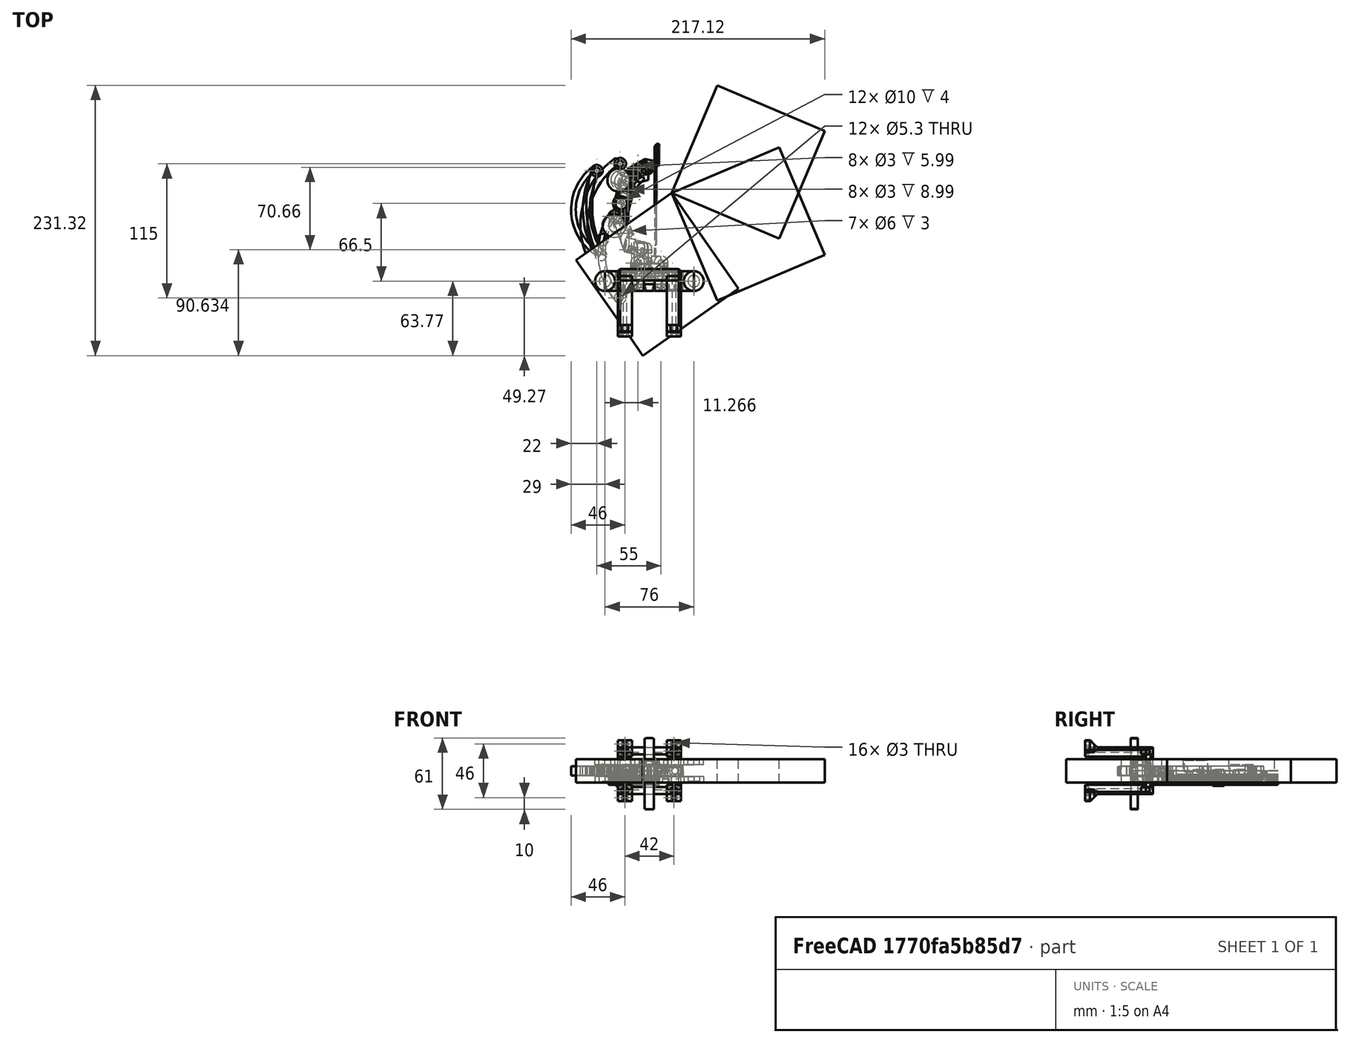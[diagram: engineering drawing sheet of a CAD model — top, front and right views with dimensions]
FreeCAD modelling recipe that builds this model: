
FCSTD DOCUMENT  (FreeCAD 0.19R24276 (Git))
Label: Gripper_024
License: All rights reserved
LicenseURL: http://en.wikipedia.org/wiki/All_rights_reserved
objects: Part::Cylinder×485, Part::Cut×312, Part::Box×216, Part::Compound×169, Part::Fillet×55, Mesh::Feature×27, Part::FeaturePython×21, Part::Chamfer×20, Part::Common×2, Part::Mirroring×1
note: 1281 computed .brp shape members not serialized (recipe doc carries the construction recipe); baked Part::Feature solids carry a one-line shape summary decoded from their .brp

FEATURE [Part::Cylinder] Cylinder036  label="Válec036"
  Angle = 360
  AttacherType = Attacher::AttachEngine3D
  Height = 5
  Placement = pos=(-20,30,5) rot=(0,0,1;0rad)
  Radius = 16
FEATURE [Part::Box] Box045  label="Krychle045"
  AttacherType = Attacher::AttachEngine3D
  Height = 12
  Length = 12
  Placement = pos=(-13,24,-2) rot=(0,0,1;0rad)
  Width = 12
FEATURE [Part::Cylinder] Cylinder037  label="Válec037"
  Angle = 360
  AttacherType = Attacher::AttachEngine3D
  Height = 4
  Placement = pos=(-10,30,1) rot=(0,0,1;0rad)
  Radius = 5
FEATURE [Part::Box] Box046  label="Krychle046"
  AttacherType = Attacher::AttachEngine3D
  Height = 12
  Length = 12
  Placement = pos=(-6.8,59.2,-2) rot=(0,0,-1;0.785398rad)
  Width = 16
FEATURE [Part::Box] Box047  label="Krychle047"
  AttacherType = Attacher::AttachEngine3D
  Height = 2
  Length = 6
  Placement = pos=(-2,11,20) rot=(0,0,1;0rad)
  Width = 6
FEATURE [Part::Box] Box049  label="Krychle049"
  AttacherType = Attacher::AttachEngine3D
  Height = 12
  Length = 12
  Placement = pos=(-13,36,-2) rot=(0,0,-1;0.261799rad)
  Width = 24
FEATURE [Part::Cylinder] Cylinder040  label="Válec040"
  Angle = 360
  AttacherType = Attacher::AttachEngine3D
  Height = 4
  Placement = pos=(10,-10,1) rot=(0,0,1;0rad)
  Radius = 5
FEATURE [Part::Box] Box053  label="Krychle053"
  AttacherType = Attacher::AttachEngine3D
  Height = 12
  Length = 12
  Placement = pos=(16,0,-2) rot=(0,0,1;0rad)
  Width = 80
FEATURE [Part::Cylinder] Cylinder042  label="Válec042"
  Angle = 360
  AttacherType = Attacher::AttachEngine3D
  Height = 5
  Placement = pos=(-20,30,5) rot=(0,0,1;0rad)
  Radius = 16
FEATURE [Part::Cylinder] Cylinder043  label="Válec043"
  Angle = 360
  AttacherType = Attacher::AttachEngine3D
  Height = 7
  Placement = pos=(10,-10,-2) rot=(0,0,1;0rad)
  Radius = 7
FEATURE [Part::Cut] Cut039
  Base = -> Cylinder043
  Tool = -> Cylinder040
FEATURE [Part::Cylinder] Cylinder039  label="Válec039"
  Angle = 360
  AttacherType = Attacher::AttachEngine3D
  Height = 5
  Placement = pos=(-20,30,5) rot=(0,0,1;0rad)
  Radius = 16
FEATURE [Part::Cut] Cut040
  Base = -> Box049
  Tool = -> Cylinder039
FEATURE [Part::Fillet] Fillet009
  Base = -> Cut040
  Edges = 1 edges r=20: [Edge3]
FEATURE [Part::Box] Box048  label="Krychle048"
  AttacherType = Attacher::AttachEngine3D
  Height = 12
  Length = 12
  Placement = pos=(-4.1,-0.4,-2) rot=(0,0,1;0.349066rad)
  Width = 26
FEATURE [Part::Cut] Cut038
  Base = -> Box048
  Tool = -> Cylinder042
FEATURE [Part::Fillet] Fillet011
  Base = -> Cut038
  Edges = 1 edges r=20: [Edge2]
FEATURE [Part::Fillet] Fillet016
  Base = -> Fillet011
  Edges = 1 edges r=2: [Edge2]
FEATURE [Part::Box] Box050  label="Krychle050"
  AttacherType = Attacher::AttachEngine3D
  Height = 12
  Length = 12
  Placement = pos=(4.5,70.5,-2) rot=(0,0,-1;1.309rad)
  Width = 12
FEATURE [Part::Cut] Cut037
  Base = -> Box050
  Tool = -> Box053
FEATURE [Part::Box] Box051  label="Krychle051"
  AttacherType = Attacher::AttachEngine3D
  Height = 12
  Length = 12
  Placement = pos=(11.4,-4.4,-2) rot=(0,0,1;1.309rad)
  Width = 18
FEATURE [Part::Chamfer] Chamfer001
  Base = -> Box051
  Edges = 2 edges r=4: [Edge1,Edge5]
FEATURE [Part::Fillet] Fillet010
  Base = -> Chamfer001
  Edges = 1 edges r=4: [Edge4]
FEATURE [Part::Fillet] Fillet015
  Base = -> Fillet010
  Edges = 1 edges r=3: [Edge2]
FEATURE [Part::Fillet] Fillet014
  Base = -> Fillet015
  Edges = 2 edges r=3: [Edge21,Edge23]
FEATURE [Part::Fillet] Fillet013
  Base = -> Fillet014
  Edges = 1 edges r=4: [Edge27]
FEATURE [Part::Box] Box052  label="Krychle052"
  AttacherType = Attacher::AttachEngine3D
  Height = 7
  Length = 12
  Placement = pos=(4,-10,-2) rot=(0,0,1;0rad)
  Width = 18
FEATURE [Part::Cylinder] Cylinder041  label="Válec041"
  Angle = 360
  AttacherType = Attacher::AttachEngine3D
  Height = 4
  Placement = pos=(10,-10,1) rot=(0,0,1;0rad)
  Radius = 5
FEATURE [Part::Cut] Cut036
  Base = -> Box052
  Tool = -> Cylinder041
FEATURE [Part::Fillet] Fillet012
  Base = -> Cut036
  Edges = 1 edges r=4: [Edge16]
FEATURE [Part::Cylinder] Cylinder044  label="Válec044"
  Angle = 360
  AttacherType = Attacher::AttachEngine3D
  Height = 3
  Placement = pos=(1,14,-2) rot=(0,0,1;0rad)
  Radius = 3
FEATURE [Part::Box] Box054  label="Krychle054"
  AttacherType = Attacher::AttachEngine3D
  Height = 2
  Length = 6
  Placement = pos=(-2,11,20) rot=(0,0,1;0rad)
  Width = 6
FEATURE [Part::Cylinder] Cylinder038  label="Válec038"
  Angle = 360
  AttacherType = Attacher::AttachEngine3D
  Height = 16
  Placement = pos=(1,14,1) rot=(0,0,1;0rad)
  Radius = 1.5
FEATURE [Part::Compound] Compound016
  Links = -> [Cylinder037,Cylinder036]
FEATURE [Part::Cut] Cut041
  Base = -> Box045
  Tool = -> Compound016
FEATURE [Part::Cylinder] Cylinder053  label="Válec053"
  Angle = 360
  AttacherType = Attacher::AttachEngine3D
  Height = 3
  Placement = pos=(1,14,-2) rot=(0,0,1;0rad)
  Radius = 3
FEATURE [Part::Compound] Compound018
  Links = -> [Box047,Cylinder038,Cylinder053]
  Placement = pos=(12.1,54,0) rot=(0,0,1;0.785398rad)
FEATURE [Part::Box] Box058  label="Krychle058"
  AttacherType = Attacher::AttachEngine3D
  Height = 2
  Length = 6
  Placement = pos=(-2,11,20) rot=(0,0,1;0rad)
  Width = 6
FEATURE [Part::Cylinder] Cylinder051  label="Válec051"
  Angle = 360
  AttacherType = Attacher::AttachEngine3D
  Height = 16
  Placement = pos=(1,14,1) rot=(0,0,1;0rad)
  Radius = 1.5
FEATURE [Part::Cylinder] Cylinder054  label="Válec054"
  Angle = 360
  AttacherType = Attacher::AttachEngine3D
  Height = 16
  Placement = pos=(1,14,1) rot=(0,0,1;0rad)
  Radius = 1.5
FEATURE [Part::Box] Box057  label="Krychle057"
  AttacherType = Attacher::AttachEngine3D
  Height = 2
  Length = 6
  Placement = pos=(-2,11,20) rot=(0,0,1;0rad)
  Width = 6
FEATURE [Part::Cylinder] Cylinder045  label="Válec045"
  Angle = 360
  AttacherType = Attacher::AttachEngine3D
  Height = 3
  Placement = pos=(1,14,-2) rot=(0,0,1;0rad)
  Radius = 3
FEATURE [Part::Box] Box059  label="Krychle059"
  AttacherType = Attacher::AttachEngine3D
  Height = 2
  Length = 6
  Placement = pos=(-2,11,4) rot=(0,0,1;0rad)
  Width = 6
FEATURE [Part::Box] Box056  label="Krychle056"
  AttacherType = Attacher::AttachEngine3D
  Height = 2
  Length = 6
  Placement = pos=(-2,11,20) rot=(0,0,1;0rad)
  Width = 6
FEATURE [Part::Box] Box060  label="Krychle060"
  AttacherType = Attacher::AttachEngine3D
  Height = 2
  Length = 6
  Placement = pos=(-2,11,4) rot=(0,0,1;0rad)
  Width = 6
FEATURE [Part::Cylinder] Cylinder048  label="Válec048"
  Angle = 360
  AttacherType = Attacher::AttachEngine3D
  Height = 3
  Placement = pos=(1,14,-2) rot=(0,0,1;0rad)
  Radius = 3
FEATURE [Part::Compound] Compound014
  Links = -> [Box056,Cylinder051,Cylinder048]
  Placement = pos=(-2.9,-11.9,0) rot=(0,0,-1;0.261799rad)
FEATURE [Part::Cylinder] Cylinder049  label="Válec049"
  Angle = 360
  AttacherType = Attacher::AttachEngine3D
  Height = 3
  Placement = pos=(1,14,-2) rot=(0,0,1;0rad)
  Radius = 3
FEATURE [Part::Box] Box055  label="Krychle055"
  AttacherType = Attacher::AttachEngine3D
  Height = 2
  Length = 6
  Placement = pos=(-2,11,20) rot=(0,0,1;0rad)
  Width = 6
FEATURE [Part::Cylinder] Cylinder047  label="Válec047"
  Angle = 360
  AttacherType = Attacher::AttachEngine3D
  Height = 16
  Placement = pos=(1,14,1) rot=(0,0,1;0rad)
  Radius = 1.5
FEATURE [Part::Compound] Compound015
  Links = -> [Box055,Cylinder047,Cylinder045]
  Placement = pos=(-6.1,31,0) rot=(0,0,-1;0.261799rad)
FEATURE [Part::Cut] Cut043
  Base = -> Fillet009
  Tool = -> Compound015
FEATURE [Part::Cylinder] Cylinder050  label="Válec050"
  Angle = 360
  AttacherType = Attacher::AttachEngine3D
  Height = 16
  Placement = pos=(1,14,1) rot=(0,0,1;0rad)
  Radius = 1.5
FEATURE [Part::Compound] Compound011
  Links = -> [Box057,Cylinder050,Cylinder049]
  Placement = pos=(-2.9,-11.9,0) rot=(0,0,-1;0.261799rad)
FEATURE [Part::Cut] Cut044
  Base = -> Fillet013
  Tool = -> Compound011
FEATURE [Part::Cylinder] Cylinder046  label="Válec046"
  Angle = 360
  AttacherType = Attacher::AttachEngine3D
  Height = 3
  Placement = pos=(1,14,-2) rot=(0,0,1;0rad)
  Radius = 3
FEATURE [Part::Compound] Compound013
  Links = -> [Box058,Cylinder054,Cylinder046]
  Placement = pos=(3.5,2,0) rot=(0,0,1;0.349066rad)
FEATURE [Part::Cut] Cut042
  Base = -> Fillet016
  Tool = -> Compound013
FEATURE [Part::Cut] Cut045
  Base = -> Cut042
  Tool = -> Compound014
FEATURE [Part::Cylinder] Cylinder052  label="Válec052"
  Angle = 360
  AttacherType = Attacher::AttachEngine3D
  Height = 16
  Placement = pos=(1,14,1) rot=(0,0,1;0rad)
  Radius = 1.5
FEATURE [Part::Compound] Compound012
  Links = -> [Box054,Cylinder052,Cylinder044]
  Placement = pos=(12.1,54,0) rot=(0,0,1;0.785398rad)
FEATURE [Part::Cut] Cut049
  Base = -> Box046
  Tool = -> Compound018
FEATURE [Part::Cut] Cut047
  Base = -> Cut037
  Tool = -> Compound012
FEATURE [Part::Cylinder] Cylinder064  label="Válec064"
  Angle = 360
  AttacherType = Attacher::AttachEngine3D
  Height = 12
  Placement = pos=(1,14,6) rot=(0,0,1;0rad)
  Radius = 1.5
FEATURE [Part::Box] Box063  label="Krychle063"
  AttacherType = Attacher::AttachEngine3D
  Height = 2
  Length = 6
  Placement = pos=(-2,11,4) rot=(0,0,1;0rad)
  Width = 6
FEATURE [Part::Cylinder] Cylinder065  label="Válec065"
  Angle = 360
  AttacherType = Attacher::AttachEngine3D
  Height = 12
  Placement = pos=(1,14,6) rot=(0,0,1;0rad)
  Radius = 1.5
FEATURE [Part::Box] Box064  label="Krychle064"
  AttacherType = Attacher::AttachEngine3D
  Height = 2
  Length = 6
  Placement = pos=(-2,11,4) rot=(0,0,1;0rad)
  Width = 6
FEATURE [Part::Cylinder] Cylinder066  label="Válec066"
  Angle = 360
  AttacherType = Attacher::AttachEngine3D
  Height = 4
  Placement = pos=(1,14,-0.1) rot=(0,0,1;0rad)
  Radius = 1.5
FEATURE [Part::Cylinder] Cylinder057  label="Válec057"
  Angle = 360
  AttacherType = Attacher::AttachEngine3D
  Height = 12
  Placement = pos=(1,14,6) rot=(0,0,1;0rad)
  Radius = 1.5
FEATURE [Part::Cylinder] Cylinder058  label="Válec058"
  Angle = 360
  AttacherType = Attacher::AttachEngine3D
  Height = 12
  Placement = pos=(1,14,6) rot=(0,0,1;0rad)
  Radius = 1.5
FEATURE [Part::Cylinder] Cylinder055  label="Válec055"
  Angle = 360
  AttacherType = Attacher::AttachEngine3D
  Height = 4
  Placement = pos=(1,14,-0.1) rot=(0,0,1;0rad)
  Radius = 1.5
FEATURE [Part::Compound] Compound019
  Links = -> [Box060,Cylinder058,Cylinder055]
  Placement = pos=(6,53,2) rot=(0,1,0;1.5708rad)
FEATURE [Part::Cut] Cut048
  Base = -> Cut047
  Tool = -> Compound019
FEATURE [Part::Cylinder] Cylinder056  label="Válec056"
  Angle = 360
  AttacherType = Attacher::AttachEngine3D
  Height = 4
  Placement = pos=(1,14,0) rot=(0,0,1;0rad)
  Radius = 1.5
FEATURE [Part::Compound] Compound020
  Links = -> [Box059,Cylinder057,Cylinder056]
  Placement = pos=(6,53,2) rot=(0,1,0;1.5708rad)
FEATURE [Part::Cut] Cut046
  Base = -> Cut049
  Tool = -> Compound020
FEATURE [Part::Cylinder] Cylinder063  label="Válec063"
  Angle = 360
  AttacherType = Attacher::AttachEngine3D
  Height = 4
  Placement = pos=(1,14,-0.1) rot=(0,0,1;0rad)
  Radius = 1.5
FEATURE [Part::Compound] Compound024
  Links = -> [Box063,Cylinder064,Cylinder063]
  Placement = pos=(6,-14,2) rot=(0,1,0;1.5708rad)
FEATURE [Part::Cut] Cut052
  Base = -> Fillet012
  Tool = -> Compound024
FEATURE [Part::Compound] Compound026
  Links = -> [Box064,Cylinder065,Cylinder066]
  Placement = pos=(6,-14,2) rot=(0,1,0;1.5708rad)
FEATURE [Part::Cut] Cut053
  Base = -> Cut044
  Tool = -> Compound026
FEATURE [Part::Compound] Compound027  label="revised_finger_upper"
  Links = -> [Cut039,Cut041,Cut043,Cut045,Cut046,Cut048,Cut052,Cut053]
FEATURE [Part::Cylinder] Cylinder067  label="Válec067"
  Angle = 360
  AttacherType = Attacher::AttachEngine3D
  Height = 7
  Placement = pos=(10,-10,-2) rot=(0,0,1;0rad)
  Radius = 7
FEATURE [Part::Cylinder] Cylinder068  label="Válec068"
  Angle = 360
  AttacherType = Attacher::AttachEngine3D
  Height = 4
  Placement = pos=(10,-10,1) rot=(0,0,1;0rad)
  Radius = 5
FEATURE [Part::Cut] Cut054
  Base = -> Cylinder067
  Placement = pos=(3,-1,0) rot=(0,0,1;0rad)
  Tool = -> Cylinder068
FEATURE [Part::Box] Box065  label="Krychle065"
  AttacherType = Attacher::AttachEngine3D
  Height = 12
  Length = 12
  Placement = pos=(-13,24,-2) rot=(0,0,1;0rad)
  Width = 18
FEATURE [Part::Box] Box066  label="Krychle066"
  AttacherType = Attacher::AttachEngine3D
  Height = 12
  Length = 12
  Placement = pos=(-13,42,-2) rot=(0,0,-1;0.261799rad)
  Width = 20
FEATURE [Part::Box] Box067  label="Krychle067"
  AttacherType = Attacher::AttachEngine3D
  Height = 12
  Length = 12
  Placement = pos=(-4.1,-0.4,-2) rot=(0,0,1;0.349066rad)
  Width = 26
FEATURE [Part::Box] Box068  label="Krychle068"
  AttacherType = Attacher::AttachEngine3D
  Height = 12
  Length = 12
  Placement = pos=(-7.85,61.2,-2) rot=(0,0,-1;0.610865rad)
  Width = 12
FEATURE [Part::Box] Box069  label="Krychle069"
  AttacherType = Attacher::AttachEngine3D
  Height = 12
  Length = 12
  Placement = pos=(5,60.6,-2) rot=(0,0,1;0.523599rad)
  Width = 12
FEATURE [Part::Box] Box070  label="Krychle070"
  AttacherType = Attacher::AttachEngine3D
  Height = 7
  Length = 12
  Placement = pos=(4,-10,-2) rot=(0,0,1;0rad)
  Width = 18
FEATURE [Part::Box] Box071  label="Krychle071"
  AttacherType = Attacher::AttachEngine3D
  Height = 12
  Length = 12
  Placement = pos=(13.25,-5,-2) rot=(0,0,1;1.309rad)
  Width = 18
FEATURE [Part::Cylinder] Cylinder069  label="Válec069"
  Angle = 360
  AttacherType = Attacher::AttachEngine3D
  Height = 10
  Placement = pos=(-9,24,1) rot=(0,0,1;0rad)
  Radius = 5
FEATURE [Part::Cylinder] Cylinder070  label="Válec070"
  Angle = 360
  AttacherType = Attacher::AttachEngine3D
  Height = 4
  Placement = pos=(-10,30,1) rot=(0,0,1;0rad)
  Radius = 5
FEATURE [Part::Cylinder] Cylinder071  label="Válec071"
  Angle = 360
  AttacherType = Attacher::AttachEngine3D
  Height = 10
  Placement = pos=(-7,41,1) rot=(0,0,1;0rad)
  Radius = 5
FEATURE [Part::Cylinder] Cylinder072  label="Válec072"
  Angle = 360
  AttacherType = Attacher::AttachEngine3D
  Height = 7
  Placement = pos=(-7,41,-2) rot=(0,0,1;0rad)
  Radius = 7
FEATURE [Part::Cylinder] Cylinder073  label="Válec073"
  Angle = 360
  AttacherType = Attacher::AttachEngine3D
  Height = 7
  Placement = pos=(-7,41,5) rot=(0,0,1;0rad)
  Radius = 7
FEATURE [Part::Cut] Cut
  Base = -> Box065
  Tool = -> Cylinder073
FEATURE [Part::Cylinder] Cylinder074  label="Válec074"
  Angle = 360
  AttacherType = Attacher::AttachEngine3D
  Height = 10
  Placement = pos=(-7,41,1) rot=(0,0,1;0rad)
  Radius = 5
FEATURE [Part::Cut] Cut055
  Base = -> Cylinder072
  Tool = -> Cylinder074
FEATURE [Part::Cylinder] Cylinder075  label="Válec075"
  Angle = 360
  AttacherType = Attacher::AttachEngine3D
  Height = 10
  Placement = pos=(-7,41,1) rot=(0,0,1;0rad)
  Radius = 5
FEATURE [Part::Cut] Cut056
  Base = -> Cut
  Tool = -> Cylinder075
FEATURE [Part::Cylinder] Cylinder076  label="Válec076"
  Angle = 360
  AttacherType = Attacher::AttachEngine3D
  Height = 4
  Placement = pos=(-7,41,6) rot=(0,0,1;0rad)
  Radius = 6
FEATURE [Part::Box] Box072  label="Krychle072"
  AttacherType = Attacher::AttachEngine3D
  Height = 4
  Length = 12
  Placement = pos=(-13,42,6) rot=(0,0,-1;0.261799rad)
  Width = 20
FEATURE [Part::Cylinder] Cylinder077  label="Válec077"
  Angle = 360
  AttacherType = Attacher::AttachEngine3D
  Height = 8
  Placement = pos=(-7,41,-2) rot=(0,0,1;0rad)
  Radius = 9
FEATURE [Part::Cut] Cut057
  Base = -> Box066
  Tool = -> Cylinder077
FEATURE [Part::Cut] Cut058
  Base = -> Box066
  Tool = -> Cylinder077
FEATURE [Part::Cylinder] Cylinder078  label="Válec078"
  Angle = 360
  AttacherType = Attacher::AttachEngine3D
  Height = 10
  Placement = pos=(-5,59,1) rot=(0,0,1;0rad)
  Radius = 5
FEATURE [Part::Cylinder] Cylinder079  label="Válec079"
  Angle = 360
  AttacherType = Attacher::AttachEngine3D
  Height = 10
  Placement = pos=(-9,61,5) rot=(0,0,1;0rad)
  Radius = 10
FEATURE [Part::Cut] Cut059
  Base = -> Box068
  Tool = -> Cylinder079
FEATURE [Part::Cylinder] Cylinder080  label="Válec080"
  Angle = 360
  AttacherType = Attacher::AttachEngine3D
  Height = 10
  Placement = pos=(-9,61,5) rot=(0,0,1;0rad)
  Radius = 10
FEATURE [Part::Cut] Cut060
  Base = -> Box072
  Tool = -> Cylinder080
FEATURE [Part::Cylinder] Cylinder081  label="Válec081"
  Angle = 360
  AttacherType = Attacher::AttachEngine3D
  Height = 10
  Placement = pos=(-9,61,5) rot=(0,0,1;0rad)
  Radius = 10
FEATURE [Part::Cut] Cut061
  Base = -> Cut057
  Tool = -> Cylinder081
FEATURE [Part::Cylinder] Cylinder082  label="Válec082"
  Angle = 360
  AttacherType = Attacher::AttachEngine3D
  Height = 10
  Placement = pos=(-9,61,5) rot=(0,0,1;0rad)
  Radius = 10
FEATURE [Part::Cut] Cut062
  Base = -> Cut058
  Tool = -> Cylinder082
FEATURE [Part::Cylinder] Cylinder083  label="Válec083"
  Angle = 360
  AttacherType = Attacher::AttachEngine3D
  Height = 10
  Placement = pos=(-5,59,1) rot=(0,0,1;0rad)
  Radius = 5
FEATURE [Part::Cylinder] Cylinder084  label="Válec084"
  Angle = 360
  AttacherType = Attacher::AttachEngine3D
  Height = 10
  Placement = pos=(-5,59,1) rot=(0,0,1;0rad)
  Radius = 5
FEATURE [Part::Cut] Cut063
  Base = -> Cut061
  Tool = -> Cylinder083
FEATURE [Part::Cylinder] Cylinder085  label="Válec085"
  Angle = 360
  AttacherType = Attacher::AttachEngine3D
  Height = 10
  Placement = pos=(-9,61,5) rot=(0,0,1;0rad)
  Radius = 10
FEATURE [Part::Cylinder] Cylinder086  label="Válec086"
  Angle = 360
  AttacherType = Attacher::AttachEngine3D
  Height = 10
  Placement = pos=(-9,61,5) rot=(0,0,1;0rad)
  Radius = 10
FEATURE [Part::Cylinder] Cylinder087  label="Válec087"
  Angle = 360
  AttacherType = Attacher::AttachEngine3D
  Height = 10
  Placement = pos=(-5,59,1) rot=(0,0,1;0rad)
  Radius = 5
FEATURE [Part::Cut] Cut064
  Base = -> Cut059
  Tool = -> Cylinder087
FEATURE [Part::Fillet] Fillet
  Base = -> Cut064
  Edges = 1 edges r=3: [Edge5]
FEATURE [Part::Fillet] Fillet017
  Base = -> Cut063
  Edges = 1 edges r=2: [Edge3]
FEATURE [Part::Cylinder] Cylinder088  label="Válec088"
  Angle = 360
  AttacherType = Attacher::AttachEngine3D
  Height = 10
  Placement = pos=(-7,41,0) rot=(0,0,1;0rad)
  Radius = 5
FEATURE [Part::Cylinder] Cylinder089  label="Válec089"
  Angle = 360
  AttacherType = Attacher::AttachEngine3D
  Height = 10
  Placement = pos=(-7,41,-3) rot=(0,0,1;0rad)
  Radius = 5
FEATURE [Part::Cut] Cut065
  Base = -> Cylinder076
  Tool = -> Cylinder088
FEATURE [Part::Cylinder] Cylinder090  label="Válec090"
  Angle = 360
  AttacherType = Attacher::AttachEngine3D
  Height = 4
  Placement = pos=(-7,41,6) rot=(0,0,1;0rad)
  Radius = 6
FEATURE [Mesh::Feature] Mesh  label="Grip_finger-tip (Meshed)"
FEATURE [Part::Cylinder] Cylinder091  label="Válec091"
  Angle = 360
  AttacherType = Attacher::AttachEngine3D
  Height = 10
  Placement = pos=(-9,23,1) rot=(0,0,1;0rad)
  Radius = 5
FEATURE [Part::Cylinder] Cylinder092  label="Válec092"
  Angle = 360
  AttacherType = Attacher::AttachEngine3D
  Height = 10
  Placement = pos=(-13,22,5) rot=(0,0,1;0rad)
  Radius = 10
FEATURE [Part::Cut] Cut066
  Base = -> Box067
  Tool = -> Cylinder092
FEATURE [Part::Cylinder] Cylinder093  label="Válec093"
  Angle = 360
  AttacherType = Attacher::AttachEngine3D
  Height = 10
  Placement = pos=(-13,22,9) rot=(0,0,1;0rad)
  Radius = 10
FEATURE [Part::Cylinder] Cylinder094  label="Válec094"
  Angle = 360
  AttacherType = Attacher::AttachEngine3D
  Height = 10
  Placement = pos=(-13,22,5) rot=(0,0,1;0rad)
  Radius = 10
FEATURE [Part::Cut] Cut067
  Base = -> Cut056
  Tool = -> Cylinder094
FEATURE [Part::Cylinder] Cylinder095  label="Válec095"
  Angle = 360
  AttacherType = Attacher::AttachEngine3D
  Height = 10
  Placement = pos=(-9,23,1) rot=(0,0,1;0rad)
  Radius = 5
FEATURE [Part::Cut] Cut068
  Base = -> Cut066
  Tool = -> Cylinder095
FEATURE [Part::Cut] Cut069
  Base = -> Cut067
  Tool = -> Cylinder091
FEATURE [Part::Cylinder] Cylinder096  label="Válec096"
  Angle = 360
  AttacherType = Attacher::AttachEngine3D
  Height = 4
  Placement = pos=(10,-10,1) rot=(0,0,1;0rad)
  Radius = 5
FEATURE [Part::Cut] Cut070
  Base = -> Box070
  Placement = pos=(3,0,0) rot=(0,0,1;0rad)
  Tool = -> Cylinder096
FEATURE [Part::Fillet] Fillet020
  Base = -> Cut070
  Edges = 1 edges r=4: [Edge16]
  Placement = pos=(0,-1,0) rot=(0,0,1;0rad)
FEATURE [Part::Fillet] Fillet021
  Base = -> Box071
  Edges = 2 edges r=4: [Edge1,Edge5]
FEATURE [Part::Fillet] Fillet022
  Base = -> Cut069
  Edges = 1 edges r=4: [Edge10]
FEATURE [Part::Fillet] Fillet023
  Base = -> Cut068
  Edges = 1 edges r=6: [Edge2]
FEATURE [Part::Compound] Compound028
  Links = -> [Fillet023,Fillet022,Fillet021,Fillet020,Cut055,Cut054]
FEATURE [Part::Fillet] Fillet024  label="Grip_finger-root_precur"
  Base = -> Compound028
  Edges = 1 edges r=2: [Edge53]
FEATURE [Part::Fillet] Fillet025
  Base = -> Box069
  Edges = 1 edges r=4: [Edge5]
FEATURE [Part::Fillet] Fillet026
  Base = -> Fillet017
  Edges = 1 edges r=3: [Edge28]
FEATURE [Part::Compound] Compound  label="Grip_finger-tip_precur"
  Links = -> [Fillet025,Fillet026,Fillet,Cylinder090]
FEATURE [Part::Cylinder] Cylinder097  label="Válec097"
  Angle = 360
  AttacherType = Attacher::AttachEngine3D
  Height = 4
  Placement = pos=(-7,41,6) rot=(0,0,1;0rad)
  Radius = 6
FEATURE [Part::Cylinder] Cylinder098  label="Válec098"
  Angle = 360
  AttacherType = Attacher::AttachEngine3D
  Height = 7
  Placement = pos=(-5,59.5,-2) rot=(0,0,1;0rad)
  Radius = 8
FEATURE [Part::Cylinder] Cylinder099  label="Válec099"
  Angle = 360
  AttacherType = Attacher::AttachEngine3D
  Height = 10
  Placement = pos=(-8,61,1) rot=(0,0,1;0rad)
  Radius = 5
FEATURE [Part::Cut] Cut074
  Base = -> Cylinder098
  Tool = -> Cylinder099
FEATURE [Part::Cylinder] Cylinder100  label="Válec100"
  Angle = 360
  AttacherType = Attacher::AttachEngine3D
  Height = 10
  Placement = pos=(-8,61,1) rot=(0,0,1;0rad)
  Radius = 5
FEATURE [Part::Box] Box073  label="Krychle073"
  AttacherType = Attacher::AttachEngine3D
  Height = 12
  Length = 12
  Placement = pos=(-13,42,-2) rot=(0,0,-1;0.261799rad)
  Width = 20
FEATURE [Part::Box] Box074  label="Krychle074"
  AttacherType = Attacher::AttachEngine3D
  Height = 12
  Length = 12
  Placement = pos=(-7.85,61.2,-2) rot=(0,0,-1;0.610865rad)
  Width = 12
FEATURE [Part::Box] Box075  label="Krychle075"
  AttacherType = Attacher::AttachEngine3D
  Height = 12
  Length = 12
  Placement = pos=(5,60.6,-2) rot=(0,0,1;0.523599rad)
  Width = 12
FEATURE [Part::Fillet] Fillet029
  Base = -> Box075
  Edges = 1 edges r=4: [Edge5]
FEATURE [Part::Cylinder] Cylinder101  label="Válec101"
  Angle = 360
  AttacherType = Attacher::AttachEngine3D
  Height = 8
  Placement = pos=(-7,41,-2) rot=(0,0,1;0rad)
  Radius = 9
FEATURE [Part::Cut] Cut075
  Base = -> Box073
  Tool = -> Cylinder101
FEATURE [Part::Cylinder] Cylinder102  label="Válec102"
  Angle = 360
  AttacherType = Attacher::AttachEngine3D
  Height = 10
  Placement = pos=(-9,61,5) rot=(0,0,1;0rad)
  Radius = 10
FEATURE [Part::Cut] Cut076
  Base = -> Box074
  Tool = -> Cylinder102
FEATURE [Part::Cylinder] Cylinder103  label="Válec103"
  Angle = 360
  AttacherType = Attacher::AttachEngine3D
  Height = 10
  Placement = pos=(-9,61,5) rot=(0,0,1;0rad)
  Radius = 10
FEATURE [Part::Cut] Cut077
  Base = -> Cut075
  Tool = -> Cylinder103
FEATURE [Part::Cylinder] Cylinder104  label="Válec104"
  Angle = 360
  AttacherType = Attacher::AttachEngine3D
  Height = 10
  Placement = pos=(-5,59,1) rot=(0,0,1;0rad)
  Radius = 5
FEATURE [Part::Cut] Cut071
  Base = -> Cut077
  Tool = -> Cylinder104
FEATURE [Part::Fillet] Fillet027
  Base = -> Cut071
  Edges = 1 edges r=2: [Edge3]
FEATURE [Part::Fillet] Fillet030
  Base = -> Fillet027
  Edges = 1 edges r=1: [Edge28]
FEATURE [Part::Cylinder] Cylinder105  label="Válec105"
  Angle = 360
  AttacherType = Attacher::AttachEngine3D
  Height = 10
  Placement = pos=(-5,59,1) rot=(0,0,1;0rad)
  Radius = 5
FEATURE [Part::Cut] Cut072
  Base = -> Cut076
  Tool = -> Cylinder105
FEATURE [Part::Fillet] Fillet028
  Base = -> Cut072
  Edges = 1 edges r=3: [Edge5]
FEATURE [Part::Cut] Cut073
  Base = -> Fillet028
  Tool = -> Cylinder100
FEATURE [Part::Cylinder] Cylinder029  label="Válec029"
  Angle = 360
  AttacherType = Attacher::AttachEngine3D
  Height = 20
  Placement = pos=(1,14,4.01) rot=(0,0,1;0rad)
  Radius = 1.5
FEATURE [Part::Cylinder] Cylinder106  label="Válec106"
  Angle = 360
  AttacherType = Attacher::AttachEngine3D
  Height = 20
  Placement = pos=(1,14,4.01) rot=(0,0,1;0rad)
  Radius = 1.5
FEATURE [Part::Cylinder] Cylinder107  label="Válec107"
  Angle = 360
  AttacherType = Attacher::AttachEngine3D
  Height = 3
  Placement = pos=(1,14,-1.01) rot=(0,0,1;0rad)
  Radius = 1.5
FEATURE [Part::Box] Box076  label="Krychle076"
  AttacherType = Attacher::AttachEngine3D
  Height = 2
  Length = 6
  Placement = pos=(-2,11,2) rot=(0,0,1;0rad)
  Width = 6
FEATURE [Part::Compound] Compound023
  Links = -> [Box076,Cylinder106,Cylinder107]
  Placement = pos=(12.3,47.5,0) rot=(0,0,1;1.309rad)
FEATURE [Part::Box] Box077  label="Krychle077"
  AttacherType = Attacher::AttachEngine3D
  Height = 2
  Length = 6
  Placement = pos=(-2,11,2) rot=(0,0,1;0rad)
  Width = 6
FEATURE [Part::Cylinder] Cylinder108  label="Válec108"
  Angle = 360
  AttacherType = Attacher::AttachEngine3D
  Height = 3
  Placement = pos=(1,14,-1.01) rot=(0,0,1;0rad)
  Radius = 1.5
FEATURE [Part::Cylinder] Cylinder109  label="Válec109"
  Angle = 360
  AttacherType = Attacher::AttachEngine3D
  Height = 20
  Placement = pos=(1,14,4.01) rot=(0,0,1;0rad)
  Radius = 1.5
FEATURE [Part::Cylinder] Cylinder028  label="Válec028"
  Angle = 360
  AttacherType = Attacher::AttachEngine3D
  Height = 3
  Placement = pos=(1,14,-1.01) rot=(0,0,1;0rad)
  Radius = 1.5
FEATURE [Part::Box] Box041  label="Krychle041"
  AttacherType = Attacher::AttachEngine3D
  Height = 2
  Length = 6
  Placement = pos=(-2,11,2) rot=(0,0,1;0rad)
  Width = 6
FEATURE [Part::Compound] Compound029
  Links = -> [Box077,Cylinder109,Cylinder108]
  Placement = pos=(12.3,47.5,0) rot=(0,0,1;1.309rad)
FEATURE [Part::Cut] Cut083
  Base = -> Fillet030
  Tool = -> Compound029
FEATURE [Part::Compound] Compound006
  Links = -> [Box041,Cylinder029,Cylinder028]
  Placement = pos=(9.4,57.4,0) rot=(0,0,1;0.523599rad)
FEATURE [Part::Cut] Cut084
  Base = -> Cut074
  Tool = -> Compound023
FEATURE [Part::Cylinder] Cylinder110  label="Válec110"
  Angle = 360
  AttacherType = Attacher::AttachEngine3D
  Height = 20
  Placement = pos=(1,14,4.01) rot=(0,0,1;0rad)
  Radius = 1.5
FEATURE [Part::Cylinder] Cylinder111  label="Válec111"
  Angle = 360
  AttacherType = Attacher::AttachEngine3D
  Height = 3
  Placement = pos=(1,14,-1.01) rot=(0,0,1;0rad)
  Radius = 1.5
FEATURE [Part::Box] Box078  label="Krychle078"
  AttacherType = Attacher::AttachEngine3D
  Height = 2
  Length = 6
  Placement = pos=(-2,11,2) rot=(0,0,1;0rad)
  Width = 6
FEATURE [Part::Cylinder] Cylinder112  label="Válec112"
  Angle = 360
  AttacherType = Attacher::AttachEngine3D
  Height = 20
  Placement = pos=(1,14,4.01) rot=(0,0,1;0rad)
  Radius = 1.5
FEATURE [Part::Cylinder] Cylinder113  label="Válec113"
  Angle = 360
  AttacherType = Attacher::AttachEngine3D
  Height = 3
  Placement = pos=(1,14,-1.01) rot=(0,0,1;0rad)
  Radius = 1.5
FEATURE [Part::Box] Box079  label="Krychle079"
  AttacherType = Attacher::AttachEngine3D
  Height = 2
  Length = 6
  Placement = pos=(-2,11,2) rot=(0,0,1;0rad)
  Width = 6
FEATURE [Part::Box] Box080  label="Krychle080"
  AttacherType = Attacher::AttachEngine3D
  Height = 2
  Length = 6
  Placement = pos=(-2,11,4) rot=(0,0,1;0rad)
  Width = 6
FEATURE [Part::Cylinder] Cylinder114  label="Válec114"
  Angle = 360
  AttacherType = Attacher::AttachEngine3D
  Height = 12
  Placement = pos=(1,14,6) rot=(0,0,1;0rad)
  Radius = 1.5
FEATURE [Part::Cylinder] Cylinder115  label="Válec115"
  Angle = 360
  AttacherType = Attacher::AttachEngine3D
  Height = 4
  Placement = pos=(1,14,0) rot=(0,0,1;0rad)
  Radius = 1.5
FEATURE [Part::Cylinder] Cylinder117  label="Válec117"
  Angle = 360
  AttacherType = Attacher::AttachEngine3D
  Height = 6
  Placement = pos=(-7,41,5) rot=(0,0,1;0rad)
  Radius = 2.6
FEATURE [Part::Cut] Cut082
  Base = -> Cylinder097
  Tool = -> Cylinder117
FEATURE [Part::Cylinder] Cylinder118  label="Válec118"
  Angle = 360
  AttacherType = Attacher::AttachEngine3D
  Height = 6
  Placement = pos=(-7,41,5) rot=(0,0,1;0rad)
  Radius = 2.6
FEATURE [Part::Cut] Cut085
  Base = -> Cut083
  Tool = -> Cylinder118
FEATURE [Part::Compound] Compound025
  Links = -> [Box078,Cylinder110,Cylinder111]
  Placement = pos=(12.3,47.5,0) rot=(0,0,1;1.309rad)
FEATURE [Part::Cut] Cut078
  Base = -> Cut073
  Tool = -> Compound025
FEATURE [Part::Cut] Cut080
  Base = -> Cut078
  Tool = -> Compound006
FEATURE [Part::Compound] Compound031
  Links = -> [Box079,Cylinder112,Cylinder113]
  Placement = pos=(9.4,57.4,0) rot=(0,0,1;0.523599rad)
FEATURE [Part::Cut] Cut079
  Base = -> Fillet029
  Tool = -> Compound031
FEATURE [Part::Compound] Compound032
  Links = -> [Box080,Cylinder114,Cylinder115]
  Placement = pos=(11.7,56.9,2) rot=(-0.250563,0.935113,0.250563;1.63782rad)
FEATURE [Part::Cut] Cut081
  Base = -> Cut079
  Tool = -> Compound032
FEATURE [Part::Compound] Compound030  label="Grip_finger-tip_upper"
  Links = -> [Cut082,Cut081,Cut080,Cut084,Cut085]
FEATURE [Part::Cylinder] Cylinder119  label="Válec119"
  Angle = 360
  AttacherType = Attacher::AttachEngine3D
  Height = 10
  Placement = pos=(-7,41,1) rot=(0,0,1;0rad)
  Radius = 5
FEATURE [Part::Cylinder] Cylinder120  label="Válec120"
  Angle = 360
  AttacherType = Attacher::AttachEngine3D
  Height = 10
  Placement = pos=(-7,41,1) rot=(0,0,1;0rad)
  Radius = 5
FEATURE [Part::Cylinder] Cylinder121  label="Válec121"
  Angle = 360
  AttacherType = Attacher::AttachEngine3D
  Height = 7
  Placement = pos=(10,-10,-2) rot=(0,0,1;0rad)
  Radius = 7
FEATURE [Part::Cylinder] Cylinder122  label="Válec122"
  Angle = 360
  AttacherType = Attacher::AttachEngine3D
  Height = 4
  Placement = pos=(10,-10,1) rot=(0,0,1;0rad)
  Radius = 5
FEATURE [Part::Cut] Cut087
  Base = -> Cylinder121
  Placement = pos=(3,-1,0) rot=(0,0,1;0rad)
  Tool = -> Cylinder122
FEATURE [Part::Box] Box081  label="Krychle081"
  AttacherType = Attacher::AttachEngine3D
  Height = 12
  Length = 12
  Placement = pos=(-13,24,-2) rot=(0,0,1;0rad)
  Width = 18
FEATURE [Part::Box] Box082  label="Krychle082"
  AttacherType = Attacher::AttachEngine3D
  Height = 12
  Length = 12
  Placement = pos=(-3.8,-1.4,-2) rot=(0,0,1;0.349066rad)
  Width = 26
FEATURE [Part::Box] Box083  label="Krychle083"
  AttacherType = Attacher::AttachEngine3D
  Height = 7
  Length = 12
  Placement = pos=(4,-10,-2) rot=(0,0,1;0rad)
  Width = 18
FEATURE [Part::Box] Box084  label="Krychle084"
  AttacherType = Attacher::AttachEngine3D
  Height = 12
  Length = 12
  Placement = pos=(13.25,-5,-2) rot=(0,0,1;1.309rad)
  Width = 19
FEATURE [Part::Fillet] Fillet032
  Base = -> Box084
  Edges = 2 edges r=4: [Edge1,Edge5]
FEATURE [Part::Cylinder] Cylinder123  label="Válec123"
  Angle = 360
  AttacherType = Attacher::AttachEngine3D
  Height = 7
  Placement = pos=(-7,41,-2) rot=(0,0,1;0rad)
  Radius = 7
FEATURE [Part::Cut] Cut088
  Base = -> Cylinder123
  Tool = -> Cylinder119
FEATURE [Part::Cylinder] Cylinder124  label="Válec124"
  Angle = 360
  AttacherType = Attacher::AttachEngine3D
  Height = 7
  Placement = pos=(-7,41,5) rot=(0,0,1;0rad)
  Radius = 7
FEATURE [Part::Cut] Cut086
  Base = -> Box081
  Tool = -> Cylinder124
FEATURE [Part::Cut] Cut089
  Base = -> Cut086
  Tool = -> Cylinder120
FEATURE [Part::Cylinder] Cylinder125  label="Válec125"
  Angle = 360
  AttacherType = Attacher::AttachEngine3D
  Height = 10
  Placement = pos=(-9,23,1) rot=(0,0,1;0rad)
  Radius = 5
FEATURE [Part::Cylinder] Cylinder126  label="Válec126"
  Angle = 360
  AttacherType = Attacher::AttachEngine3D
  Height = 10
  Placement = pos=(-13,22,5) rot=(0,0,1;0rad)
  Radius = 10
FEATURE [Part::Cut] Cut090
  Base = -> Box082
  Tool = -> Cylinder126
FEATURE [Part::Cylinder] Cylinder127  label="Válec127"
  Angle = 360
  AttacherType = Attacher::AttachEngine3D
  Height = 10
  Placement = pos=(-13,22,5) rot=(0,0,1;0rad)
  Radius = 10
FEATURE [Part::Cut] Cut091
  Base = -> Cut089
  Tool = -> Cylinder127
FEATURE [Part::Cut] Cut093
  Base = -> Cut091
  Tool = -> Cylinder125
FEATURE [Part::Fillet] Fillet033
  Base = -> Cut093
  Edges = 1 edges r=4: [Edge10]
FEATURE [Part::Cylinder] Cylinder128  label="Válec128"
  Angle = 360
  AttacherType = Attacher::AttachEngine3D
  Height = 10
  Placement = pos=(-9,23,1) rot=(0,0,1;0rad)
  Radius = 5
FEATURE [Part::Cut] Cut092
  Base = -> Cut090
  Tool = -> Cylinder128
FEATURE [Part::Fillet] Fillet034
  Base = -> Cut092
  Edges = 1 edges r=6: [Edge2]
FEATURE [Part::Cylinder] Cylinder129  label="Válec129"
  Angle = 360
  AttacherType = Attacher::AttachEngine3D
  Height = 4
  Placement = pos=(10,-10,1) rot=(0,0,1;0rad)
  Radius = 5
FEATURE [Part::Cut] Cut094
  Base = -> Box083
  Placement = pos=(3,0,0) rot=(0,0,1;0rad)
  Tool = -> Cylinder129
FEATURE [Part::Fillet] Fillet031
  Base = -> Cut094
  Edges = 1 edges r=4: [Edge16]
  Placement = pos=(0,-1,0) rot=(0,0,1;0rad)
FEATURE [Part::Fillet] Fillet035
  Base = -> Fillet033
  Edges = 1 edges r=1: [Edge19]
FEATURE [Part::Cylinder] Cylinder130  label="Válec130"
  Angle = 360
  AttacherType = Attacher::AttachEngine3D
  Height = 7
  Placement = pos=(-10,23,-2) rot=(0,0,1;0rad)
  Radius = 8
FEATURE [Part::Cylinder] Cylinder131  label="Válec131"
  Angle = 360
  AttacherType = Attacher::AttachEngine3D
  Height = 10
  Placement = pos=(-13,22,1) rot=(0,0,1;0rad)
  Radius = 5
FEATURE [Part::Cut] Cut095
  Base = -> Cylinder130
  Tool = -> Cylinder131
FEATURE [Part::Cylinder] Cylinder132  label="Válec132"
  Angle = 360
  AttacherType = Attacher::AttachEngine3D
  Height = 10
  Placement = pos=(-13,22,1) rot=(0,0,1;0rad)
  Radius = 5
FEATURE [Part::Cut] Cut096
  Base = -> Fillet035
  Tool = -> Cylinder132
FEATURE [Part::Cylinder] Cylinder133  label="Válec133"
  Angle = 360
  AttacherType = Attacher::AttachEngine3D
  Height = 10
  Placement = pos=(-13,22,1) rot=(0,0,1;0rad)
  Radius = 5
FEATURE [Part::Cut] Cut097
  Base = -> Fillet034
  Tool = -> Cylinder133
FEATURE [Part::Fillet] Fillet036
  Base = -> Cut097
  Edges = 1 edges r=3: [Edge9]
FEATURE [Part::Fillet] Fillet037
  Base = -> Fillet032
  Edges = 1 edges r=3: [Edge4]
FEATURE [Part::Cylinder] Cylinder134  label="Válec134"
  Angle = 360
  AttacherType = Attacher::AttachEngine3D
  Height = 20
  Placement = pos=(1,14,4.01) rot=(0,0,1;0rad)
  Radius = 1.5
FEATURE [Part::Cylinder] Cylinder135  label="Válec135"
  Angle = 360
  AttacherType = Attacher::AttachEngine3D
  Height = 3
  Placement = pos=(1,14,-1.01) rot=(0,0,1;0rad)
  Radius = 1.5
FEATURE [Part::Box] Box085  label="Krychle085"
  AttacherType = Attacher::AttachEngine3D
  Height = 2
  Length = 6
  Placement = pos=(-2,11,2) rot=(0,0,1;0rad)
  Width = 6
FEATURE [Part::Cylinder] Cylinder136  label="Válec136"
  Angle = 360
  AttacherType = Attacher::AttachEngine3D
  Height = 20
  Placement = pos=(1,14,4.01) rot=(0,0,1;0rad)
  Radius = 1.5
FEATURE [Part::Cylinder] Cylinder137  label="Válec137"
  Angle = 360
  AttacherType = Attacher::AttachEngine3D
  Height = 3
  Placement = pos=(1,14,-1.01) rot=(0,0,1;0rad)
  Radius = 1.5
FEATURE [Part::Compound] Compound033
  Links = -> [Box085,Cylinder136,Cylinder137]
  Placement = pos=(-5,16,0) rot=(0,0,1;0rad)
FEATURE [Part::Cut] Cut103
  Base = -> Cut095
  Tool = -> Compound033
FEATURE [Part::Cylinder] Cylinder138  label="Válec138"
  Angle = 360
  AttacherType = Attacher::AttachEngine3D
  Height = 4
  Placement = pos=(1,14,-0.1) rot=(0,0,1;0rad)
  Radius = 1.5
FEATURE [Part::Cylinder] Cylinder139  label="Válec139"
  Angle = 360
  AttacherType = Attacher::AttachEngine3D
  Height = 12
  Placement = pos=(1,14,6) rot=(0,0,1;0rad)
  Radius = 1.5
FEATURE [Part::Cylinder] Cylinder140  label="Válec140"
  Angle = 360
  AttacherType = Attacher::AttachEngine3D
  Height = 12
  Placement = pos=(1,14,6) rot=(0,0,1;0rad)
  Radius = 1.5
FEATURE [Part::Box] Box086  label="Krychle086"
  AttacherType = Attacher::AttachEngine3D
  Height = 2
  Length = 6
  Placement = pos=(-2,11,4) rot=(0,0,1;0rad)
  Width = 6
FEATURE [Part::Box] Box087  label="Krychle087"
  AttacherType = Attacher::AttachEngine3D
  Height = 2
  Length = 6
  Placement = pos=(-2,11,4) rot=(0,0,1;0rad)
  Width = 6
FEATURE [Part::Cylinder] Cylinder141  label="Válec141"
  Angle = 360
  AttacherType = Attacher::AttachEngine3D
  Height = 4
  Placement = pos=(1,14,-0.1) rot=(0,0,1;0rad)
  Radius = 1.5
FEATURE [Part::Cylinder] Cylinder142  label="Válec142"
  Angle = 360
  AttacherType = Attacher::AttachEngine3D
  Height = 3
  Placement = pos=(1,14,-1.01) rot=(0,0,1;0rad)
  Radius = 1.5
FEATURE [Part::Box] Box088  label="Krychle088"
  AttacherType = Attacher::AttachEngine3D
  Height = 2
  Length = 6
  Placement = pos=(-2,11,2) rot=(0,0,1;0rad)
  Width = 6
FEATURE [Part::Cylinder] Cylinder143  label="Válec143"
  Angle = 360
  AttacherType = Attacher::AttachEngine3D
  Height = 20
  Placement = pos=(1,14,4.01) rot=(0,0,1;0rad)
  Radius = 1.5
FEATURE [Part::Cylinder] Cylinder144  label="Válec144"
  Angle = 360
  AttacherType = Attacher::AttachEngine3D
  Height = 3
  Placement = pos=(1,14,-1.01) rot=(0,0,1;0rad)
  Radius = 1.5
FEATURE [Part::Box] Box089  label="Krychle089"
  AttacherType = Attacher::AttachEngine3D
  Height = 2
  Length = 6
  Placement = pos=(-2,11,2) rot=(0,0,1;0rad)
  Width = 6
FEATURE [Part::Compound] Compound035
  Links = -> [Box087,Cylinder140,Cylinder141]
  Placement = pos=(6,-14,2) rot=(0,1,0;1.5708rad)
FEATURE [Part::Cut] Cut098
  Base = -> Fillet031
  Tool = -> Compound035
FEATURE [Part::Compound] Compound036
  Links = -> [Box086,Cylinder139,Cylinder138]
  Placement = pos=(6,-14,2) rot=(0,1,0;1.5708rad)
FEATURE [Part::Cut] Cut099
  Base = -> Fillet037
  Tool = -> Compound036
FEATURE [Part::Compound] Compound037
  Links = -> [Box088,Cylinder143,Cylinder142]
  Placement = pos=(-2.9,-11.9,0) rot=(0,0,-1;0.261799rad)
FEATURE [Part::Cut] Cut100
  Base = -> Cut099
  Tool = -> Compound037
FEATURE [Part::Box] Box090  label="Krychle090"
  AttacherType = Attacher::AttachEngine3D
  Height = 2
  Length = 6
  Placement = pos=(-2,11,2) rot=(0,0,1;0rad)
  Width = 6
FEATURE [Part::Compound] Compound034
  Links = -> [Box090,Cylinder134,Cylinder135]
  Placement = pos=(-5,16,0) rot=(0,0,1;0rad)
FEATURE [Part::Cut] Cut102
  Base = -> Cut096
  Tool = -> Compound034
FEATURE [Part::Cylinder] Cylinder145  label="Válec145"
  Angle = 360
  AttacherType = Attacher::AttachEngine3D
  Height = 20
  Placement = pos=(1,14,4.01) rot=(0,0,1;0rad)
  Radius = 1.5
FEATURE [Part::Compound] Compound038
  Links = -> [Box089,Cylinder145,Cylinder144]
  Placement = pos=(-2.9,-11.9,0) rot=(0,0,-1;0.261799rad)
FEATURE [Part::Cut] Cut101
  Base = -> Fillet036
  Tool = -> Compound038
FEATURE [Part::Compound] Compound039  label="Grip_finger-root_upper"
  Links = -> [Cut101,Cut100,Cut098,Cut103,Cut102,Cut088,Cut087]
FEATURE [Part::Box] Box1030  label="Krychle1029"
  AttacherType = Attacher::AttachEngine3D
  Height = 8
  Length = 12
  Placement = pos=(-10,-73,22) rot=(0,0,1;0rad)
  Width = 52
FEATURE [Part::Box] Box1031  label="Krychle1030"
  AttacherType = Attacher::AttachEngine3D
  Height = 8
  Length = 12
  Placement = pos=(-10,-73,-10) rot=(0,0,1;0rad)
  Width = 52
FEATURE [Part::Compound] Compound1289
  Links = -> [Box1030,Box1031]
FEATURE [Part::Box] Box1032  label="Krychle1031"
  AttacherType = Attacher::AttachEngine3D
  Height = 8
  Length = 12
  Placement = pos=(-5,-73,-10) rot=(0,0,1;0rad)
  Width = 52
FEATURE [Part::Box] Box1033  label="Krychle1032"
  AttacherType = Attacher::AttachEngine3D
  Height = 8
  Length = 12
  Placement = pos=(-5,-73,22) rot=(0,0,1;0rad)
  Width = 52
FEATURE [Part::Box] Box1036  label="Krychle1035"
  AttacherType = Attacher::AttachEngine3D
  Height = 6
  Length = 6
  Placement = pos=(-7,-41,24) rot=(0,0,1;0rad)
  Width = 2
FEATURE [Part::Box] Box1037  label="Krychle1036"
  AttacherType = Attacher::AttachEngine3D
  Height = 6
  Length = 6
  Placement = pos=(35,-41,24) rot=(0,0,1;0rad)
  Width = 2
FEATURE [Part::Box] Box1035  label="Krychle1034"
  AttacherType = Attacher::AttachEngine3D
  Height = 6
  Length = 6
  Placement = pos=(35,-41,-10) rot=(0,0,1;0rad)
  Width = 2
FEATURE [Part::Box] Box1034  label="Krychle1033"
  AttacherType = Attacher::AttachEngine3D
  Height = 6
  Length = 6
  Placement = pos=(-7,-41,-10) rot=(0,0,1;0rad)
  Width = 2
FEATURE [Part::Compound] Compound1290
  Links = -> [Box1033,Box1032]
  Placement = pos=(37,0,0) rot=(0,0,1;0rad)
FEATURE [Part::Compound] Compound1291
  Links = -> [Compound1289,Compound1290]
FEATURE [Part::Compound] Compound1292
  Links = -> [Box1034,Box1035,Box1036,Box1037]
  Placement = pos=(0,-200,0) rot=(0,0,1;0rad)
FEATURE [Part::Cylinder] Cylinder2937  label="Válec2907"
  Angle = 360
  AttacherType = Attacher::AttachEngine3D
  Height = 3
  Placement = pos=(39,-32,-7) rot=(1,0,0;1.5708rad)
  Radius = 3
FEATURE [Part::Cylinder] Cylinder2938  label="Válec2908"
  Angle = 360
  AttacherType = Attacher::AttachEngine3D
  Height = 50
  Placement = pos=(-5,-32,27) rot=(1,0,0;1.5708rad)
  Radius = 1.5
FEATURE [Part::Cylinder] Cylinder2939  label="Válec2909"
  Angle = 360
  AttacherType = Attacher::AttachEngine3D
  Height = 80
  Placement = pos=(-4,-32,-7) rot=(1,0,0;1.5708rad)
  Radius = 1.5
FEATURE [Part::Cylinder] Cylinder2940  label="Válec2910"
  Angle = 360
  AttacherType = Attacher::AttachEngine3D
  Height = 80
  Placement = pos=(38,-32,27) rot=(1,0,0;1.5708rad)
  Radius = 1.5
FEATURE [Part::Cylinder] Cylinder2941  label="Válec2911"
  Angle = 360
  AttacherType = Attacher::AttachEngine3D
  Height = 3
  Placement = pos=(-4,-70,27) rot=(1,0,0;1.5708rad)
  Radius = 3
FEATURE [Part::Cylinder] Cylinder2942  label="Válec2912"
  Angle = 360
  AttacherType = Attacher::AttachEngine3D
  Height = 3
  Placement = pos=(-4,-70,-7) rot=(1,0,0;1.5708rad)
  Radius = 3
FEATURE [Part::Cylinder] Cylinder2943  label="Válec2913"
  Angle = 360
  AttacherType = Attacher::AttachEngine3D
  Height = 80
  Placement = pos=(38,-32,-7) rot=(1,0,0;1.5708rad)
  Radius = 1.5
FEATURE [Part::Cylinder] Cylinder2944  label="Válec2914"
  Angle = 360
  AttacherType = Attacher::AttachEngine3D
  Height = 80
  Placement = pos=(-4,-32,27) rot=(1,0,0;1.5708rad)
  Radius = 1.5
FEATURE [Part::Compound] Compound1315
  Links = -> [Cylinder2944,Cylinder2939,Cylinder2940,Cylinder2943]
  Placement = pos=(0,20,0) rot=(0,0,1;0rad)
FEATURE [Part::Cylinder] Cylinder2945  label="Válec2915"
  Angle = 360
  AttacherType = Attacher::AttachEngine3D
  Height = 3
  Placement = pos=(38,-70,-7) rot=(1,0,0;1.5708rad)
  Radius = 3
FEATURE [Part::Cylinder] Cylinder2946  label="Válec2916"
  Angle = 360
  AttacherType = Attacher::AttachEngine3D
  Height = 3
  Placement = pos=(38,-70,27) rot=(1,0,0;1.5708rad)
  Radius = 3
FEATURE [Part::Compound] Compound1314
  Links = -> [Cylinder2945,Cylinder2946,Cylinder2941,Cylinder2942]
FEATURE [Part::Cylinder] Cylinder2883  label="Válec2853"
  Angle = 360
  AttacherType = Attacher::AttachEngine3D
  Height = 3
  Placement = pos=(33,-32,0) rot=(1,0,0;1.5708rad)
  Radius = 3
FEATURE [Part::Cylinder] Cylinder2884  label="Válec2854"
  Angle = 360
  AttacherType = Attacher::AttachEngine3D
  Height = 3
  Placement = pos=(33,-32,20) rot=(1,0,0;1.5708rad)
  Radius = 3
FEATURE [Part::Cylinder] Cylinder2885  label="Válec2855"
  Angle = 360
  AttacherType = Attacher::AttachEngine3D
  Height = 3
  Placement = pos=(1,-32,0) rot=(1,0,0;1.5708rad)
  Radius = 3
FEATURE [Part::Cylinder] Cylinder2886  label="Válec2856"
  Angle = 360
  AttacherType = Attacher::AttachEngine3D
  Height = 3
  Placement = pos=(1,-32,20) rot=(1,0,0;1.5708rad)
  Radius = 3
FEATURE [Part::Compound] Compound1293
  Links = -> [Cylinder2886,Cylinder2885,Cylinder2884,Cylinder2883]
  Placement = pos=(0,17,0) rot=(0,0,1;0rad)
FEATURE [Part::Box] Box1038  label="Krychle1037"
  AttacherType = Attacher::AttachEngine3D
  Height = 6
  Length = 54
  Placement = pos=(-10,-25,24) rot=(0,0,1;0rad)
  Width = 10
FEATURE [Part::Box] Box1039  label="Krychle1038"
  AttacherType = Attacher::AttachEngine3D
  Height = 6
  Length = 54
  Placement = pos=(-10,-25,-10) rot=(0,0,1;0rad)
  Width = 10
FEATURE [Part::Compound] Compound1298
  Links = -> [Box1038,Box1039]
FEATURE [Part::Cylinder] Cylinder2887  label="Válec2857"
  Angle = 360
  AttacherType = Attacher::AttachEngine3D
  Height = 50
  Placement = pos=(1,-32,20) rot=(1,0,0;1.5708rad)
  Radius = 1.5
FEATURE [Part::Cylinder] Cylinder2888  label="Válec2858"
  Angle = 360
  AttacherType = Attacher::AttachEngine3D
  Height = 50
  Placement = pos=(1,-32,0) rot=(1,0,0;1.5708rad)
  Radius = 1.5
FEATURE [Part::Cylinder] Cylinder2889  label="Válec2859"
  Angle = 360
  AttacherType = Attacher::AttachEngine3D
  Height = 50
  Placement = pos=(33,-32,20) rot=(1,0,0;1.5708rad)
  Radius = 1.5
FEATURE [Part::Cylinder] Cylinder2890  label="Válec2860"
  Angle = 360
  AttacherType = Attacher::AttachEngine3D
  Height = 50
  Placement = pos=(33,-32,0) rot=(1,0,0;1.5708rad)
  Radius = 1.5
FEATURE [Part::Compound] Compound1294
  Links = -> [Cylinder2887,Cylinder2888,Cylinder2889,Cylinder2890]
  Placement = pos=(0,20,0) rot=(0,0,1;0rad)
FEATURE [Part::Cut] Cut1096
  Base = -> Compound1291
  Tool = -> Compound1294
FEATURE [Part::Cut] Cut1102
  Base = -> Cut1096
  Tool = -> Compound1292
FEATURE [Part::Cut] Cut1103
  Base = -> Cut1102
  Tool = -> Compound1293
FEATURE [Part::Cylinder] Cylinder2891  label="Válec2861"
  Angle = 360
  AttacherType = Attacher::AttachEngine3D
  Height = 80
  Placement = pos=(38,-32,-7) rot=(1,0,0;1.5708rad)
  Radius = 1.5
FEATURE [Part::Cylinder] Cylinder2892  label="Válec2862"
  Angle = 360
  AttacherType = Attacher::AttachEngine3D
  Height = 80
  Placement = pos=(-4,-32,27) rot=(1,0,0;1.5708rad)
  Radius = 1.5
FEATURE [Part::Cylinder] Cylinder2893  label="Válec2863"
  Angle = 360
  AttacherType = Attacher::AttachEngine3D
  Height = 80
  Placement = pos=(-4,-32,-7) rot=(1,0,0;1.5708rad)
  Radius = 1.5
FEATURE [Part::Cylinder] Cylinder2894  label="Válec2864"
  Angle = 360
  AttacherType = Attacher::AttachEngine3D
  Height = 80
  Placement = pos=(38,-32,27) rot=(1,0,0;1.5708rad)
  Radius = 1.5
FEATURE [Part::Compound] Compound1295
  Links = -> [Cylinder2892,Cylinder2893,Cylinder2894,Cylinder2891]
  Placement = pos=(0,20,0) rot=(0,0,1;0rad)
FEATURE [Part::Cut] Cut1095
  Base = -> Cut1103
  Tool = -> Compound1295
FEATURE [Part::Cylinder] Cylinder2895  label="Válec2865"
  Angle = 360
  AttacherType = Attacher::AttachEngine3D
  Height = 3
  Placement = pos=(38,-32,27) rot=(1,0,0;1.5708rad)
  Radius = 3
FEATURE [Part::Cylinder] Cylinder2896  label="Válec2866"
  Angle = 360
  AttacherType = Attacher::AttachEngine3D
  Height = 3
  Placement = pos=(-4,-32,-7) rot=(1,0,0;1.5708rad)
  Radius = 3
FEATURE [Part::Cylinder] Cylinder2897  label="Válec2867"
  Angle = 360
  AttacherType = Attacher::AttachEngine3D
  Height = 3
  Placement = pos=(-4,-32,27) rot=(1,0,0;1.5708rad)
  Radius = 3
FEATURE [Part::Cylinder] Cylinder2898  label="Válec2868"
  Angle = 360
  AttacherType = Attacher::AttachEngine3D
  Height = 3
  Placement = pos=(38,-32,-7) rot=(1,0,0;1.5708rad)
  Radius = 3
FEATURE [Part::Compound] Compound1296
  Links = -> [Cylinder2897,Cylinder2896,Cylinder2895,Cylinder2898]
  Placement = pos=(0,17,0) rot=(0,0,1;0rad)
FEATURE [Part::Cylinder] Cylinder2899  label="Válec2869"
  Angle = 360
  AttacherType = Attacher::AttachEngine3D
  Height = 50
  Placement = pos=(38,-32,-7) rot=(1,0,0;1.5708rad)
  Radius = 1.5
FEATURE [Part::Cylinder] Cylinder2900  label="Válec2870"
  Angle = 360
  AttacherType = Attacher::AttachEngine3D
  Height = 50
  Placement = pos=(-4,-32,27) rot=(1,0,0;1.5708rad)
  Radius = 1.5
FEATURE [Part::Cylinder] Cylinder2901  label="Válec2871"
  Angle = 360
  AttacherType = Attacher::AttachEngine3D
  Height = 50
  Placement = pos=(-4,-32,-7) rot=(1,0,0;1.5708rad)
  Radius = 1.5
FEATURE [Part::Cylinder] Cylinder2902  label="Válec2872"
  Angle = 360
  AttacherType = Attacher::AttachEngine3D
  Height = 50
  Placement = pos=(38,-32,27) rot=(1,0,0;1.5708rad)
  Radius = 1.5
FEATURE [Part::Compound] Compound1297
  Links = -> [Cylinder2900,Cylinder2901,Cylinder2902,Cylinder2899]
  Placement = pos=(0,20,0) rot=(0,0,1;0rad)
FEATURE [Part::Cut] Cut1097
  Base = -> Compound1298
  Tool = -> Compound1297
FEATURE [Part::Cut] Cut1104
  Base = -> Cut1097
  Tool = -> Compound1296
FEATURE [Part::Chamfer] Chamfer169
  Base = -> Cut1104
  Edges = 2 edges r=3: [Edge3,Edge43]
FEATURE [Part::Chamfer] Chamfer170
  Base = -> Chamfer169
  Edges = 2 edges r=3: [Edge28,Edge73]
FEATURE [Part::Cylinder] Cylinder2903  label="Válec2873"
  Angle = 360
  AttacherType = Attacher::AttachEngine3D
  Height = 6
  Placement = pos=(21,23,-28) rot=(0,0,1;0rad)
  Radius = 3
FEATURE [Part::Cylinder] Cylinder2904  label="Válec2874"
  Angle = 360
  AttacherType = Attacher::AttachEngine3D
  Height = 6
  Placement = pos=(-21,23,-28) rot=(0,0,1;0rad)
  Radius = 3
FEATURE [Part::Cylinder] Cylinder2905  label="Válec2875"
  Angle = 360
  AttacherType = Attacher::AttachEngine3D
  Height = 6
  Placement = pos=(21,-23,-28) rot=(0,0,1;0rad)
  Radius = 3
FEATURE [Part::Cylinder] Cylinder2906  label="Válec2876"
  Angle = 360
  AttacherType = Attacher::AttachEngine3D
  Height = 6
  Placement = pos=(-21,-23,-28) rot=(0,0,1;0rad)
  Radius = 3
FEATURE [Part::Compound] Compound1299
  Links = -> [Cylinder2906,Cylinder2903,Cylinder2904,Cylinder2905]
  Placement = pos=(17,-91,10) rot=(1,0,0;1.5708rad)
FEATURE [Part::Box] Box1040  label="Krychle1039"
  AttacherType = Attacher::AttachEngine3D
  Height = 10
  Length = 12
  Placement = pos=(-10,-73,-16) rot=(0,0,1;0rad)
  Width = 4
FEATURE [Part::Box] Box1041  label="Krychle1040"
  AttacherType = Attacher::AttachEngine3D
  Height = 10
  Length = 12
  Placement = pos=(-10,-69,-16) rot=(0,0,1;0rad)
  Width = 6
FEATURE [Part::Chamfer] Chamfer171
  Base = -> Box1041
  Edges = 1 edges r=5.6: [Edge11]
FEATURE [Part::Compound] Compound1300
  Links = -> [Box1040,Chamfer171]
FEATURE [Part::Box] Box1042  label="Krychle1041"
  AttacherType = Attacher::AttachEngine3D
  Height = 10
  Length = 12
  Placement = pos=(-10,-73,-16) rot=(0,0,1;0rad)
  Width = 4
FEATURE [Part::Box] Box1043  label="Krychle1042"
  AttacherType = Attacher::AttachEngine3D
  Height = 10
  Length = 12
  Placement = pos=(-10,-69,-16) rot=(0,0,1;0rad)
  Width = 6
FEATURE [Part::Chamfer] Chamfer172
  Base = -> Box1043
  Edges = 1 edges r=5.6: [Edge11]
FEATURE [Part::Compound] Compound1301
  Links = -> [Box1042,Chamfer172]
  Placement = pos=(42,0,0) rot=(0,0,1;0rad)
FEATURE [Part::Box] Box1044  label="Krychle1043"
  AttacherType = Attacher::AttachEngine3D
  Height = 10
  Length = 12
  Placement = pos=(-10,-73,26) rot=(0,0,1;0rad)
  Width = 4
FEATURE [Part::Box] Box1045  label="Krychle1044"
  AttacherType = Attacher::AttachEngine3D
  Height = 10
  Length = 12
  Placement = pos=(-10,-69,26) rot=(0,0,1;0rad)
  Width = 6
FEATURE [Part::Chamfer] Chamfer173
  Base = -> Box1045
  Edges = 1 edges r=5.6: [Edge12]
FEATURE [Part::Compound] Compound1302
  Links = -> [Box1044,Chamfer173]
FEATURE [Part::Box] Box1046  label="Krychle1045"
  AttacherType = Attacher::AttachEngine3D
  Height = 10
  Length = 12
  Placement = pos=(-10,-69,26) rot=(0,0,1;0rad)
  Width = 6
FEATURE [Part::Chamfer] Chamfer174
  Base = -> Box1046
  Edges = 1 edges r=5.6: [Edge12]
FEATURE [Part::Box] Box1047  label="Krychle1046"
  AttacherType = Attacher::AttachEngine3D
  Height = 10
  Length = 12
  Placement = pos=(-10,-73,26) rot=(0,0,1;0rad)
  Width = 4
FEATURE [Part::Compound] Compound1303
  Links = -> [Box1047,Chamfer174]
  Placement = pos=(42,0,0) rot=(0,0,1;0rad)
FEATURE [Part::Compound] Compound1304
  Links = -> [Compound1300,Compound1303,Compound1302,Compound1301]
FEATURE [Part::Cut] Cut1094
  Base = -> Compound1304
  Tool = -> Compound1299
FEATURE [Part::Cylinder] Cylinder2907  label="Válec2877"
  Angle = 360
  AttacherType = Attacher::AttachEngine3D
  Height = 10
  Placement = pos=(21,23,-28) rot=(0,0,1;0rad)
  Radius = 1.5
FEATURE [Part::Cylinder] Cylinder2908  label="Válec2878"
  Angle = 360
  AttacherType = Attacher::AttachEngine3D
  Height = 10
  Placement = pos=(-21,23,-28) rot=(0,0,1;0rad)
  Radius = 1.5
FEATURE [Part::Cylinder] Cylinder2909  label="Válec2879"
  Angle = 360
  AttacherType = Attacher::AttachEngine3D
  Height = 10
  Placement = pos=(21,-23,-28) rot=(0,0,1;0rad)
  Radius = 1.5
FEATURE [Part::Cylinder] Cylinder2910  label="Válec2880"
  Angle = 360
  AttacherType = Attacher::AttachEngine3D
  Height = 10
  Placement = pos=(-21,-23,-28) rot=(0,0,1;0rad)
  Radius = 1.5
FEATURE [Part::Compound] Compound1305
  Links = -> [Cylinder2910,Cylinder2907,Cylinder2908,Cylinder2909]
  Placement = pos=(17,-95,10) rot=(1,0,0;1.5708rad)
FEATURE [Part::Cut] Cut1105
  Base = -> Cut1094
  Tool = -> Compound1305
FEATURE [Part::Cut] Cut1100
  Base = -> Cut1105
  Tool = -> Compound1314
FEATURE [Part::Cut] Cut1101
  Base = -> Cut1100
  Tool = -> Compound1315
FEATURE [Part::Chamfer] Chamfer046
  Base = -> Cut1101
  Edges = 1 edges r=2: [Edge37]
FEATURE [Part::Chamfer] Chamfer047
  Base = -> Chamfer046
  Edges = 1 edges r=2: [Edge177]
FEATURE [Part::Chamfer] Chamfer181
  Base = -> Chamfer047
  Edges = 2 edges r=2: [Edge164,Edge249]
FEATURE [Part::Cylinder] Cylinder2911  label="Válec2881"
  Angle = 360
  AttacherType = Attacher::AttachEngine3D
  Height = 3
  Placement = pos=(38,-32,-7) rot=(1,0,0;1.5708rad)
  Radius = 3
FEATURE [Part::Cylinder] Cylinder2912  label="Válec2882"
  Angle = 360
  AttacherType = Attacher::AttachEngine3D
  Height = 3
  Placement = pos=(38,-32,27) rot=(1,0,0;1.5708rad)
  Radius = 3
FEATURE [Part::Cylinder] Cylinder2913  label="Válec2883"
  Angle = 360
  AttacherType = Attacher::AttachEngine3D
  Height = 3
  Placement = pos=(-4,-32,27) rot=(1,0,0;1.5708rad)
  Radius = 3
FEATURE [Part::Cylinder] Cylinder2914  label="Válec2884"
  Angle = 360
  AttacherType = Attacher::AttachEngine3D
  Height = 3
  Placement = pos=(-4,-32,-7) rot=(1,0,0;1.5708rad)
  Radius = 3
FEATURE [Part::Compound] Compound1306
  Links = -> [Cylinder2913,Cylinder2914,Cylinder2912,Cylinder2911]
  Placement = pos=(0,-38,0) rot=(0,0,1;0rad)
FEATURE [Part::Cut] Cut1106
  Base = -> Cut1095
  Tool = -> Compound1306
FEATURE [Part::Chamfer] Chamfer180
  Base = -> Cut1106
  Edges = 2 edges r=2: [Edge56,Edge82]
FEATURE [Part::Chamfer] Chamfer044
  Base = -> Chamfer180
  Edges = 2 edges r=2: [Edge52,Edge76]
FEATURE [Part::Cylinder] Cylinder2915  label="Válec2885"
  Angle = 360
  AttacherType = Attacher::AttachEngine3D
  Height = 32
  Placement = pos=(7,-10,-6) rot=(0,0,1;0rad)
  Radius = 8
FEATURE [Part::Cylinder] Cylinder2916  label="Válec2886"
  Angle = 360
  AttacherType = Attacher::AttachEngine3D
  Height = 32
  Placement = pos=(27,-10,-6) rot=(0,0,1;0rad)
  Radius = 8
FEATURE [Part::Compound] Compound1307
  Links = -> [Cylinder2915,Cylinder2916]
FEATURE [Part::Cut] Cut1098
  Base = -> Chamfer170
  Tool = -> Compound1307
FEATURE [Part::Chamfer] Chamfer179
  Base = -> Cut1098
  Edges = 2 edges r=2: [Edge1,Edge77]
FEATURE [Part::Chamfer] Chamfer045
  Base = -> Chamfer179
  Edges = 2 edges r=2: [Edge6,Edge96]
FEATURE [Part::Cylinder] Cylinder2917  label="Válec2887"
  Angle = 360
  AttacherType = Attacher::AttachEngine3D
  Height = 20
  Placement = pos=(31,-10,10) rot=(1,0,0;1.5708rad)
  Radius = 1
FEATURE [Part::Box] Box1048  label="Krychle1047"
  AttacherType = Attacher::AttachEngine3D
  Height = 8
  Length = 54
  Placement = pos=(-10,-21,6) rot=(0,0,1;0rad)
  Width = 6
FEATURE [Part::Cylinder] Cylinder2918  label="Válec2888"
  Angle = 360
  AttacherType = Attacher::AttachEngine3D
  Height = 20
  Placement = pos=(3,-10,10) rot=(1,0,0;1.5708rad)
  Radius = 1
FEATURE [Part::Cylinder] Cylinder2919  label="Válec2889"
  Angle = 360
  AttacherType = Attacher::AttachEngine3D
  Height = 20
  Placement = pos=(17,-10,8) rot=(1,0,0;1.5708rad)
  Radius = 1
FEATURE [Part::Cylinder] Cylinder2920  label="Válec2890"
  Angle = 360
  AttacherType = Attacher::AttachEngine3D
  Height = 20
  Placement = pos=(17,-10,12) rot=(1,0,0;1.5708rad)
  Radius = 1
FEATURE [Part::Compound] Compound1309
  Links = -> [Cylinder2918,Cylinder2917,Cylinder2919,Cylinder2920]
FEATURE [Part::Cylinder] Cylinder2921  label="Válec2891"
  Angle = 360
  AttacherType = Attacher::AttachEngine3D
  Height = 2
  Placement = pos=(31,-10,10) rot=(1,0,0;1.5708rad)
  Radius = 2
FEATURE [Part::Cylinder] Cylinder2922  label="Válec2892"
  Angle = 360
  AttacherType = Attacher::AttachEngine3D
  Height = 2
  Placement = pos=(17,-10,12) rot=(1,0,0;1.5708rad)
  Radius = 2
FEATURE [Part::Cylinder] Cylinder2923  label="Válec2893"
  Angle = 360
  AttacherType = Attacher::AttachEngine3D
  Height = 2
  Placement = pos=(3,-10,10) rot=(1,0,0;1.5708rad)
  Radius = 2
FEATURE [Part::Cylinder] Cylinder2924  label="Válec2894"
  Angle = 360
  AttacherType = Attacher::AttachEngine3D
  Height = 2
  Placement = pos=(17,-10,8) rot=(1,0,0;1.5708rad)
  Radius = 2
FEATURE [Part::Compound] Compound1308
  Links = -> [Cylinder2923,Cylinder2921,Cylinder2924,Cylinder2922]
  Placement = pos=(0,-9,0) rot=(0,0,1;0rad)
FEATURE [Part::Cut] Cut1099
  Base = -> Box1048
  Tool = -> Compound1308
FEATURE [Part::Cut] Cut1107
  Base = -> Cut1099
  Tool = -> Compound1309
FEATURE [Part::Cylinder] Cylinder2925  label="Válec2895"
  Angle = 360
  AttacherType = Attacher::AttachEngine3D
  Height = 20
  Placement = pos=(-5,-17,10) rot=(1,0,0;1.5708rad)
  Radius = 2.65
FEATURE [Part::Cylinder] Cylinder2926  label="Válec2896"
  Angle = 360
  AttacherType = Attacher::AttachEngine3D
  Height = 20
  Placement = pos=(39,-17,10) rot=(1,0,0;1.5708rad)
  Radius = 2.65
FEATURE [Part::Compound] Compound1310
  Links = -> [Cylinder2925,Cylinder2926]
FEATURE [Part::Cut] Cut1108
  Base = -> Cut1107
  Tool = -> Compound1310
FEATURE [Part::Chamfer] Chamfer175
  Base = -> Cut1108
  Edges = 1 edges r=2: [Edge22]
FEATURE [Part::Chamfer] Chamfer177
  Base = -> Chamfer175
  Edges = 1 edges r=2: [Edge9]
FEATURE [Part::Box] Box1049  label="Krychle1048"
  AttacherType = Attacher::AttachEngine3D
  Height = 10
  Length = 54
  Placement = pos=(-10,-21,14) rot=(0,0,1;0rad)
  Width = 6
FEATURE [Part::Cylinder] Cylinder2927  label="Válec2897"
  Angle = 360
  AttacherType = Attacher::AttachEngine3D
  Height = 10
  Placement = pos=(27,-10,-4) rot=(0,0,1;0rad)
  Radius = 8
FEATURE [Part::Cylinder] Cylinder2928  label="Válec2898"
  Angle = 360
  AttacherType = Attacher::AttachEngine3D
  Height = 10
  Placement = pos=(7,-10,14) rot=(0,0,1;0rad)
  Radius = 8
FEATURE [Part::Cut] Cut1112
  Base = -> Box1049
  Tool = -> Cylinder2928
FEATURE [Part::Cylinder] Cylinder2929  label="Válec2899"
  Angle = 360
  AttacherType = Attacher::AttachEngine3D
  Height = 10
  Placement = pos=(7,-10,-4) rot=(0,0,1;0rad)
  Radius = 8
FEATURE [Part::Cylinder] Cylinder2930  label="Válec2900"
  Angle = 360
  AttacherType = Attacher::AttachEngine3D
  Height = 10
  Placement = pos=(27,-10,14) rot=(0,0,1;0rad)
  Radius = 8
FEATURE [Part::Cut] Cut1110
  Base = -> Cut1112
  Tool = -> Cylinder2930
FEATURE [Part::Box] Box1050  label="Krychle1049"
  AttacherType = Attacher::AttachEngine3D
  Height = 10
  Length = 54
  Placement = pos=(-10,-21,-4) rot=(0,0,1;0rad)
  Width = 6
FEATURE [Part::Cut] Cut1111
  Base = -> Box1050
  Tool = -> Cylinder2929
FEATURE [Part::Cut] Cut1109
  Base = -> Cut1111
  Tool = -> Cylinder2927
FEATURE [Part::Compound] Compound1313
  Links = -> [Cut1110,Cut1109]
FEATURE [Part::Cylinder] Cylinder2931  label="Válec2901"
  Angle = 360
  AttacherType = Attacher::AttachEngine3D
  Height = 50
  Placement = pos=(-5,-32,-7) rot=(1,0,0;1.5708rad)
  Radius = 1.5
FEATURE [Part::Cylinder] Cylinder2932  label="Válec2902"
  Angle = 360
  AttacherType = Attacher::AttachEngine3D
  Height = 3
  Placement = pos=(-5,-32,27) rot=(1,0,0;1.5708rad)
  Radius = 3
FEATURE [Part::Cylinder] Cylinder2933  label="Válec2903"
  Angle = 360
  AttacherType = Attacher::AttachEngine3D
  Height = 50
  Placement = pos=(39,-32,27) rot=(1,0,0;1.5708rad)
  Radius = 1.5
FEATURE [Part::Cylinder] Cylinder2934  label="Válec2904"
  Angle = 360
  AttacherType = Attacher::AttachEngine3D
  Height = 3
  Placement = pos=(-5,-32,-7) rot=(1,0,0;1.5708rad)
  Radius = 3
FEATURE [Part::Cylinder] Cylinder2935  label="Válec2905"
  Angle = 360
  AttacherType = Attacher::AttachEngine3D
  Height = 50
  Placement = pos=(39,-32,-7) rot=(1,0,0;1.5708rad)
  Radius = 1.5
FEATURE [Part::Compound] Compound1311
  Links = -> [Cylinder2938,Cylinder2931,Cylinder2933,Cylinder2935]
  Placement = pos=(0,20,0) rot=(0,0,1;0rad)
FEATURE [Part::Cut] Cut1114
  Base = -> Compound1313
  Tool = -> Compound1311
FEATURE [Part::Cylinder] Cylinder2936  label="Válec2906"
  Angle = 360
  AttacherType = Attacher::AttachEngine3D
  Height = 3
  Placement = pos=(39,-32,27) rot=(1,0,0;1.5708rad)
  Radius = 3
FEATURE [Part::Compound] Compound1312
  Links = -> [Cylinder2932,Cylinder2934,Cylinder2936,Cylinder2937]
  Placement = pos=(0,17,0) rot=(0,0,1;0rad)
FEATURE [Part::Cut] Cut1113
  Base = -> Cut1114
  Tool = -> Compound1312
FEATURE [Part::Chamfer] Chamfer176
  Base = -> Cut1113
  Edges = 2 edges r=2: [Edge25,Edge53]
FEATURE [Part::Chamfer] Chamfer178
  Base = -> Chamfer176
  Edges = 2 edges r=2: [Edge23,Edge57]
FEATURE [Part::Compound] Compound1316  label="Wrist_tabular-nuovo"
  Links = -> [Chamfer177,Chamfer178,Chamfer044,Chamfer045,Chamfer181]
FEATURE [Part::Cylinder] Cylinder242  label="Válec242"
  Angle = 360
  AttacherType = Attacher::AttachEngine3D
  Height = 10
  Placement = pos=(17,-24,10) rot=(1,0,0;1.5708rad)
  Radius = 11
FEATURE [Part::Cylinder] Cylinder243  label="Válec243"
  Angle = 360
  AttacherType = Attacher::AttachEngine3D
  Height = 5
  Placement = pos=(55,-25.5,15) rot=(0,0,1;0rad)
  Radius = 8.5
FEATURE [Part::Cylinder] Cylinder244  label="Válec244"
  Angle = 360
  AttacherType = Attacher::AttachEngine3D
  Height = 5
  Placement = pos=(-21,-25.5,15) rot=(0,0,1;0rad)
  Radius = 8.5
FEATURE [Part::Cylinder] Cylinder245  label="Válec245"
  Angle = 360
  AttacherType = Attacher::AttachEngine3D
  Height = 4
  Placement = pos=(-21,-25.5,15) rot=(0,0,1;0rad)
  Radius = 5
FEATURE [Part::Box] Box174  label="Krychle174"
  AttacherType = Attacher::AttachEngine3D
  Height = 5
  Length = 76
  Placement = pos=(-21,-34,15) rot=(0,0,1;0rad)
  Width = 17
FEATURE [Part::Cut] Cut147
  Base = -> Cylinder244
  Tool = -> Cylinder245
FEATURE [Part::Box] Box175  label="Krychle175"
  AttacherType = Attacher::AttachEngine3D
  Height = 5
  Length = 56
  Placement = pos=(-11,-34,10) rot=(0,0,1;0rad)
  Width = 17
FEATURE [Part::Cylinder] Cylinder246  label="Válec246"
  Angle = 360
  AttacherType = Attacher::AttachEngine3D
  Height = 20
  Placement = pos=(-5,-17,10) rot=(1,0,0;1.5708rad)
  Radius = 5
FEATURE [Part::Cylinder] Cylinder247  label="Válec247"
  Angle = 360
  AttacherType = Attacher::AttachEngine3D
  Height = 20
  Placement = pos=(39,-17,10) rot=(1,0,0;1.5708rad)
  Radius = 5
FEATURE [Part::Compound] Compound105
  Links = -> [Cylinder246,Cylinder247]
FEATURE [Part::Cylinder] Cylinder248  label="Válec248"
  Angle = 360
  AttacherType = Attacher::AttachEngine3D
  Height = 17
  Placement = pos=(-5,-17,10) rot=(1,0,0;1.5708rad)
  Radius = 7
FEATURE [Part::Cylinder] Cylinder249  label="Válec249"
  Angle = 360
  AttacherType = Attacher::AttachEngine3D
  Height = 17
  Placement = pos=(39,-17,10) rot=(1,0,0;1.5708rad)
  Radius = 7
FEATURE [Part::Compound] Compound111
  Links = -> [Cylinder248,Cylinder249]
FEATURE [Part::Cylinder] Cylinder250  label="Válec250"
  Angle = 360
  AttacherType = Attacher::AttachEngine3D
  Height = 4
  Placement = pos=(55,-25.5,15) rot=(0,0,1;0rad)
  Radius = 5
FEATURE [Part::Cut] Cut148
  Base = -> Cylinder243
  Tool = -> Cylinder250
FEATURE [Part::Cylinder] Cylinder251  label="Válec251"
  Angle = 360
  AttacherType = Attacher::AttachEngine3D
  Height = 4
  Placement = pos=(55,-25.5,15) rot=(0,0,1;0rad)
  Radius = 5
FEATURE [Part::Cylinder] Cylinder252  label="Válec252"
  Angle = 360
  AttacherType = Attacher::AttachEngine3D
  Height = 20
  Placement = pos=(-5,-17,10) rot=(1,0,0;1.5708rad)
  Radius = 5
FEATURE [Part::Cylinder] Cylinder253  label="Válec253"
  Angle = 360
  AttacherType = Attacher::AttachEngine3D
  Height = 4
  Placement = pos=(-21,-25.5,15) rot=(0,0,1;0rad)
  Radius = 5
FEATURE [Part::Cylinder] Cylinder254  label="Válec254"
  Angle = 360
  AttacherType = Attacher::AttachEngine3D
  Height = 10
  Placement = pos=(31,-20,9) rot=(0,0,1;0rad)
  Radius = 1.5
FEATURE [Part::Box] Box176  label="Krychle176"
  AttacherType = Attacher::AttachEngine3D
  Height = 2
  Length = 6
  Placement = pos=(0,-23,13) rot=(0,0,1;0rad)
  Width = 6
FEATURE [Part::Box] Box177  label="Krychle177"
  AttacherType = Attacher::AttachEngine3D
  Height = 10
  Length = 80
  Placement = pos=(-20,-36,0) rot=(0,0,1;0rad)
  Width = 20
FEATURE [Part::Cylinder] Cylinder255  label="Válec255"
  Angle = 360
  AttacherType = Attacher::AttachEngine3D
  Height = 10
  Placement = pos=(3,-20,9) rot=(0,0,1;0rad)
  Radius = 1.5
FEATURE [Part::Cylinder] Cylinder256  label="Válec256"
  Angle = 360
  AttacherType = Attacher::AttachEngine3D
  Height = 10
  Placement = pos=(31,-20,9) rot=(0,0,1;0rad)
  Radius = 1.5
FEATURE [Part::Cylinder] Cylinder257  label="Válec257"
  Angle = 360
  AttacherType = Attacher::AttachEngine3D
  Height = 10
  Placement = pos=(3,-31,9) rot=(0,0,1;0rad)
  Radius = 1.5
FEATURE [Part::Cylinder] Cylinder258  label="Válec258"
  Angle = 360
  AttacherType = Attacher::AttachEngine3D
  Height = 10
  Placement = pos=(31,-20,9) rot=(0,0,1;0rad)
  Radius = 1.5
FEATURE [Part::Cylinder] Cylinder259  label="Válec259"
  Angle = 360
  AttacherType = Attacher::AttachEngine3D
  Height = 10
  Placement = pos=(3,-31,9) rot=(0,0,1;0rad)
  Radius = 1.5
FEATURE [Part::Cylinder] Cylinder260  label="Válec260"
  Angle = 360
  AttacherType = Attacher::AttachEngine3D
  Height = 20
  Placement = pos=(-5,-17,10) rot=(1,0,0;1.5708rad)
  Radius = 5
FEATURE [Part::Cylinder] Cylinder261  label="Válec261"
  Angle = 360
  AttacherType = Attacher::AttachEngine3D
  Height = 10
  Placement = pos=(3,-31,9) rot=(0,0,1;0rad)
  Radius = 1.5
FEATURE [Part::Cylinder] Cylinder262  label="Válec262"
  Angle = 360
  AttacherType = Attacher::AttachEngine3D
  Height = 10
  Placement = pos=(31,-31,9) rot=(0,0,1;0rad)
  Radius = 1.5
FEATURE [Part::Compound] Compound110
  Links = -> [Cylinder255,Cylinder261,Cylinder254,Cylinder262]
FEATURE [Part::Box] Box178  label="Krychle178"
  AttacherType = Attacher::AttachEngine3D
  Height = 5
  Length = 4
  Placement = pos=(42,-34,10) rot=(0,0,1;0rad)
  Width = 17
FEATURE [Part::Box] Box179  label="Krychle179"
  AttacherType = Attacher::AttachEngine3D
  Height = 10
  Length = 80
  Placement = pos=(-20,-36,0) rot=(0,0,1;0rad)
  Width = 20
FEATURE [Part::Box] Box180  label="Krychle180"
  AttacherType = Attacher::AttachEngine3D
  Height = 5
  Length = 4
  Placement = pos=(-12,-34,10) rot=(0,0,1;0rad)
  Width = 17
FEATURE [Part::Compound] Compound107
  Links = -> [Box180,Box178]
FEATURE [Part::Cylinder] Cylinder263  label="Válec263"
  Angle = 360
  AttacherType = Attacher::AttachEngine3D
  Height = 20
  Placement = pos=(39,-17,10) rot=(1,0,0;1.5708rad)
  Radius = 5
FEATURE [Part::Compound] Compound106
  Links = -> [Cylinder252,Cylinder263]
FEATURE [Part::Cylinder] Cylinder264  label="Válec264"
  Angle = 360
  AttacherType = Attacher::AttachEngine3D
  Height = 20
  Placement = pos=(39,-17,10) rot=(1,0,0;1.5708rad)
  Radius = 5
FEATURE [Part::Compound] Compound112
  Links = -> [Cylinder260,Cylinder264]
FEATURE [Part::Box] Box181  label="Krychle181"
  AttacherType = Attacher::AttachEngine3D
  Height = 2
  Length = 6
  Placement = pos=(28,-34,13) rot=(0,0,1;0rad)
  Width = 6
FEATURE [Part::Box] Box182  label="Krychle182"
  AttacherType = Attacher::AttachEngine3D
  Height = 2
  Length = 6
  Placement = pos=(26,-23,13) rot=(0,0,1;0rad)
  Width = 6
FEATURE [Part::Cylinder] Cylinder265  label="Válec265"
  Angle = 360
  AttacherType = Attacher::AttachEngine3D
  Height = 10
  Placement = pos=(3,-20,9) rot=(0,0,1;0rad)
  Radius = 1.5
FEATURE [Part::Box] Box183  label="Krychle183"
  AttacherType = Attacher::AttachEngine3D
  Height = 2
  Length = 6
  Placement = pos=(0,-34,13) rot=(0,0,1;0rad)
  Width = 6
FEATURE [Part::Compound] Compound109
  Links = -> [Box183,Box176,Box181,Box182]
  Placement = pos=(0,-100,0) rot=(0,0,1;0rad)
FEATURE [Part::Cylinder] Cylinder266  label="Válec266"
  Angle = 360
  AttacherType = Attacher::AttachEngine3D
  Height = 10
  Placement = pos=(31,-31,9) rot=(0,0,1;0rad)
  Radius = 1.5
FEATURE [Part::Compound] Compound113
  Links = -> [Cylinder265,Cylinder259,Cylinder256,Cylinder266]
FEATURE [Part::Cylinder] Cylinder267  label="Válec267"
  Angle = 360
  AttacherType = Attacher::AttachEngine3D
  Height = 10
  Placement = pos=(3,-20,9) rot=(0,0,1;0rad)
  Radius = 1.5
FEATURE [Part::Box] Box184  label="Krychle184"
  AttacherType = Attacher::AttachEngine3D
  Height = 2
  Length = 6
  Placement = pos=(0,-23,13) rot=(0,0,1;0rad)
  Width = 6
FEATURE [Part::Box] Box185  label="Krychle185"
  AttacherType = Attacher::AttachEngine3D
  Height = 2
  Length = 6
  Placement = pos=(28,-34,13) rot=(0,0,1;0rad)
  Width = 6
FEATURE [Part::Cut] Cut150
  Base = -> Compound111
  Tool = -> Compound105
FEATURE [Part::Cut] Cut151
  Base = -> Box175
  Tool = -> Compound106
FEATURE [Part::Cut] Cut152
  Base = -> Cut150
  Tool = -> Box179
FEATURE [Part::Cut] Cut153
  Base = -> Box174
  Tool = -> Cylinder253
FEATURE [Part::Cut] Cut149
  Base = -> Cut153
  Tool = -> Cylinder251
FEATURE [Part::Cut] Cut156
  Base = -> Cut149
  Tool = -> Compound110
FEATURE [Part::Cut] Cut157
  Base = -> Compound107
  Tool = -> Compound112
FEATURE [Part::FeaturePython] Tube008  # WARN: FeaturePython — macro-defined, semantics opaque (R4)
  AttacherType = Attacher::AttachEngine3D
  Height = 1
  InnerRadius = 3
  OuterRadius = 5
  Placement = pos=(-5,-33,10) rot=(1,0,0;1.5708rad)
FEATURE [Part::FeaturePython] Tube009  # WARN: FeaturePython — macro-defined, semantics opaque (R4)
  AttacherType = Attacher::AttachEngine3D
  Height = 1
  InnerRadius = 3
  OuterRadius = 5
  Placement = pos=(39,-17,10) rot=(1,0,0;1.5708rad)
FEATURE [Part::FeaturePython] Tube010  # WARN: FeaturePython — macro-defined, semantics opaque (R4)
  AttacherType = Attacher::AttachEngine3D
  Height = 1
  InnerRadius = 3
  OuterRadius = 5
  Placement = pos=(39,-33,10) rot=(1,0,0;1.5708rad)
FEATURE [Part::FeaturePython] Tube011  # WARN: FeaturePython — macro-defined, semantics opaque (R4)
  AttacherType = Attacher::AttachEngine3D
  Height = 1
  InnerRadius = 3
  OuterRadius = 5
  Placement = pos=(-5,-17,10) rot=(1,0,0;1.5708rad)
FEATURE [Part::Compound] Compound108
  Links = -> [Tube011,Tube008,Tube009,Tube010]
FEATURE [Part::Cut] Cut158
  Base = -> Compound108
  Tool = -> Box177
FEATURE [Part::Box] Box186  label="Krychle186"
  AttacherType = Attacher::AttachEngine3D
  Height = 2
  Length = 6
  Placement = pos=(26,-23,13) rot=(0,0,1;0rad)
  Width = 6
FEATURE [Part::Cylinder] Cylinder268  label="Válec268"
  Angle = 360
  AttacherType = Attacher::AttachEngine3D
  Height = 10
  Placement = pos=(31,-31,9) rot=(0,0,1;0rad)
  Radius = 1.5
FEATURE [Part::Compound] Compound115
  Links = -> [Cylinder267,Cylinder257,Cylinder258,Cylinder268]
FEATURE [Part::Box] Box187  label="Krychle187"
  AttacherType = Attacher::AttachEngine3D
  Height = 2
  Length = 6
  Placement = pos=(0,-34,13) rot=(0,0,1;0rad)
  Width = 6
FEATURE [Part::Compound] Compound114
  Links = -> [Box187,Box184,Box185,Box186]
  Placement = pos=(0,-100,0) rot=(0,0,1;0rad)
FEATURE [Part::Box] Box188  label="Krychle188"
  AttacherType = Attacher::AttachEngine3D
  Height = 8
  Length = 6
  Placement = pos=(8.5,-21,12) rot=(0,0,1;0rad)
  Width = 2
FEATURE [Part::Cylinder] Cylinder269  label="Válec269"
  Angle = 360
  AttacherType = Attacher::AttachEngine3D
  Height = 30
  Placement = pos=(22.5,-19,15.5) rot=(1,0,0;1.5708rad)
  Radius = 1.5
FEATURE [Part::Box] Box189  label="Krychle189"
  AttacherType = Attacher::AttachEngine3D
  Height = 8
  Length = 6
  Placement = pos=(19.5,-21,1) rot=(0,0,1;0rad)
  Width = 2
FEATURE [Part::Box] Box190  label="Krychle190"
  AttacherType = Attacher::AttachEngine3D
  Height = 8
  Length = 6
  Placement = pos=(8.5,-21,12) rot=(0,0,1;0rad)
  Width = 2
FEATURE [Part::Box] Box191  label="Krychle191"
  AttacherType = Attacher::AttachEngine3D
  Height = 8
  Length = 6
  Placement = pos=(19.5,-21,12) rot=(0,0,1;0rad)
  Width = 2
FEATURE [Part::Cylinder] Cylinder270  label="Válec270"
  Angle = 360
  AttacherType = Attacher::AttachEngine3D
  Height = 30
  Placement = pos=(22.5,-19,4.5) rot=(1,0,0;1.5708rad)
  Radius = 1.5
FEATURE [Part::Cylinder] Cylinder271  label="Válec271"
  Angle = 360
  AttacherType = Attacher::AttachEngine3D
  Height = 30
  Placement = pos=(11.5,-19,4.5) rot=(1,0,0;1.5708rad)
  Radius = 1.5
FEATURE [Part::Box] Box192  label="Krychle192"
  AttacherType = Attacher::AttachEngine3D
  Height = 8
  Length = 6
  Placement = pos=(19.5,-21,12) rot=(0,0,1;0rad)
  Width = 2
FEATURE [Part::Cylinder] Cylinder272  label="Válec272"
  Angle = 360
  AttacherType = Attacher::AttachEngine3D
  Height = 10
  Placement = pos=(17,-24,10) rot=(1,0,0;1.5708rad)
  Radius = 11
FEATURE [Part::Cylinder] Cylinder273  label="Válec273"
  Angle = 360
  AttacherType = Attacher::AttachEngine3D
  Height = 30
  Placement = pos=(11.5,-19,4.5) rot=(1,0,0;1.5708rad)
  Radius = 1.5
FEATURE [Part::Cylinder] Cylinder274  label="Válec274"
  Angle = 360
  AttacherType = Attacher::AttachEngine3D
  Height = 30
  Placement = pos=(11.5,-19,15.5) rot=(1,0,0;1.5708rad)
  Radius = 1.5
FEATURE [Part::Compound] Compound116
  Links = -> [Cylinder273,Cylinder270,Cylinder274,Cylinder269]
  Placement = pos=(0,9,0) rot=(0,0,1;0rad)
FEATURE [Part::Box] Box193  label="Krychle193"
  AttacherType = Attacher::AttachEngine3D
  Height = 8
  Length = 6
  Placement = pos=(19.5,-21,1) rot=(0,0,1;0rad)
  Width = 2
FEATURE [Part::Cylinder] Cylinder275  label="Válec275"
  Angle = 360
  AttacherType = Attacher::AttachEngine3D
  Height = 30
  Placement = pos=(11.5,-19,15.5) rot=(1,0,0;1.5708rad)
  Radius = 1.5
FEATURE [Part::Cylinder] Cylinder276  label="Válec276"
  Angle = 360
  AttacherType = Attacher::AttachEngine3D
  Height = 30
  Placement = pos=(22.5,-19,4.5) rot=(1,0,0;1.5708rad)
  Radius = 1.5
FEATURE [Part::Box] Box194  label="Krychle194"
  AttacherType = Attacher::AttachEngine3D
  Height = 8
  Length = 6
  Placement = pos=(8.5,-21,1) rot=(0,0,1;0rad)
  Width = 2
FEATURE [Part::Compound] Compound118
  Links = -> [Box188,Box191,Box194,Box193]
FEATURE [Part::Cylinder] Cylinder277  label="Válec277"
  Angle = 360
  AttacherType = Attacher::AttachEngine3D
  Height = 30
  Placement = pos=(22.5,-19,15.5) rot=(1,0,0;1.5708rad)
  Radius = 1.5
FEATURE [Part::Compound] Compound117
  Links = -> [Cylinder271,Cylinder276,Cylinder275,Cylinder277]
  Placement = pos=(0,9,0) rot=(0,0,1;0rad)
FEATURE [Part::Box] Box195  label="Krychle195"
  AttacherType = Attacher::AttachEngine3D
  Height = 8
  Length = 6
  Placement = pos=(8.5,-21,1) rot=(0,0,1;0rad)
  Width = 2
FEATURE [Part::Cylinder] Cylinder278  label="Válec278"
  Angle = 360
  AttacherType = Attacher::AttachEngine3D
  Height = 3
  Placement = pos=(31,-20,9) rot=(0,0,1;0rad)
  Radius = 3
FEATURE [Part::Cylinder] Cylinder279  label="Válec279"
  Angle = 360
  AttacherType = Attacher::AttachEngine3D
  Height = 3
  Placement = pos=(3,-31,9) rot=(0,0,1;0rad)
  Radius = 3
FEATURE [Part::Cylinder] Cylinder280  label="Válec280"
  Angle = 360
  AttacherType = Attacher::AttachEngine3D
  Height = 3
  Placement = pos=(3,-20,9) rot=(0,0,1;0rad)
  Radius = 3
FEATURE [Part::Cylinder] Cylinder281  label="Válec281"
  Angle = 360
  AttacherType = Attacher::AttachEngine3D
  Height = 3
  Placement = pos=(31,-31,9) rot=(0,0,1;0rad)
  Radius = 3
FEATURE [Part::Cylinder] Cylinder283  label="Válec283"
  Angle = 360
  AttacherType = Attacher::AttachEngine3D
  Height = 20
  Placement = pos=(17,-14,10) rot=(1,0,0;1.5708rad)
  Radius = 5
FEATURE [Part::Cylinder] Cylinder286  label="Válec286"
  Angle = 360
  AttacherType = Attacher::AttachEngine3D
  Height = 2
  Placement = pos=(17,-22,10) rot=(1,0,0;1.5708rad)
  Radius = 5.25
FEATURE [Part::Cylinder] Cylinder287  label="Válec287"
  Angle = 360
  AttacherType = Attacher::AttachEngine3D
  Height = 2
  Placement = pos=(17,-22,10) rot=(1,0,0;1.5708rad)
  Radius = 5.25
FEATURE [Part::Cut] Cut159
  Base = -> Cut152
  Tool = -> Compound115
FEATURE [Part::Cut] Cut154
  Base = -> Cut159
  Tool = -> Compound114
FEATURE [Part::Cut] Cut160
  Base = -> Cut151
  Tool = -> Compound113
FEATURE [Part::Cut] Cut155
  Base = -> Cut160
  Tool = -> Compound109
FEATURE [Part::Cut] Cut166
  Base = -> Cut155
  Tool = -> Cylinder242
FEATURE [Part::Cut] Cut161
  Base = -> Cut166
  Tool = -> Compound118
FEATURE [Part::Cut] Cut165
  Base = -> Cut161
  Tool = -> Compound116
FEATURE [Part::Cut] Cut163
  Base = -> Cut156
  Tool = -> Cylinder272
FEATURE [Part::Cut] Cut164
  Base = -> Cut163
  Tool = -> Compound117
FEATURE [Part::Compound] Compound120
  Links = -> [Box190,Box192,Box195,Box189]
FEATURE [Part::Cut] Cut162
  Base = -> Cut164
  Tool = -> Compound120
FEATURE [Part::Compound] Compound121
  Links = -> [Cylinder280,Cylinder279,Cylinder278,Cylinder281]
  Placement = pos=(0,0,8) rot=(0,0,1;0rad)
FEATURE [Part::Cut] Cut171
  Base = -> Cut162
  Tool = -> Compound121
FEATURE [Part::Cut] Cut172
  Base = -> Cut165
  Tool = -> Cylinder283
FEATURE [Part::Cut] Cut173
  Base = -> Cut172
  Tool = -> Cylinder287
FEATURE [Part::Cut] Cut174
  Base = -> Cut171
  Tool = -> Cylinder286
FEATURE [Part::Compound] Compound124  label="oppo_uzko"
  Links = -> [Cut173,Cut174,Cut157,Cut158,Cut147,Cut148,Cut154]
FEATURE [Part::Mirroring] mirror005  label="Grip_slider-opposite"
  Base = (0,0,0)
  Normal = (1e-16,-1,0)
  Placement = pos=(0,0,20) rot=(1,0,0;3.14159rad)
  Source = -> Compound124
FEATURE [Part::Cylinder] Cylinder206  label="Válec206"
  Angle = 360
  AttacherType = Attacher::AttachEngine3D
  Height = 10
  Placement = pos=(17,-24,10) rot=(1,0,0;1.5708rad)
  Radius = 11
FEATURE [Part::Cylinder] Cylinder207  label="Válec207"
  Angle = 360
  AttacherType = Attacher::AttachEngine3D
  Height = 4
  Placement = pos=(-21,-25.5,15) rot=(0,0,1;0rad)
  Radius = 5
FEATURE [Part::Cylinder] Cylinder208  label="Válec208"
  Angle = 360
  AttacherType = Attacher::AttachEngine3D
  Height = 5
  Placement = pos=(-21,-25.5,15) rot=(0,0,1;0rad)
  Radius = 8.5
FEATURE [Part::Cut] Cut126
  Base = -> Cylinder208
  Tool = -> Cylinder207
FEATURE [Part::Box] Box152  label="Krychle152"
  AttacherType = Attacher::AttachEngine3D
  Height = 5
  Length = 76
  Placement = pos=(-21,-34,15) rot=(0,0,1;0rad)
  Width = 17
FEATURE [Part::Cylinder] Cylinder209  label="Válec209"
  Angle = 360
  AttacherType = Attacher::AttachEngine3D
  Height = 5
  Placement = pos=(55,-25.5,15) rot=(0,0,1;0rad)
  Radius = 8.5
FEATURE [Part::Box] Box153  label="Krychle153"
  AttacherType = Attacher::AttachEngine3D
  Height = 5
  Length = 56
  Placement = pos=(-11,-34,10) rot=(0,0,1;0rad)
  Width = 17
FEATURE [Part::Cylinder] Cylinder214  label="Válec214"
  Angle = 360
  AttacherType = Attacher::AttachEngine3D
  Height = 4
  Placement = pos=(55,-25.5,15) rot=(0,0,1;0rad)
  Radius = 5
FEATURE [Part::Cut] Cut127
  Base = -> Cylinder209
  Tool = -> Cylinder214
FEATURE [Part::Cylinder] Cylinder215  label="Válec215"
  Angle = 360
  AttacherType = Attacher::AttachEngine3D
  Height = 4
  Placement = pos=(-21,-25.5,15) rot=(0,0,1;0rad)
  Radius = 5
FEATURE [Part::Cut] Cut128
  Base = -> Box152
  Tool = -> Cylinder215
FEATURE [Part::Cylinder] Cylinder216  label="Válec216"
  Angle = 360
  AttacherType = Attacher::AttachEngine3D
  Height = 4
  Placement = pos=(55,-25.5,15) rot=(0,0,1;0rad)
  Radius = 5
FEATURE [Part::Cylinder] Cylinder217  label="Válec217"
  Angle = 360
  AttacherType = Attacher::AttachEngine3D
  Height = 20
  Placement = pos=(-5,-17,10) rot=(1,0,0;1.5708rad)
  Radius = 5.1
FEATURE [Part::Cylinder] Cylinder218  label="Válec218"
  Angle = 360
  AttacherType = Attacher::AttachEngine3D
  Height = 20
  Placement = pos=(39,-17,10) rot=(1,0,0;1.5708rad)
  Radius = 5.1
FEATURE [Part::Box] Box155  label="Krychle155"
  AttacherType = Attacher::AttachEngine3D
  Height = 5
  Length = 4
  Placement = pos=(-12,-34,10) rot=(0,0,1;0rad)
  Width = 17
FEATURE [Part::Box] Box156  label="Krychle156"
  AttacherType = Attacher::AttachEngine3D
  Height = 5
  Length = 4
  Placement = pos=(42,-34,10) rot=(0,0,1;0rad)
  Width = 17
FEATURE [Part::Cylinder] Cylinder219  label="Válec219"
  Angle = 360
  AttacherType = Attacher::AttachEngine3D
  Height = 20
  Placement = pos=(39,-17,10) rot=(1,0,0;1.5708rad)
  Radius = 5.1
FEATURE [Part::Cylinder] Cylinder220  label="Válec220"
  Angle = 360
  AttacherType = Attacher::AttachEngine3D
  Height = 20
  Placement = pos=(-5,-17,10) rot=(1,0,0;1.5708rad)
  Radius = 5.1
FEATURE [Part::Box] Box157  label="Krychle157"
  AttacherType = Attacher::AttachEngine3D
  Height = 10
  Length = 80
  Placement = pos=(-20,-36,0) rot=(0,0,1;0rad)
  Width = 20
FEATURE [Part::Cylinder] Cylinder221  label="Válec221"
  Angle = 360
  AttacherType = Attacher::AttachEngine3D
  Height = 10
  Placement = pos=(3,-20,9) rot=(0,0,1;0rad)
  Radius = 1.5
FEATURE [Part::Cylinder] Cylinder222  label="Válec222"
  Angle = 360
  AttacherType = Attacher::AttachEngine3D
  Height = 10
  Placement = pos=(3,-31,9) rot=(0,0,1;0rad)
  Radius = 1.5
FEATURE [Part::Cylinder] Cylinder223  label="Válec223"
  Angle = 360
  AttacherType = Attacher::AttachEngine3D
  Height = 10
  Placement = pos=(31,-20,9) rot=(0,0,1;0rad)
  Radius = 1.5
FEATURE [Part::Cylinder] Cylinder224  label="Válec224"
  Angle = 360
  AttacherType = Attacher::AttachEngine3D
  Height = 10
  Placement = pos=(31,-31,9) rot=(0,0,1;0rad)
  Radius = 1.5
FEATURE [Part::Box] Box158  label="Krychle158"
  AttacherType = Attacher::AttachEngine3D
  Height = 2
  Length = 6
  Placement = pos=(28,-34,13) rot=(0,0,1;0rad)
  Width = 6
FEATURE [Part::Box] Box159  label="Krychle159"
  AttacherType = Attacher::AttachEngine3D
  Height = 2
  Length = 6
  Placement = pos=(0,-23,13) rot=(0,0,1;0rad)
  Width = 6
FEATURE [Part::Box] Box160  label="Krychle160"
  AttacherType = Attacher::AttachEngine3D
  Height = 2
  Length = 6
  Placement = pos=(0,-34,13) rot=(0,0,1;0rad)
  Width = 6
FEATURE [Part::Box] Box161  label="Krychle161"
  AttacherType = Attacher::AttachEngine3D
  Height = 2
  Length = 6
  Placement = pos=(28,-23,13) rot=(0,0,1;0rad)
  Width = 6
FEATURE [Part::Cylinder] Cylinder225  label="Válec225"
  Angle = 360
  AttacherType = Attacher::AttachEngine3D
  Height = 10
  Placement = pos=(3,-31,9) rot=(0,0,1;0rad)
  Radius = 1.5
FEATURE [Part::Compound] Compound090
  Links = -> [Cylinder217,Cylinder218]
FEATURE [Part::Compound] Compound091
  Links = -> [Box155,Box156]
FEATURE [Part::FeaturePython] Tube004  # WARN: FeaturePython — macro-defined, semantics opaque (R4)
  AttacherType = Attacher::AttachEngine3D
  Height = 1
  InnerRadius = 3
  OuterRadius = 5.1
  Placement = pos=(-5,-17,10) rot=(1,0,0;1.5708rad)
FEATURE [Part::FeaturePython] Tube005  # WARN: FeaturePython — macro-defined, semantics opaque (R4)
  AttacherType = Attacher::AttachEngine3D
  Height = 1
  InnerRadius = 3
  OuterRadius = 5.1
  Placement = pos=(-5,-33,10) rot=(1,0,0;1.5708rad)
FEATURE [Part::FeaturePython] Tube006  # WARN: FeaturePython — macro-defined, semantics opaque (R4)
  AttacherType = Attacher::AttachEngine3D
  Height = 1
  InnerRadius = 3
  OuterRadius = 5.1
  Placement = pos=(39,-17,10) rot=(1,0,0;1.5708rad)
FEATURE [Part::FeaturePython] Tube007  # WARN: FeaturePython — macro-defined, semantics opaque (R4)
  AttacherType = Attacher::AttachEngine3D
  Height = 1
  InnerRadius = 3
  OuterRadius = 5.1
  Placement = pos=(39,-33,10) rot=(1,0,0;1.5708rad)
FEATURE [Part::Cut] Cut129
  Base = -> Cut128
  Tool = -> Cylinder216
FEATURE [Part::Cut] Cut131
  Base = -> Box153
  Tool = -> Compound090
FEATURE [Part::Compound] Compound092
  Links = -> [Cylinder220,Cylinder219]
FEATURE [Part::Cut] Cut133
  Base = -> Compound091
  Tool = -> Compound092
FEATURE [Part::Compound] Compound093
  Links = -> [Tube004,Tube005,Tube006,Tube007]
FEATURE [Part::Cut] Cut134
  Base = -> Compound093
  Tool = -> Box157
FEATURE [Part::Compound] Compound094
  Links = -> [Cylinder221,Cylinder222,Cylinder223,Cylinder224]
FEATURE [Part::Cut] Cut136
  Base = -> Cut129
  Tool = -> Compound094
FEATURE [Part::Compound] Compound095
  Links = -> [Box160,Box159,Box158,Box161]
FEATURE [Part::Cylinder] Cylinder226  label="Válec226"
  Angle = 360
  AttacherType = Attacher::AttachEngine3D
  Height = 10
  Placement = pos=(3,-20,9) rot=(0,0,1;0rad)
  Radius = 1.5
FEATURE [Part::Cylinder] Cylinder227  label="Válec227"
  Angle = 360
  AttacherType = Attacher::AttachEngine3D
  Height = 10
  Placement = pos=(31,-20,9) rot=(0,0,1;0rad)
  Radius = 1.5
FEATURE [Part::Cylinder] Cylinder228  label="Válec228"
  Angle = 360
  AttacherType = Attacher::AttachEngine3D
  Height = 10
  Placement = pos=(31,-31,9) rot=(0,0,1;0rad)
  Radius = 1.5
FEATURE [Part::Compound] Compound096
  Links = -> [Cylinder226,Cylinder225,Cylinder227,Cylinder228]
FEATURE [Part::Cut] Cut135
  Base = -> Cut131
  Tool = -> Compound096
FEATURE [Part::Cut] Cut137
  Base = -> Cut135
  Tool = -> Compound095
FEATURE [Part::Cylinder] Cylinder233  label="Válec233"
  Angle = 360
  AttacherType = Attacher::AttachEngine3D
  Height = 30
  Placement = pos=(11.5,-19,4.5) rot=(1,0,0;1.5708rad)
  Radius = 1.5
FEATURE [Part::Cylinder] Cylinder234  label="Válec234"
  Angle = 360
  AttacherType = Attacher::AttachEngine3D
  Height = 30
  Placement = pos=(22.5,-19,4.5) rot=(1,0,0;1.5708rad)
  Radius = 1.5
FEATURE [Part::Cylinder] Cylinder235  label="Válec235"
  Angle = 360
  AttacherType = Attacher::AttachEngine3D
  Height = 30
  Placement = pos=(11.5,-19,15.5) rot=(1,0,0;1.5708rad)
  Radius = 1.5
FEATURE [Part::Cylinder] Cylinder236  label="Válec236"
  Angle = 360
  AttacherType = Attacher::AttachEngine3D
  Height = 30
  Placement = pos=(22.5,-19,15.5) rot=(1,0,0;1.5708rad)
  Radius = 1.5
FEATURE [Part::Box] Box166  label="Krychle166"
  AttacherType = Attacher::AttachEngine3D
  Height = 8
  Length = 6
  Placement = pos=(8.5,-21,12) rot=(0,0,1;0rad)
  Width = 2
FEATURE [Part::Box] Box167  label="Krychle167"
  AttacherType = Attacher::AttachEngine3D
  Height = 8
  Length = 6
  Placement = pos=(19.5,-21,12) rot=(0,0,1;0rad)
  Width = 2
FEATURE [Part::Box] Box168  label="Krychle168"
  AttacherType = Attacher::AttachEngine3D
  Height = 8
  Length = 6
  Placement = pos=(8.5,-21,1) rot=(0,0,1;0rad)
  Width = 2
FEATURE [Part::Box] Box169  label="Krychle169"
  AttacherType = Attacher::AttachEngine3D
  Height = 8
  Length = 6
  Placement = pos=(19.5,-21,1) rot=(0,0,1;0rad)
  Width = 2
FEATURE [Part::Cylinder] Cylinder237  label="Válec237"
  Angle = 360
  AttacherType = Attacher::AttachEngine3D
  Height = 10
  Placement = pos=(17,-24,10) rot=(1,0,0;1.5708rad)
  Radius = 11
FEATURE [Part::Cylinder] Cylinder238  label="Válec238"
  Angle = 360
  AttacherType = Attacher::AttachEngine3D
  Height = 30
  Placement = pos=(22.5,-19,15.5) rot=(1,0,0;1.5708rad)
  Radius = 1.5
FEATURE [Part::Cylinder] Cylinder239  label="Válec239"
  Angle = 360
  AttacherType = Attacher::AttachEngine3D
  Height = 30
  Placement = pos=(22.5,-19,4.5) rot=(1,0,0;1.5708rad)
  Radius = 1.5
FEATURE [Part::Cylinder] Cylinder240  label="Válec240"
  Angle = 360
  AttacherType = Attacher::AttachEngine3D
  Height = 30
  Placement = pos=(11.5,-19,4.5) rot=(1,0,0;1.5708rad)
  Radius = 1.5
FEATURE [Part::Cylinder] Cylinder241  label="Válec241"
  Angle = 360
  AttacherType = Attacher::AttachEngine3D
  Height = 30
  Placement = pos=(11.5,-19,15.5) rot=(1,0,0;1.5708rad)
  Radius = 1.5
FEATURE [Part::Box] Box170  label="Krychle170"
  AttacherType = Attacher::AttachEngine3D
  Height = 8
  Length = 6
  Placement = pos=(8.5,-21,12) rot=(0,0,1;0rad)
  Width = 2
FEATURE [Part::Box] Box171  label="Krychle171"
  AttacherType = Attacher::AttachEngine3D
  Height = 8
  Length = 6
  Placement = pos=(19.5,-21,12) rot=(0,0,1;0rad)
  Width = 2
FEATURE [Part::Box] Box172  label="Krychle172"
  AttacherType = Attacher::AttachEngine3D
  Height = 8
  Length = 6
  Placement = pos=(19.5,-21,1) rot=(0,0,1;0rad)
  Width = 2
FEATURE [Part::Box] Box173  label="Krychle173"
  AttacherType = Attacher::AttachEngine3D
  Height = 8
  Length = 6
  Placement = pos=(8.5,-21,1) rot=(0,0,1;0rad)
  Width = 2
FEATURE [Part::Box] Box1051  label="Krychle1050"
  AttacherType = Attacher::AttachEngine3D
  Height = 5
  Length = 76
  Placement = pos=(-21,-34,15) rot=(0,0,1;0rad)
  Width = 17
FEATURE [Part::Compound] Compound100
  Links = -> [Cylinder233,Cylinder234,Cylinder235,Cylinder236]
  Placement = pos=(0,9,0) rot=(0,0,1;0rad)
FEATURE [Part::Compound] Compound101
  Links = -> [Box166,Box167,Box168,Box169]
FEATURE [Part::Compound] Compound102
  Links = -> [Cylinder240,Cylinder239,Cylinder241,Cylinder238]
  Placement = pos=(0,9,0) rot=(0,0,1;0rad)
FEATURE [Part::Cut] Cut140
  Base = -> Cut137
  Tool = -> Cylinder206
FEATURE [Part::Cut] Cut141
  Base = -> Cut136
  Tool = -> Cylinder237
FEATURE [Part::Cut] Cut142
  Base = -> Cut140
  Tool = -> Compound101
FEATURE [Part::Cut] Cut143
  Base = -> Cut142
  Tool = -> Compound100
FEATURE [Part::Compound] Compound103
  Links = -> [Box170,Box171,Box173,Box172]
FEATURE [Part::Cut] Cut144
  Base = -> Cut141
  Tool = -> Compound102
FEATURE [Part::Cut] Cut146
  Base = -> Cut144
  Tool = -> Compound103
FEATURE [Part::Cylinder] Cylinder2947  label="Válec2917"
  Angle = 360
  AttacherType = Attacher::AttachEngine3D
  Height = 4
  Placement = pos=(55,-25.5,15) rot=(0,0,1;0rad)
  Radius = 5
FEATURE [Part::Cylinder] Cylinder2948  label="Válec2918"
  Angle = 360
  AttacherType = Attacher::AttachEngine3D
  Height = 4
  Placement = pos=(-21,-25.5,15) rot=(0,0,1;0rad)
  Radius = 5
FEATURE [Part::Cylinder] Cylinder2949  label="Válec2919"
  Angle = 360
  AttacherType = Attacher::AttachEngine3D
  Height = 10
  Placement = pos=(31,-20,9) rot=(0,0,1;0rad)
  Radius = 1.5
FEATURE [Part::Cylinder] Cylinder2950  label="Válec2920"
  Angle = 360
  AttacherType = Attacher::AttachEngine3D
  Height = 10
  Placement = pos=(3,-20,9) rot=(0,0,1;0rad)
  Radius = 1.5
FEATURE [Part::Cylinder] Cylinder2951  label="Válec2921"
  Angle = 360
  AttacherType = Attacher::AttachEngine3D
  Height = 10
  Placement = pos=(3,-31,9) rot=(0,0,1;0rad)
  Radius = 1.5
FEATURE [Part::Cylinder] Cylinder2952  label="Válec2922"
  Angle = 360
  AttacherType = Attacher::AttachEngine3D
  Height = 10
  Placement = pos=(31,-31,9) rot=(0,0,1;0rad)
  Radius = 1.5
FEATURE [Part::Compound] Compound1318
  Links = -> [Cylinder2950,Cylinder2951,Cylinder2949,Cylinder2952]
FEATURE [Part::Cut] Cut1117
  Base = -> Box1051
  Tool = -> Cylinder2948
FEATURE [Part::Cut] Cut1116
  Base = -> Cut1117
  Tool = -> Cylinder2947
FEATURE [Part::Cut] Cut1118
  Base = -> Cut1116
  Tool = -> Compound1318
FEATURE [Part::Box] Box1052  label="Krychle1051"
  AttacherType = Attacher::AttachEngine3D
  Height = 8
  Length = 6
  Placement = pos=(19.5,-21,1) rot=(0,0,1;0rad)
  Width = 2
FEATURE [Part::Box] Box1053  label="Krychle1052"
  AttacherType = Attacher::AttachEngine3D
  Height = 8
  Length = 6
  Placement = pos=(8.5,-21,12) rot=(0,0,1;0rad)
  Width = 2
FEATURE [Part::Cylinder] Cylinder2953  label="Válec2923"
  Angle = 360
  AttacherType = Attacher::AttachEngine3D
  Height = 30
  Placement = pos=(11.5,-19,4.5) rot=(1,0,0;1.5708rad)
  Radius = 1.5
FEATURE [Part::Box] Box1054  label="Krychle1053"
  AttacherType = Attacher::AttachEngine3D
  Height = 8
  Length = 6
  Placement = pos=(19.5,-21,12) rot=(0,0,1;0rad)
  Width = 2
FEATURE [Part::Cylinder] Cylinder2954  label="Válec2924"
  Angle = 360
  AttacherType = Attacher::AttachEngine3D
  Height = 10
  Placement = pos=(17,-24,10) rot=(1,0,0;1.5708rad)
  Radius = 11
FEATURE [Part::Cylinder] Cylinder2955  label="Válec2925"
  Angle = 360
  AttacherType = Attacher::AttachEngine3D
  Height = 30
  Placement = pos=(11.5,-19,15.5) rot=(1,0,0;1.5708rad)
  Radius = 1.5
FEATURE [Part::Cylinder] Cylinder2956  label="Válec2926"
  Angle = 360
  AttacherType = Attacher::AttachEngine3D
  Height = 30
  Placement = pos=(22.5,-19,4.5) rot=(1,0,0;1.5708rad)
  Radius = 1.5
FEATURE [Part::Cylinder] Cylinder2957  label="Válec2927"
  Angle = 360
  AttacherType = Attacher::AttachEngine3D
  Height = 30
  Placement = pos=(22.5,-19,15.5) rot=(1,0,0;1.5708rad)
  Radius = 1.5
FEATURE [Part::Compound] Compound1317
  Links = -> [Cylinder2953,Cylinder2956,Cylinder2955,Cylinder2957]
  Placement = pos=(0,9,0) rot=(0,0,1;0rad)
FEATURE [Part::Box] Box1055  label="Krychle1054"
  AttacherType = Attacher::AttachEngine3D
  Height = 8
  Length = 6
  Placement = pos=(8.5,-21,1) rot=(0,0,1;0rad)
  Width = 2
FEATURE [Part::Cylinder] Cylinder282  label="Válec282"
  Angle = 360
  AttacherType = Attacher::AttachEngine3D
  Height = 20
  Placement = pos=(17,-14,10) rot=(1,0,0;1.5708rad)
  Radius = 5
FEATURE [Part::Cut] Cut168
  Base = -> Cut143
  Tool = -> Cylinder282
FEATURE [Part::Cylinder] Cylinder284  label="Válec284"
  Angle = 360
  AttacherType = Attacher::AttachEngine3D
  Height = 2
  Placement = pos=(17,-22,10) rot=(1,0,0;1.5708rad)
  Radius = 5.25
FEATURE [Part::Cut] Cut1119
  Base = -> Cut1118
  Tool = -> Cylinder2954
FEATURE [Part::Cut] Cut1115
  Base = -> Cut1119
  Tool = -> Compound1317
FEATURE [Part::Compound] Compound1319
  Links = -> [Box1053,Box1054,Box1055,Box1052]
FEATURE [Part::Cut] Cut167
  Base = -> Cut1115
  Tool = -> Compound1319
FEATURE [Part::Cut] Cut169
  Base = -> Cut168
  Tool = -> Cylinder284
FEATURE [Part::Cylinder] Cylinder324  label="Válec324"
  Angle = 360
  AttacherType = Attacher::AttachEngine3D
  Height = 20
  Placement = pos=(39,-17,10) rot=(1,0,0;1.5708rad)
  Radius = 5.1
FEATURE [Part::Cylinder] Cylinder325  label="Válec325"
  Angle = 360
  AttacherType = Attacher::AttachEngine3D
  Height = 20
  Placement = pos=(-5,-17,10) rot=(1,0,0;1.5708rad)
  Radius = 5.1
FEATURE [Part::Compound] Compound143
  Links = -> [Cylinder325,Cylinder324]
FEATURE [Part::Cut] Cut206
  Base = -> Cut146
  Tool = -> Compound143
FEATURE [Part::Compound] Compound144  label="Grip_slider"
  Links = -> [Cut167,Cut126,Cut127,Cut133,Cut134,Cut206,Cut169]
FEATURE [Part::Cylinder] Cylinder461  label="Válec461"
  Angle = 360
  AttacherType = Attacher::AttachEngine3D
  Height = 6
  Placement = pos=(17,-24,10) rot=(1,0,0;1.5708rad)
  Radius = 10
FEATURE [Part::Cylinder] Cylinder462  label="Válec462"
  Angle = 360
  AttacherType = Attacher::AttachEngine3D
  Height = 30
  Placement = pos=(11.5,-19,4.5) rot=(1,0,0;1.5708rad)
  Radius = 1.5
FEATURE [Part::Cylinder] Cylinder463  label="Válec463"
  Angle = 360
  AttacherType = Attacher::AttachEngine3D
  Height = 30
  Placement = pos=(11.5,-19,15.5) rot=(1,0,0;1.5708rad)
  Radius = 1.5
FEATURE [Part::Cylinder] Cylinder464  label="Válec464"
  Angle = 360
  AttacherType = Attacher::AttachEngine3D
  Height = 30
  Placement = pos=(22.5,-19,4.5) rot=(1,0,0;1.5708rad)
  Radius = 1.5
FEATURE [Part::Cylinder] Cylinder465  label="Válec465"
  Angle = 360
  AttacherType = Attacher::AttachEngine3D
  Height = 30
  Placement = pos=(22.5,-19,15.5) rot=(1,0,0;1.5708rad)
  Radius = 1.5
FEATURE [Part::Compound] Compound224
  Links = -> [Cylinder462,Cylinder464,Cylinder463,Cylinder465]
  Placement = pos=(0,9,0) rot=(0,0,1;0rad)
FEATURE [Part::Cylinder] Cylinder466  label="Válec466"
  Angle = 360
  AttacherType = Attacher::AttachEngine3D
  Height = 6
  Placement = pos=(17,-24,10) rot=(1,0,0;1.5708rad)
  Radius = 5.5
FEATURE [Part::Cut] Cut276
  Base = -> Cylinder461
  Tool = -> Cylinder466
FEATURE [Part::Cut] Cut277
  Base = -> Cut276
  Tool = -> Compound224
FEATURE [Part::Cylinder] Cylinder467  label="Válec467"
  Angle = 360
  AttacherType = Attacher::AttachEngine3D
  Height = 3
  Placement = pos=(11.5,-19,4.5) rot=(1,0,0;1.5708rad)
  Radius = 3
FEATURE [Part::Cylinder] Cylinder468  label="Válec468"
  Angle = 360
  AttacherType = Attacher::AttachEngine3D
  Height = 3
  Placement = pos=(22.5,-19,4.5) rot=(1,0,0;1.5708rad)
  Radius = 3
FEATURE [Part::Cylinder] Cylinder469  label="Válec469"
  Angle = 360
  AttacherType = Attacher::AttachEngine3D
  Height = 3
  Placement = pos=(11.5,-19,15.5) rot=(1,0,0;1.5708rad)
  Radius = 3
FEATURE [Part::Cylinder] Cylinder470  label="Válec470"
  Angle = 360
  AttacherType = Attacher::AttachEngine3D
  Height = 3
  Placement = pos=(22.5,-19,15.5) rot=(1,0,0;1.5708rad)
  Radius = 3
FEATURE [Part::Compound] Compound225
  Links = -> [Cylinder467,Cylinder468,Cylinder469,Cylinder470]
  Placement = pos=(0,-5,0) rot=(0,0,1;0rad)
FEATURE [Part::Cut] Cut278
  Base = -> Cut277
  Tool = -> Compound225
FEATURE [Part::Box] Box294  label="Krychle294"
  AttacherType = Attacher::AttachEngine3D
  Height = 8
  Length = 26
  Placement = pos=(-17,-30,6) rot=(0,0,1;0rad)
  Width = 6
FEATURE [Part::Box] Box295  label="Krychle295"
  AttacherType = Attacher::AttachEngine3D
  Height = 8
  Length = 26
  Placement = pos=(25,-30,6) rot=(0,0,1;0rad)
  Width = 6
FEATURE [Part::Cylinder] Cylinder471  label="Válec471"
  Angle = 360
  AttacherType = Attacher::AttachEngine3D
  Height = 6
  Placement = pos=(17,-24,10) rot=(1,0,0;1.5708rad)
  Radius = 28
FEATURE [Part::Common] Common
  Base = -> Box294
  Tool = -> Cylinder471
FEATURE [Part::Cylinder] Cylinder472  label="Válec472"
  Angle = 360
  AttacherType = Attacher::AttachEngine3D
  Height = 6
  Placement = pos=(17,-24,10) rot=(1,0,0;1.5708rad)
  Radius = 33
FEATURE [Part::Common] Common001
  Base = -> Box295
  Tool = -> Cylinder472
FEATURE [Part::Compound] Compound226  label="Grip_ufo"
  Links = -> [Cut278,Common,Common001]
  Placement = pos=(27,-58,27) rot=(0.707107,0,-0.707107;3.14159rad)
FEATURE [Part::Box] Box255  label="Krychle255"
  AttacherType = Attacher::AttachEngine3D
  Height = 2
  Length = 6
  Placement = pos=(-2,11,4) rot=(0,0,1;0rad)
  Width = 6
FEATURE [Part::Cylinder] Cylinder391  label="Válec391"
  Angle = 360
  AttacherType = Attacher::AttachEngine3D
  Height = 4
  Placement = pos=(1,14,-0.1) rot=(0,0,1;0rad)
  Radius = 1.5
FEATURE [Part::Cylinder] Cylinder392  label="Válec392"
  Angle = 360
  AttacherType = Attacher::AttachEngine3D
  Height = 12
  Placement = pos=(1,14,6) rot=(0,0,1;0rad)
  Radius = 1.5
FEATURE [Part::Cylinder] Cylinder393  label="Válec393"
  Angle = 360
  AttacherType = Attacher::AttachEngine3D
  Height = 12
  Placement = pos=(1,14,6) rot=(0,0,1;0rad)
  Radius = 1.5
FEATURE [Part::Cylinder] Cylinder394  label="Válec394"
  Angle = 360
  AttacherType = Attacher::AttachEngine3D
  Height = 4
  Placement = pos=(1,14,-0.1) rot=(0,0,1;0rad)
  Radius = 1.5
FEATURE [Part::Box] Box256  label="Krychle256"
  AttacherType = Attacher::AttachEngine3D
  Height = 2
  Length = 6
  Placement = pos=(-2,11,4) rot=(0,0,1;0rad)
  Width = 6
FEATURE [Part::Box] Box257  label="Krychle257"
  AttacherType = Attacher::AttachEngine3D
  Height = 12
  Length = 1
  Placement = pos=(21.4,-4.5,-2) rot=(0,0,1;0rad)
  Width = 10
FEATURE [Part::Box] Box259  label="Krychle259"
  AttacherType = Attacher::AttachEngine3D
  Height = 12
  Length = 2
  Placement = pos=(21.4,80,-2) rot=(0,0,1;0rad)
  Width = 19
FEATURE [Part::Cylinder] Cylinder397  label="Válec397"
  Angle = 360
  AttacherType = Attacher::AttachEngine3D
  Height = 3
  Placement = pos=(1,14,6) rot=(0,0,1;0rad)
  Radius = 3
FEATURE [Part::Cylinder] Cylinder398  label="Válec398"
  Angle = 360
  AttacherType = Attacher::AttachEngine3D
  Height = 3
  Placement = pos=(1,14,6) rot=(0,0,1;0rad)
  Radius = 3
FEATURE [Part::FeaturePython] involuterack  # WARN: FeaturePython — macro-defined, semantics opaque (R4)
  AttacherType = Attacher::AttachEngine3D
  Placement = pos=(23,6,-2) rot=(0,0,1;0rad)
  add_endings = true
  beta = 0
  clearance = 0.25
  double_helix = false
  head = 0
  height = 12
  module = 0.5
  pressure_angle = 20
  properties_from_tool = true
  simplified = false
  teeth = 44
  thickness = 1
  transverse_pitch = 1.5708
  version = 0.0.3
FEATURE [Part::FeaturePython] involuterack001  # WARN: FeaturePython — macro-defined, semantics opaque (R4)
  AttacherType = Attacher::AttachEngine3D
  Placement = pos=(25,81,-2) rot=(0,0,1;0rad)
  add_endings = true
  beta = 0
  clearance = 0.25
  double_helix = false
  head = 0
  height = 12
  module = 0.5
  pressure_angle = 20
  properties_from_tool = true
  simplified = false
  teeth = 12
  thickness = 1
  transverse_pitch = 1.5708
  version = 0.0.3
FEATURE [Part::Compound] Compound180
  Links = -> [Box255,Cylinder392,Cylinder391]
  Placement = pos=(6,73,2) rot=(0,1,0;1.5708rad)
FEATURE [Part::Cut] Cut239
  Base = -> Box259
  Tool = -> Compound180
FEATURE [Part::Compound] Compound181
  Links = -> [Box256,Cylinder393,Cylinder394]
  Placement = pos=(6,-14,2) rot=(0,1,0;1.5708rad)
FEATURE [Part::Cut] Cut238
  Base = -> Box257
  Tool = -> Compound181
FEATURE [Part::Compound] Compound183
  Links = -> [Cylinder397]
  Placement = pos=(16.5,73,2) rot=(0,1,0;1.5708rad)
FEATURE [Part::Cut] Cut240
  Base = -> Cut239
  Tool = -> Compound183
FEATURE [Part::Compound] Compound184
  Links = -> [Cylinder398]
  Placement = pos=(16.5,73,2) rot=(0,1,0;1.5708rad)
FEATURE [Part::Cut] Cut241
  Base = -> involuterack001
  Placement = pos=(0,-7,0) rot=(0,0,1;0rad)
  Tool = -> Compound184
FEATURE [Part::Chamfer] Chamfer034
  Base = -> Cut240
  Edges = 1 edges r=1.9: [Edge4]
  Placement = pos=(0,-7,0) rot=(0,0,1;0rad)
FEATURE [Part::Compound] Compound185  label="Grip_toothed-belt"
  Links = -> [Cut238,involuterack,Cut241,Chamfer034]
FEATURE [Part::FeaturePython] Tube015  # WARN: FeaturePython — macro-defined, semantics opaque (R4)
  AttacherType = Attacher::AttachEngine3D
  Height = 8
  InnerRadius = 58
  OuterRadius = 64
  Placement = pos=(37,-1.5,6) rot=(0,0,1;0rad)
FEATURE [Part::Cylinder] Cylinder318  label="Válec318"
  Angle = 360
  AttacherType = Attacher::AttachEngine3D
  Height = 8
  Placement = pos=(-13,-25,6) rot=(0,0,1;0rad)
  Radius = 5
FEATURE [Part::Cylinder] Cylinder319  label="Válec319"
  Angle = 360
  AttacherType = Attacher::AttachEngine3D
  Height = 12
  Placement = pos=(-13,-25,4) rot=(0,0,1;0rad)
  Radius = 2.65
FEATURE [Part::Cut] Cut205
  Base = -> Cylinder318
  Placement = pos=(5,-15,0) rot=(0,0,1;0rad)
  Tool = -> Cylinder319
FEATURE [Part::Cylinder] Cylinder320  label="Válec320"
  Angle = 360
  AttacherType = Attacher::AttachEngine3D
  Height = 12
  Placement = pos=(-10,30,4) rot=(0,0,1;0rad)
  Radius = 2.65
FEATURE [Part::Box] Box210  label="Krychle210"
  AttacherType = Attacher::AttachEngine3D
  Height = 20
  Length = 100
  Placement = pos=(36,0,0) rot=(0,0,1;1.01229rad)
  Width = 100
FEATURE [Part::Box] Box211  label="Krychle211"
  AttacherType = Attacher::AttachEngine3D
  Height = 20
  Length = 100
  Placement = pos=(36,0,0) rot=(0,0,-1;1.16937rad)
  Width = 100
FEATURE [Part::Cylinder] Cylinder321  label="Válec321"
  Angle = 360
  AttacherType = Attacher::AttachEngine3D
  Height = 12
  Placement = pos=(-8,-40,4) rot=(0,0,1;0rad)
  Radius = 2.65
FEATURE [Part::Box] Box212  label="Krychle212"
  AttacherType = Attacher::AttachEngine3D
  Height = 20
  Length = 100
  Placement = pos=(36,0,0) rot=(0,0,1;3.89208rad)
  Width = 100
FEATURE [Part::Box] Box213  label="Krychle213"
  AttacherType = Attacher::AttachEngine3D
  Height = 20
  Length = 100
  Placement = pos=(36,0,0) rot=(0,0,-1;0.401426rad)
  Width = 100
FEATURE [Part::Cylinder] Cylinder322  label="Válec322"
  Angle = 360
  AttacherType = Attacher::AttachEngine3D
  Height = 12
  Placement = pos=(-13,30,4) rot=(0,0,1;0rad)
  Radius = 2.65
FEATURE [Part::Cylinder] Cylinder323  label="Válec323"
  Angle = 360
  AttacherType = Attacher::AttachEngine3D
  Height = 8
  Placement = pos=(-10,30,6) rot=(0,0,1;0rad)
  Radius = 5
FEATURE [Part::Cut] Cut204
  Base = -> Cylinder323
  Placement = pos=(-3,0,0) rot=(0,0,1;0rad)
  Tool = -> Cylinder320
FEATURE [Part::Compound] Compound140  label="tahlo_lefto005"
  Links = -> [Cut204,Cut205]
FEATURE [Part::Compound] Compound142
  Links = -> [Cylinder322,Cylinder321]
FEATURE [Part::Cut] Cut203
  Base = -> Tube015
  Tool = -> Compound142
FEATURE [Part::Cut] Cut200
  Base = -> Cut203
  Tool = -> Box210
FEATURE [Part::Cut] Cut201
  Base = -> Cut200
  Tool = -> Box213
FEATURE [Part::Cut] Cut199
  Base = -> Cut201
  Tool = -> Box211
FEATURE [Part::Cut] Cut202
  Base = -> Cut199
  Tool = -> Box212
FEATURE [Part::Compound] Compound141  label="Grip_finger-rod"
  Links = -> [Cut202,Compound140]
FEATURE [Part::Cylinder] Cylinder2958  label="Válec2928"
  Angle = 360
  AttacherType = Attacher::AttachEngine3D
  Height = 4
  Placement = pos=(1,14,0) rot=(0,0,1;0rad)
  Radius = 1.5
FEATURE [Part::Cylinder] Cylinder2959  label="Válec2929"
  Angle = 360
  AttacherType = Attacher::AttachEngine3D
  Height = 4
  Placement = pos=(-7,41,6) rot=(0,0,1;0rad)
  Radius = 6
FEATURE [Part::Cylinder] Cylinder2960  label="Válec2930"
  Angle = 360
  AttacherType = Attacher::AttachEngine3D
  Height = 7
  Placement = pos=(-5,59.5,-2) rot=(0,0,1;0rad)
  Radius = 8
FEATURE [Part::Cylinder] Cylinder2961  label="Válec2931"
  Angle = 360
  AttacherType = Attacher::AttachEngine3D
  Height = 10
  Placement = pos=(-8,61,1) rot=(0,0,1;0rad)
  Radius = 5
FEATURE [Part::Cylinder] Cylinder2962  label="Válec2932"
  Angle = 360
  AttacherType = Attacher::AttachEngine3D
  Height = 10
  Placement = pos=(-8,61,1) rot=(0,0,1;0rad)
  Radius = 5
FEATURE [Part::Box] Box1056  label="Krychle1055"
  AttacherType = Attacher::AttachEngine3D
  Height = 12
  Length = 12
  Placement = pos=(-13,42,-2) rot=(0,0,-1;0.261799rad)
  Width = 20
FEATURE [Part::Box] Box1057  label="Krychle1056"
  AttacherType = Attacher::AttachEngine3D
  Height = 12
  Length = 12
  Placement = pos=(-7.85,61.2,-2) rot=(0,0,-1;0.610865rad)
  Width = 12
FEATURE [Part::Box] Box1058  label="Krychle1057"
  AttacherType = Attacher::AttachEngine3D
  Height = 12
  Length = 12
  Placement = pos=(5,60.6,-2) rot=(0,0,1;0.523599rad)
  Width = 12
FEATURE [Part::Cylinder] Cylinder2963  label="Válec2933"
  Angle = 360
  AttacherType = Attacher::AttachEngine3D
  Height = 8
  Placement = pos=(-7,41,-2) rot=(0,0,1;0rad)
  Radius = 9
FEATURE [Part::Cylinder] Cylinder2964  label="Válec2934"
  Angle = 360
  AttacherType = Attacher::AttachEngine3D
  Height = 10
  Placement = pos=(-9,61,5) rot=(0,0,1;0rad)
  Radius = 10
FEATURE [Part::Cylinder] Cylinder2965  label="Válec2935"
  Angle = 360
  AttacherType = Attacher::AttachEngine3D
  Height = 10
  Placement = pos=(-9,61,5) rot=(0,0,1;0rad)
  Radius = 10
FEATURE [Part::Cylinder] Cylinder2966  label="Válec2936"
  Angle = 360
  AttacherType = Attacher::AttachEngine3D
  Height = 10
  Placement = pos=(-5,59,1) rot=(0,0,1;0rad)
  Radius = 5
FEATURE [Part::Cylinder] Cylinder2967  label="Válec2937"
  Angle = 360
  AttacherType = Attacher::AttachEngine3D
  Height = 10
  Placement = pos=(-5,59,1) rot=(0,0,1;0rad)
  Radius = 5
FEATURE [Part::Cylinder] Cylinder162  label="Válec162"
  Angle = 360
  AttacherType = Attacher::AttachEngine3D
  Height = 3
  Placement = pos=(1,14,-2) rot=(0,0,1;0rad)
  Radius = 3
FEATURE [Part::Cylinder] Cylinder2968  label="Válec2938"
  Angle = 360
  AttacherType = Attacher::AttachEngine3D
  Height = 20
  Placement = pos=(1,14,1.01) rot=(0,0,1;0rad)
  Radius = 1.5
FEATURE [Part::Cylinder] Cylinder150  label="Válec150"
  Angle = 360
  AttacherType = Attacher::AttachEngine3D
  Height = 3
  Placement = pos=(1,14,-2) rot=(0,0,1;0rad)
  Radius = 3
FEATURE [Part::Cylinder] Cylinder149  label="Válec149"
  Angle = 360
  AttacherType = Attacher::AttachEngine3D
  Height = 20
  Placement = pos=(1,14,1.01) rot=(0,0,1;0rad)
  Radius = 1.5
FEATURE [Part::Cylinder] Cylinder163  label="Válec163"
  Angle = 360
  AttacherType = Attacher::AttachEngine3D
  Height = 20
  Placement = pos=(1,14,1.01) rot=(0,0,1;0rad)
  Radius = 1.5
FEATURE [Part::Cylinder] Cylinder164  label="Válec164"
  Angle = 360
  AttacherType = Attacher::AttachEngine3D
  Height = 3
  Placement = pos=(1,14,-2) rot=(0,0,1;0rad)
  Radius = 3
FEATURE [Part::Cylinder] Cylinder161  label="Válec161"
  Angle = 360
  AttacherType = Attacher::AttachEngine3D
  Height = 20
  Placement = pos=(1,14,1.01) rot=(0,0,1;0rad)
  Radius = 1.5
FEATURE [Part::Cylinder] Cylinder160  label="Válec160"
  Angle = 360
  AttacherType = Attacher::AttachEngine3D
  Height = 3
  Placement = pos=(1,14,-2) rot=(0,0,1;0rad)
  Radius = 3
FEATURE [Part::Cylinder] Cylinder159  label="Válec159"
  Angle = 360
  AttacherType = Attacher::AttachEngine3D
  Height = 20
  Placement = pos=(1,14,1.01) rot=(0,0,1;0rad)
  Radius = 1.5
FEATURE [Part::Cylinder] Cylinder158  label="Válec158"
  Angle = 360
  AttacherType = Attacher::AttachEngine3D
  Height = 3
  Placement = pos=(1,14,-2) rot=(0,0,1;0rad)
  Radius = 3
FEATURE [Part::Cylinder] Cylinder157  label="Válec157"
  Angle = 360
  AttacherType = Attacher::AttachEngine3D
  Height = 20
  Placement = pos=(1,14,1.01) rot=(0,0,1;0rad)
  Radius = 1.5
FEATURE [Part::Box] Box1059  label="Krychle1058"
  AttacherType = Attacher::AttachEngine3D
  Height = 2
  Length = 6
  Placement = pos=(-2,11,4) rot=(0,0,1;0rad)
  Width = 6
FEATURE [Part::Cylinder] Cylinder2969  label="Válec2939"
  Angle = 360
  AttacherType = Attacher::AttachEngine3D
  Height = 12
  Placement = pos=(1,14,6) rot=(0,0,1;0rad)
  Radius = 1.5
FEATURE [Part::Fillet] Fillet041
  Base = -> Box1058
  Edges = 1 edges r=4: [Edge5]
FEATURE [Part::Cut] Cut1123
  Base = -> Cylinder2960
  Tool = -> Cylinder2961
FEATURE [Part::Cut] Cut1124
  Base = -> Box1056
  Tool = -> Cylinder2963
FEATURE [Part::Cut] Cut1125
  Base = -> Box1057
  Tool = -> Cylinder2964
FEATURE [Part::Cut] Cut1121
  Base = -> Cut1125
  Tool = -> Cylinder2967
FEATURE [Part::Fillet] Fillet040
  Base = -> Cut1121
  Edges = 1 edges r=3: [Edge5]
FEATURE [Part::Cut] Cut1122
  Base = -> Fillet040
  Tool = -> Cylinder2962
FEATURE [Part::Cut] Cut1126
  Base = -> Cut1124
  Tool = -> Cylinder2965
FEATURE [Part::Cut] Cut1120
  Base = -> Cut1126
  Tool = -> Cylinder2966
FEATURE [Part::Fillet] Fillet039
  Base = -> Cut1120
  Edges = 1 edges r=2: [Edge3]
FEATURE [Part::Fillet] Fillet038
  Base = -> Fillet039
  Edges = 1 edges r=1: [Edge28]
FEATURE [Part::Compound] Compound1323
  Links = -> [Cylinder149,Cylinder150]
  Placement = pos=(12.3,47.5,0) rot=(0,0,1;1.309rad)
FEATURE [Part::Cut] Cut1130
  Base = -> Cut1122
  Tool = -> Compound1323
FEATURE [Part::Compound] Compound1325
  Links = -> [Box1059,Cylinder2969,Cylinder2958]
  Placement = pos=(11.7,56.9,2) rot=(-0.250563,0.935113,0.250563;1.63782rad)
FEATURE [Part::Compound] Compound1326
  Links = -> [Cylinder163,Cylinder164]
  Placement = pos=(-5,16,0) rot=(0,0,1;0rad)
FEATURE [Part::Compound] Compound1327
  Links = -> [Cylinder161,Cylinder162]
  Placement = pos=(-5,16,0) rot=(0,0,1;0rad)
FEATURE [Part::Compound] Compound1330
  Links = -> [Cylinder158,Cylinder157]
  Placement = pos=(-2.9,-11.9,0) rot=(0,0,-1;0.261799rad)
FEATURE [Part::Compound] Compound1331
  Links = -> [Cylinder159,Cylinder160]
  Placement = pos=(-2.9,-11.9,0) rot=(0,0,-1;0.261799rad)
FEATURE [Part::Cylinder] Cylinder2970  label="Válec2940"
  Angle = 360
  AttacherType = Attacher::AttachEngine3D
  Height = 6
  Placement = pos=(-7,41,5) rot=(0,0,1;0rad)
  Radius = 2.6
FEATURE [Part::Cut] Cut1127
  Base = -> Cylinder2959
  Tool = -> Cylinder2970
FEATURE [Part::Cylinder] Cylinder2971  label="Válec2941"
  Angle = 360
  AttacherType = Attacher::AttachEngine3D
  Height = 6
  Placement = pos=(-7,41,5) rot=(0,0,1;0rad)
  Radius = 2.6
FEATURE [Part::Cylinder] Cylinder2972  label="Válec2942"
  Angle = 360
  AttacherType = Attacher::AttachEngine3D
  Height = 10
  Placement = pos=(-7,41,1) rot=(0,0,1;0rad)
  Radius = 5
FEATURE [Part::Cylinder] Cylinder2973  label="Válec2943"
  Angle = 360
  AttacherType = Attacher::AttachEngine3D
  Height = 10
  Placement = pos=(-7,41,1) rot=(0,0,1;0rad)
  Radius = 5
FEATURE [Part::Cylinder] Cylinder2974  label="Válec2944"
  Angle = 360
  AttacherType = Attacher::AttachEngine3D
  Height = 7
  Placement = pos=(10,-10,-2) rot=(0,0,1;0rad)
  Radius = 7
FEATURE [Part::Cylinder] Cylinder2975  label="Válec2945"
  Angle = 360
  AttacherType = Attacher::AttachEngine3D
  Height = 4
  Placement = pos=(10,-10,1) rot=(0,0,1;0rad)
  Radius = 5
FEATURE [Part::Cut] Cut1136
  Base = -> Cylinder2974
  Placement = pos=(3,-1,0) rot=(0,0,1;0rad)
  Tool = -> Cylinder2975
FEATURE [Part::Box] Box1060  label="Krychle1059"
  AttacherType = Attacher::AttachEngine3D
  Height = 12
  Length = 12
  Placement = pos=(-13,24,-2) rot=(0,0,1;0rad)
  Width = 18
FEATURE [Part::Box] Box1061  label="Krychle1060"
  AttacherType = Attacher::AttachEngine3D
  Height = 12
  Length = 12
  Placement = pos=(-3.8,-1.4,-2) rot=(0,0,1;0.349066rad)
  Width = 26
FEATURE [Part::Box] Box1062  label="Krychle1061"
  AttacherType = Attacher::AttachEngine3D
  Height = 7
  Length = 12
  Placement = pos=(4,-10,-2) rot=(0,0,1;0rad)
  Width = 18
FEATURE [Part::Box] Box1063  label="Krychle1062"
  AttacherType = Attacher::AttachEngine3D
  Height = 12
  Length = 12
  Placement = pos=(13.25,-5,-2) rot=(0,0,1;1.309rad)
  Width = 19
FEATURE [Part::Fillet] Fillet043
  Base = -> Box1063
  Edges = 2 edges r=4: [Edge1,Edge5]
FEATURE [Part::Fillet] Fillet048
  Base = -> Fillet043
  Edges = 1 edges r=3: [Edge4]
FEATURE [Part::Cylinder] Cylinder2976  label="Válec2946"
  Angle = 360
  AttacherType = Attacher::AttachEngine3D
  Height = 7
  Placement = pos=(-7,41,-2) rot=(0,0,1;0rad)
  Radius = 7
FEATURE [Part::Cylinder] Cylinder2977  label="Válec2947"
  Angle = 360
  AttacherType = Attacher::AttachEngine3D
  Height = 7
  Placement = pos=(-7,41,5) rot=(0,0,1;0rad)
  Radius = 7
FEATURE [Part::Cut] Cut1135
  Base = -> Box1060
  Tool = -> Cylinder2977
FEATURE [Part::Cylinder] Cylinder2978  label="Válec2948"
  Angle = 360
  AttacherType = Attacher::AttachEngine3D
  Height = 10
  Placement = pos=(-9,23,1) rot=(0,0,1;0rad)
  Radius = 5
FEATURE [Part::Cylinder] Cylinder2979  label="Válec2949"
  Angle = 360
  AttacherType = Attacher::AttachEngine3D
  Height = 10
  Placement = pos=(-13,22,5) rot=(0,0,1;0rad)
  Radius = 10
FEATURE [Part::Cylinder] Cylinder2980  label="Válec2950"
  Angle = 360
  AttacherType = Attacher::AttachEngine3D
  Height = 10
  Placement = pos=(-13,22,5) rot=(0,0,1;0rad)
  Radius = 10
FEATURE [Part::Cylinder] Cylinder2981  label="Válec2951"
  Angle = 360
  AttacherType = Attacher::AttachEngine3D
  Height = 10
  Placement = pos=(-9,23,1) rot=(0,0,1;0rad)
  Radius = 5
FEATURE [Part::Cylinder] Cylinder2982  label="Válec2952"
  Angle = 360
  AttacherType = Attacher::AttachEngine3D
  Height = 4
  Placement = pos=(10,-10,1) rot=(0,0,1;0rad)
  Radius = 5
FEATURE [Part::Cylinder] Cylinder2983  label="Válec2953"
  Angle = 360
  AttacherType = Attacher::AttachEngine3D
  Height = 7
  Placement = pos=(-10,23,-2) rot=(0,0,1;0rad)
  Radius = 8
FEATURE [Part::Cylinder] Cylinder2984  label="Válec2954"
  Angle = 360
  AttacherType = Attacher::AttachEngine3D
  Height = 10
  Placement = pos=(-13,22,1) rot=(0,0,1;0rad)
  Radius = 5
FEATURE [Part::Cylinder] Cylinder2985  label="Válec2955"
  Angle = 360
  AttacherType = Attacher::AttachEngine3D
  Height = 10
  Placement = pos=(-13,22,1) rot=(0,0,1;0rad)
  Radius = 5
FEATURE [Part::Cylinder] Cylinder2986  label="Válec2956"
  Angle = 360
  AttacherType = Attacher::AttachEngine3D
  Height = 10
  Placement = pos=(-13,22,1) rot=(0,0,1;0rad)
  Radius = 5
FEATURE [Part::Cylinder] Cylinder2987  label="Válec2957"
  Angle = 360
  AttacherType = Attacher::AttachEngine3D
  Height = 4
  Placement = pos=(1,14,-0.1) rot=(0,0,1;0rad)
  Radius = 1.5
FEATURE [Part::Cylinder] Cylinder2988  label="Válec2958"
  Angle = 360
  AttacherType = Attacher::AttachEngine3D
  Height = 12
  Placement = pos=(1,14,6) rot=(0,0,1;0rad)
  Radius = 1.5
FEATURE [Part::Cylinder] Cylinder2989  label="Válec2959"
  Angle = 360
  AttacherType = Attacher::AttachEngine3D
  Height = 12
  Placement = pos=(1,14,6) rot=(0,0,1;0rad)
  Radius = 1.5
FEATURE [Part::Box] Box1064  label="Krychle1063"
  AttacherType = Attacher::AttachEngine3D
  Height = 2
  Length = 6
  Placement = pos=(-2,11,4) rot=(0,0,1;0rad)
  Width = 6
FEATURE [Part::Compound] Compound1329
  Links = -> [Box1064,Cylinder2988,Cylinder2987]
  Placement = pos=(6,-14,2) rot=(0,1,0;1.5708rad)
FEATURE [Part::Box] Box1065  label="Krychle1064"
  AttacherType = Attacher::AttachEngine3D
  Height = 2
  Length = 6
  Placement = pos=(-2,11,4) rot=(0,0,1;0rad)
  Width = 6
FEATURE [Part::Cylinder] Cylinder2990  label="Válec2960"
  Angle = 360
  AttacherType = Attacher::AttachEngine3D
  Height = 4
  Placement = pos=(1,14,-0.1) rot=(0,0,1;0rad)
  Radius = 1.5
FEATURE [Part::Compound] Compound1328
  Links = -> [Box1065,Cylinder2989,Cylinder2990]
  Placement = pos=(6,-14,2) rot=(0,1,0;1.5708rad)
FEATURE [Part::Cut] Cut1137
  Base = -> Cylinder2976
  Tool = -> Cylinder2972
FEATURE [Part::Cut] Cut1138
  Base = -> Cut1135
  Tool = -> Cylinder2973
FEATURE [Part::Cut] Cut1139
  Base = -> Box1061
  Tool = -> Cylinder2979
FEATURE [Part::Cut] Cut1140
  Base = -> Cut1138
  Tool = -> Cylinder2980
FEATURE [Part::Cut] Cut1141
  Base = -> Cut1139
  Tool = -> Cylinder2981
FEATURE [Part::Fillet] Fillet045
  Base = -> Cut1141
  Edges = 1 edges r=6: [Edge2]
FEATURE [Part::Cut] Cut1142
  Base = -> Cut1140
  Tool = -> Cylinder2978
FEATURE [Part::Fillet] Fillet044
  Base = -> Cut1142
  Edges = 1 edges r=4: [Edge10]
FEATURE [Part::Fillet] Fillet046
  Base = -> Fillet044
  Edges = 1 edges r=1: [Edge19]
FEATURE [Part::Cut] Cut1143
  Base = -> Box1062
  Placement = pos=(3,0,0) rot=(0,0,1;0rad)
  Tool = -> Cylinder2982
FEATURE [Part::Fillet] Fillet042
  Base = -> Cut1143
  Edges = 1 edges r=4: [Edge16]
  Placement = pos=(0,-1,0) rot=(0,0,1;0rad)
FEATURE [Part::Cut] Cut1144
  Base = -> Cylinder2983
  Tool = -> Cylinder2984
FEATURE [Part::Cut] Cut1145
  Base = -> Fillet046
  Tool = -> Cylinder2985
FEATURE [Part::Cut] Cut1146
  Base = -> Fillet045
  Tool = -> Cylinder2986
FEATURE [Part::Fillet] Fillet047
  Base = -> Cut1146
  Edges = 1 edges r=3: [Edge9]
FEATURE [Part::Cut] Cut1147
  Base = -> Fillet042
  Tool = -> Compound1328
FEATURE [Part::Cut] Cut1148
  Base = -> Fillet048
  Tool = -> Compound1329
FEATURE [Part::Cut] Cut1149
  Base = -> Cut1148
  Tool = -> Compound1330
FEATURE [Part::Cut] Cut1150
  Base = -> Fillet047
  Tool = -> Compound1331
FEATURE [Part::Cut] Cut1151
  Base = -> Cut1145
  Tool = -> Compound1327
FEATURE [Part::Cut] Cut1152
  Base = -> Cut1144
  Tool = -> Compound1326
FEATURE [Part::Cylinder] Cylinder146  label="Válec146"
  Angle = 360
  AttacherType = Attacher::AttachEngine3D
  Height = 3
  Placement = pos=(1,14,-2) rot=(0,0,1;0rad)
  Radius = 3
FEATURE [Part::Compound] Compound1321
  Links = -> [Cylinder2968,Cylinder146]
  Placement = pos=(12.3,47.5,0) rot=(0,0,1;1.309rad)
FEATURE [Part::Cut] Cut1129
  Base = -> Cut1123
  Tool = -> Compound1321
FEATURE [Part::Cylinder] Cylinder147  label="Válec147"
  Angle = 360
  AttacherType = Attacher::AttachEngine3D
  Height = 20
  Placement = pos=(1,14,1.01) rot=(0,0,1;0rad)
  Radius = 1.5
FEATURE [Part::Cylinder] Cylinder148  label="Válec148"
  Angle = 360
  AttacherType = Attacher::AttachEngine3D
  Height = 3
  Placement = pos=(1,14,-2) rot=(0,0,1;0rad)
  Radius = 3
FEATURE [Part::Compound] Compound1324
  Links = -> [Cylinder147,Cylinder148]
  Placement = pos=(9.4,57.4,0) rot=(0,0,1;0.523599rad)
FEATURE [Part::Cut] Cut1131
  Base = -> Fillet041
  Tool = -> Compound1324
FEATURE [Part::Cut] Cut1133
  Base = -> Cut1131
  Tool = -> Compound1325
FEATURE [Part::Cylinder] Cylinder153  label="Válec153"
  Angle = 360
  AttacherType = Attacher::AttachEngine3D
  Height = 20
  Placement = pos=(1,14,1.01) rot=(0,0,1;0rad)
  Radius = 1.5
FEATURE [Part::Cylinder] Cylinder154  label="Válec154"
  Angle = 360
  AttacherType = Attacher::AttachEngine3D
  Height = 3
  Placement = pos=(1,14,-2) rot=(0,0,1;0rad)
  Radius = 3
FEATURE [Part::Compound] Compound1320
  Links = -> [Cylinder153,Cylinder154]
  Placement = pos=(12.3,47.5,0) rot=(0,0,1;1.309rad)
FEATURE [Part::Cut] Cut1128
  Base = -> Fillet038
  Tool = -> Compound1320
FEATURE [Part::Cut] Cut1134
  Base = -> Cut1128
  Tool = -> Cylinder2971
FEATURE [Part::Cylinder] Cylinder151  label="Válec151"
  Angle = 360
  AttacherType = Attacher::AttachEngine3D
  Height = 20
  Placement = pos=(1,14,1.01) rot=(0,0,1;0rad)
  Radius = 1.5
FEATURE [Part::Cylinder] Cylinder152  label="Válec152"
  Angle = 360
  AttacherType = Attacher::AttachEngine3D
  Height = 3
  Placement = pos=(1,14,-2) rot=(0,0,1;0rad)
  Radius = 3
FEATURE [Part::Compound] Compound1322
  Links = -> [Cylinder151,Cylinder152]
  Placement = pos=(9.4,57.4,0) rot=(0,0,1;0.523599rad)
FEATURE [Part::Cut] Cut1132
  Base = -> Cut1130
  Tool = -> Compound1322
FEATURE [Part::Compound] Compound1332  label="Grip_finger-tip_lower"
  Links = -> [Cut1127,Cut1129,Cut1132,Cut1133,Cut1134]
FEATURE [Part::Compound] Compound1333  label="Grip_finger-root_lower"
  Links = -> [Cut1136,Cut1137,Cut1147,Cut1149,Cut1150,Cut1151,Cut1152]
FEATURE [Mesh::Feature] Mesh001  label="Grip_finger-root_lower (Meshed)"
FEATURE [Mesh::Feature] Mesh002  label="Grip_finger-root_upper (Meshed)"
FEATURE [Mesh::Feature] Mesh003  label="Grip_finger-tip_lower (Meshed)"
FEATURE [Mesh::Feature] Mesh004  label="Grip_finger-tip_upper (Meshed)"
FEATURE [Mesh::Feature] Mesh005  label="Grip_ufo (Meshed)"
FEATURE [Mesh::Feature] Mesh006  label="Grip_slider (Meshed)"
FEATURE [Mesh::Feature] Mesh007  label="Grip_slider-opposite (Meshed)"
FEATURE [Part::FeaturePython] Tube016  # WARN: FeaturePython — macro-defined, semantics opaque (R4)
  AttacherType = Attacher::AttachEngine3D
  Height = 8
  InnerRadius = 64
  OuterRadius = 70
  Placement = pos=(28,22.5,6) rot=(0,0,1;0rad)
FEATURE [Part::Box] Box1066  label="Krychle1065"
  AttacherType = Attacher::AttachEngine3D
  Height = 20
  Length = 100
  Placement = pos=(36,50,0) rot=(0,0,1;1.01229rad)
  Width = 100
FEATURE [Part::Box] Box1067  label="Krychle1066"
  AttacherType = Attacher::AttachEngine3D
  Height = 20
  Length = 100
  Placement = pos=(36,50,0) rot=(0,0,1;3.75246rad)
  Width = 100
FEATURE [Part::Box] Box1068  label="Krychle1067"
  AttacherType = Attacher::AttachEngine3D
  Height = 20
  Length = 100
  Placement = pos=(36,50,0) rot=(0,0,-1;1.16937rad)
  Width = 100
FEATURE [Part::Box] Box1069  label="Krychle1068"
  AttacherType = Attacher::AttachEngine3D
  Height = 20
  Length = 100
  Placement = pos=(36,50,0) rot=(0,0,-1;0.401426rad)
  Width = 100
FEATURE [Part::Cut] Cut1153
  Base = -> Tube016
  Tool = -> Box1066
FEATURE [Part::Cut] Cut1154
  Base = -> Cut1153
  Tool = -> Box1069
FEATURE [Part::Cut] Cut1155
  Base = -> Cut1154
  Tool = -> Box1068
FEATURE [Part::Cut] Cut1156
  Base = -> Cut1155
  Tool = -> Box1067
FEATURE [Part::Cylinder] Cylinder2991  label="Válec2961"
  Angle = 360
  AttacherType = Attacher::AttachEngine3D
  Height = 8
  Placement = pos=(-8,75,6) rot=(0,0,1;0rad)
  Radius = 5
FEATURE [Part::Cylinder] Cylinder2992  label="Válec2962"
  Angle = 360
  AttacherType = Attacher::AttachEngine3D
  Height = 12
  Placement = pos=(-8,75,4) rot=(0,0,1;0rad)
  Radius = 2.65
FEATURE [Part::Cylinder] Cylinder2993  label="Válec2963"
  Angle = 360
  AttacherType = Attacher::AttachEngine3D
  Height = 12
  Placement = pos=(-8,75,4) rot=(0,0,1;0rad)
  Radius = 2.65
FEATURE [Part::Cylinder] Cylinder2994  label="Válec2964"
  Angle = 360
  AttacherType = Attacher::AttachEngine3D
  Height = 8
  Placement = pos=(-23,10,6) rot=(0,0,1;0rad)
  Radius = 5
FEATURE [Part::Cut] Cut1157
  Base = -> Cut1156
  Tool = -> Cylinder2992
FEATURE [Part::Cut] Cut1158
  Base = -> Cylinder2991
  Tool = -> Cylinder2993
FEATURE [Part::Box] Box1070  label="Krychle1069"
  AttacherType = Attacher::AttachEngine3D
  Height = 20
  Length = 100
  Placement = pos=(36,50,0) rot=(0,0,1;3.75246rad)
  Width = 100
FEATURE [Part::Box] Box1071  label="Krychle1070"
  AttacherType = Attacher::AttachEngine3D
  Height = 20
  Length = 100
  Placement = pos=(36,50,0) rot=(0,0,-1;1.16937rad)
  Width = 100
FEATURE [Part::Box] Box1072  label="Krychle1071"
  AttacherType = Attacher::AttachEngine3D
  Height = 20
  Length = 100
  Placement = pos=(36,50,0) rot=(0,0,-1;0.401426rad)
  Width = 100
FEATURE [Part::Box] Box1073  label="Krychle1072"
  AttacherType = Attacher::AttachEngine3D
  Height = 20
  Length = 100
  Placement = pos=(30,35.5,0) rot=(0,0,1;1.0472rad)
  Width = 100
FEATURE [Part::FeaturePython] Tube017  # WARN: FeaturePython — macro-defined, semantics opaque (R4)
  AttacherType = Attacher::AttachEngine3D
  Height = 8
  InnerRadius = 64
  OuterRadius = 70
  Placement = pos=(30,35.5,6) rot=(0,0,1;0rad)
FEATURE [Part::Cylinder] Cylinder2995  label="Válec2965"
  Angle = 360
  AttacherType = Attacher::AttachEngine3D
  Height = 8
  Placement = pos=(-28,69,6) rot=(0,0,1;0rad)
  Radius = 5
FEATURE [Part::Cylinder] Cylinder2996  label="Válec2966"
  Angle = 360
  AttacherType = Attacher::AttachEngine3D
  Height = 12
  Placement = pos=(-28,69,4) rot=(0,0,1;0rad)
  Radius = 2.65
FEATURE [Part::Box] Box1074  label="Krychle1073"
  AttacherType = Attacher::AttachEngine3D
  Height = 20
  Length = 100
  Placement = pos=(30,35.5,0) rot=(0,0,1;3.75246rad)
  Width = 100
FEATURE [Part::Box] Box1075  label="Krychle1074"
  AttacherType = Attacher::AttachEngine3D
  Height = 20
  Length = 100
  Placement = pos=(30,35.5,0) rot=(0,0,1;0.349066rad)
  Width = 100
FEATURE [Part::Box] Box1076  label="Krychle1075"
  AttacherType = Attacher::AttachEngine3D
  Height = 20
  Length = 100
  Placement = pos=(30,35.5,0) rot=(0,0,-1;1.0472rad)
  Width = 100
FEATURE [Part::Cut] Cut1159
  Base = -> Tube017
  Tool = -> Box1074
FEATURE [Part::Cut] Cut1160
  Base = -> Cut1159
  Tool = -> Box1076
FEATURE [Part::Cut] Cut1161
  Base = -> Cut1160
  Tool = -> Box1075
FEATURE [Part::Cut] Cut1162
  Base = -> Cut1161
  Tool = -> Box1073
FEATURE [Part::Cylinder] Cylinder2997  label="Válec2967"
  Angle = 360
  AttacherType = Attacher::AttachEngine3D
  Height = 12
  Placement = pos=(-28,69,4) rot=(0,0,1;0rad)
  Radius = 2.65
FEATURE [Part::Cut] Cut1163
  Base = -> Cut1162
  Tool = -> Cylinder2997
FEATURE [Part::Cut] Cut1164
  Base = -> Cylinder2995
  Tool = -> Cylinder2996
FEATURE [Part::Cylinder] Cylinder2998  label="Válec2968"
  Angle = 360
  AttacherType = Attacher::AttachEngine3D
  Height = 8
  Placement = pos=(-24.5,-3,6) rot=(0,0,1;0rad)
  Radius = 5
FEATURE [Part::Compound] Compound1334  label="Grip_finger-dual-rod"
  Links = -> [Cut1163,Cut1164,Cylinder2998,Compound141]
FEATURE [Part::FeaturePython] Tube018  # WARN: FeaturePython — macro-defined, semantics opaque (R4)
  AttacherType = Attacher::AttachEngine3D
  Height = 8
  InnerRadius = 58
  OuterRadius = 64
  Placement = pos=(37,-1.5,6) rot=(0,0,1;0rad)
FEATURE [Part::FeaturePython] Tube019  # WARN: FeaturePython — macro-defined, semantics opaque (R4)
  AttacherType = Attacher::AttachEngine3D
  Height = 8
  InnerRadius = 58
  OuterRadius = 60
  Placement = pos=(37,-1.5,6) rot=(0,0,1;0rad)
FEATURE [Part::FeaturePython] Tube020  # WARN: FeaturePython — macro-defined, semantics opaque (R4)
  AttacherType = Attacher::AttachEngine3D
  Height = 8
  InnerRadius = 42
  OuterRadius = 46
  Placement = pos=(-4,35.5,6) rot=(0,0,1;0rad)
FEATURE [Part::Cylinder] Cylinder2999  label="Válec2969"
  Angle = 360
  AttacherType = Attacher::AttachEngine3D
  Height = 12
  Placement = pos=(-13,-25,4) rot=(0,0,1;0rad)
  Radius = 2.65
FEATURE [Part::Cylinder] Cylinder3000  label="Válec2970"
  Angle = 360
  AttacherType = Attacher::AttachEngine3D
  Height = 8
  Placement = pos=(-24.5,-3,6) rot=(0,0,1;0rad)
  Radius = 5
FEATURE [Part::Box] Box1077  label="Krychle1076"
  AttacherType = Attacher::AttachEngine3D
  Height = 20
  Length = 100
  Placement = pos=(36,0,0) rot=(0,0,1;1.01229rad)
  Width = 100
FEATURE [Part::Cylinder] Cylinder3001  label="Válec2971"
  Angle = 360
  AttacherType = Attacher::AttachEngine3D
  Height = 12
  Placement = pos=(-8,-40,4) rot=(0,0,1;0rad)
  Radius = 2.65
FEATURE [Part::Cylinder] Cylinder3002  label="Válec2972"
  Angle = 360
  AttacherType = Attacher::AttachEngine3D
  Height = 8
  Placement = pos=(-13,-25,6) rot=(0,0,1;0rad)
  Radius = 5
FEATURE [Part::Cut] Cut1177
  Base = -> Cylinder3002
  Placement = pos=(5,-15,0) rot=(0,0,1;0rad)
  Tool = -> Cylinder2999
FEATURE [Part::Box] Box1078  label="Krychle1077"
  AttacherType = Attacher::AttachEngine3D
  Height = 20
  Length = 100
  Placement = pos=(36,0,0) rot=(0,0,1;3.89208rad)
  Width = 100
FEATURE [Part::Cylinder] Cylinder3003  label="Válec2973"
  Angle = 360
  AttacherType = Attacher::AttachEngine3D
  Height = 12
  Placement = pos=(-13,30,4) rot=(0,0,1;0rad)
  Radius = 2.65
FEATURE [Part::Compound] Compound1337
  Links = -> [Cylinder3003,Cylinder3001]
FEATURE [Part::Cut] Cut1182
  Base = -> Tube018
  Tool = -> Compound1337
FEATURE [Part::Cut] Cut1176
  Base = -> Cut1182
  Tool = -> Box1077
FEATURE [Part::Cylinder] Cylinder3004  label="Válec2974"
  Angle = 360
  AttacherType = Attacher::AttachEngine3D
  Height = 8
  Placement = pos=(-10,30,6) rot=(0,0,1;0rad)
  Radius = 5
FEATURE [Part::Box] Box1079  label="Krychle1078"
  AttacherType = Attacher::AttachEngine3D
  Height = 20
  Length = 100
  Placement = pos=(36,0,0) rot=(0,0,-1;1.16937rad)
  Width = 100
FEATURE [Part::Cylinder] Cylinder3005  label="Válec2975"
  Angle = 360
  AttacherType = Attacher::AttachEngine3D
  Height = 12
  Placement = pos=(-28,69,4) rot=(0,0,1;0rad)
  Radius = 2.65
FEATURE [Part::Cylinder] Cylinder3006  label="Válec2976"
  Angle = 360
  AttacherType = Attacher::AttachEngine3D
  Height = 12
  Placement = pos=(-10,30,4) rot=(0,0,1;0rad)
  Radius = 2.65
FEATURE [Part::Cut] Cut1181
  Base = -> Cylinder3004
  Placement = pos=(-3,0,0) rot=(0,0,1;0rad)
  Tool = -> Cylinder3006
FEATURE [Part::Compound] Compound1335  label="tahlo_lefto006"
  Links = -> [Cut1181,Cut1177]
FEATURE [Part::Box] Box1080  label="Krychle1079"
  AttacherType = Attacher::AttachEngine3D
  Height = 20
  Length = 100
  Placement = pos=(36,0,0) rot=(0,0,-1;0.401426rad)
  Width = 100
FEATURE [Part::Cut] Cut1179
  Base = -> Cut1176
  Tool = -> Box1080
FEATURE [Part::Cut] Cut1180
  Base = -> Cut1179
  Tool = -> Box1079
FEATURE [Part::Cut] Cut1178
  Base = -> Cut1180
  Tool = -> Box1078
FEATURE [Part::Cylinder] Cylinder3007  label="Válec2977"
  Angle = 360
  AttacherType = Attacher::AttachEngine3D
  Height = 8
  Placement = pos=(-28,69,6) rot=(0,0,1;0rad)
  Radius = 5
FEATURE [Part::Cut] Cut1184
  Base = -> Cylinder3007
  Tool = -> Cylinder3005
FEATURE [Part::Cylinder] Cylinder3008  label="Válec2978"
  Angle = 360
  AttacherType = Attacher::AttachEngine3D
  Height = 12
  Placement = pos=(-8,-40,4) rot=(0,0,1;0rad)
  Radius = 2.65
FEATURE [Part::Box] Box1081  label="Krychle1080"
  AttacherType = Attacher::AttachEngine3D
  Height = 20
  Length = 100
  Placement = pos=(36,0,0) rot=(0,0,1;1.01229rad)
  Width = 100
FEATURE [Part::Box] Box1082  label="Krychle1081"
  AttacherType = Attacher::AttachEngine3D
  Height = 20
  Length = 100
  Placement = pos=(36,0,0) rot=(0,0,1;3.89208rad)
  Width = 100
FEATURE [Part::Box] Box1083  label="Krychle1082"
  AttacherType = Attacher::AttachEngine3D
  Height = 20
  Length = 100
  Placement = pos=(36,0,0) rot=(0,0,-1;0.401426rad)
  Width = 100
FEATURE [Part::Cylinder] Cylinder3009  label="Válec2979"
  Angle = 360
  AttacherType = Attacher::AttachEngine3D
  Height = 12
  Placement = pos=(-13,30,4) rot=(0,0,1;0rad)
  Radius = 2.65
FEATURE [Part::Compound] Compound1338
  Links = -> [Cylinder3009,Cylinder3008]
FEATURE [Part::Cut] Cut1169
  Base = -> Tube019
  Tool = -> Compound1338
FEATURE [Part::Cut] Cut1165
  Base = -> Cut1169
  Tool = -> Box1081
FEATURE [Part::Cut] Cut1167
  Base = -> Cut1165
  Tool = -> Box1083
FEATURE [Part::Box] Box1084  label="Krychle1083"
  AttacherType = Attacher::AttachEngine3D
  Height = 20
  Length = 100
  Placement = pos=(36,0,0) rot=(0,0,-1;1.16937rad)
  Width = 100
FEATURE [Part::Cut] Cut1168
  Base = -> Cut1167
  Tool = -> Box1084
FEATURE [Part::Cut] Cut1166
  Base = -> Cut1168
  Tool = -> Box1082
FEATURE [Part::Cylinder] Cylinder3010  label="Válec2980"
  Angle = 360
  AttacherType = Attacher::AttachEngine3D
  Height = 12
  Placement = pos=(-28,69,4) rot=(0,0,1;0rad)
  Radius = 2.65
FEATURE [Part::Box] Box1085  label="Krychle1084"
  AttacherType = Attacher::AttachEngine3D
  Height = 20
  Length = 100
  Placement = pos=(36,0,0) rot=(0,0,1;3.19395rad)
  Width = 100
FEATURE [Part::Cut] Cut1183
  Base = -> Cut1166
  Tool = -> Box1085
FEATURE [Part::Cut] Cut1170
  Base = -> Cut1178
  Tool = -> Cut1183
FEATURE [Part::Box] Box1086  label="Krychle1085"
  AttacherType = Attacher::AttachEngine3D
  Height = 20
  Length = 100
  Placement = pos=(-4,35.5,0) rot=(0,0,1;0.628319rad)
  Width = 100
FEATURE [Part::Box] Box1087  label="Krychle1086"
  AttacherType = Attacher::AttachEngine3D
  Height = 20
  Length = 100
  Placement = pos=(-4,35.5,0) rot=(0,0,-1;1.0472rad)
  Width = 100
FEATURE [Part::Box] Box1088  label="Krychle1087"
  AttacherType = Attacher::AttachEngine3D
  Height = 20
  Length = 100
  Placement = pos=(-4,35.5,0) rot=(0,0,-1;2.07694rad)
  Width = 100
FEATURE [Part::Cut] Cut1171
  Base = -> Tube020
  Tool = -> Box1088
FEATURE [Part::Cut] Cut1172
  Base = -> Cut1171
  Tool = -> Box1087
FEATURE [Part::Box] Box1089  label="Krychle1088"
  AttacherType = Attacher::AttachEngine3D
  Height = 20
  Length = 100
  Placement = pos=(-4,35.5,0) rot=(0,0,1;0.349066rad)
  Width = 100
FEATURE [Part::Cut] Cut1174
  Base = -> Cut1172
  Tool = -> Box1089
FEATURE [Part::Cut] Cut1175
  Base = -> Cut1174
  Tool = -> Box1086
FEATURE [Part::Cut] Cut1173
  Base = -> Cut1175
  Tool = -> Cylinder3010
FEATURE [Part::Compound] Compound1336  label="Grip_finger-dual-rod-thin"
  Links = -> [Compound1335,Cylinder3000,Cut1184,Cut1170,Cut1173]
FEATURE [Part::Cylinder] Cylinder3011  label="Válec2981"
  Angle = 360
  AttacherType = Attacher::AttachEngine3D
  Height = 10
  Placement = pos=(-11,62.5,1) rot=(0,0,1;0rad)
  Radius = 5
FEATURE [Part::Cylinder] Cylinder3012  label="Válec2982"
  Angle = 360
  AttacherType = Attacher::AttachEngine3D
  Height = 7
  Placement = pos=(-8,61,-2) rot=(0,0,1;0rad)
  Radius = 8
FEATURE [Part::Cut] Cut1186
  Base = -> Cylinder3012
  Tool = -> Cylinder3011
FEATURE [Part::Box] Box1090  label="Krychle1089"
  AttacherType = Attacher::AttachEngine3D
  Height = 2
  Length = 6
  Placement = pos=(-2,11,2) rot=(0,0,1;0rad)
  Width = 6
FEATURE [Part::Cylinder] Cylinder3013  label="Válec2983"
  Angle = 360
  AttacherType = Attacher::AttachEngine3D
  Height = 10
  Placement = pos=(-9,61,5) rot=(0,0,1;0rad)
  Radius = 10
FEATURE [Part::Cylinder] Cylinder3014  label="Válec2984"
  Angle = 360
  AttacherType = Attacher::AttachEngine3D
  Height = 20
  Placement = pos=(1,14,4.01) rot=(0,0,1;0rad)
  Radius = 1.5
FEATURE [Part::Cylinder] Cylinder3015  label="Válec2985"
  Angle = 360
  AttacherType = Attacher::AttachEngine3D
  Height = 20
  Placement = pos=(1,14,4.01) rot=(0,0,1;0rad)
  Radius = 1.5
FEATURE [Part::Cylinder] Cylinder3016  label="Válec2986"
  Angle = 360
  AttacherType = Attacher::AttachEngine3D
  Height = 3
  Placement = pos=(1,14,-1.01) rot=(0,0,1;0rad)
  Radius = 1.5
FEATURE [Part::Box] Box1091  label="Krychle1090"
  AttacherType = Attacher::AttachEngine3D
  Height = 12
  Length = 12
  Placement = pos=(5,60.6,-2) rot=(0,0,1;0.523599rad)
  Width = 12
FEATURE [Part::Fillet] Fillet050
  Base = -> Box1091
  Edges = 1 edges r=4: [Edge5]
FEATURE [Part::Cylinder] Cylinder3017  label="Válec2987"
  Angle = 360
  AttacherType = Attacher::AttachEngine3D
  Height = 10
  Placement = pos=(-8,61,1) rot=(0,0,1;0rad)
  Radius = 5
FEATURE [Part::Cylinder] Cylinder3018  label="Válec2988"
  Angle = 360
  AttacherType = Attacher::AttachEngine3D
  Height = 10
  Placement = pos=(-9,61,5) rot=(0,0,1;0rad)
  Radius = 10
FEATURE [Part::Box] Box1092  label="Krychle1091"
  AttacherType = Attacher::AttachEngine3D
  Height = 12
  Length = 12
  Placement = pos=(-7.85,61.2,-2) rot=(0,0,-1;0.610865rad)
  Width = 12
FEATURE [Part::Cut] Cut1194
  Base = -> Box1092
  Tool = -> Cylinder3013
FEATURE [Part::Cylinder] Cylinder3019  label="Válec2989"
  Angle = 360
  AttacherType = Attacher::AttachEngine3D
  Height = 10
  Placement = pos=(-8,61,1) rot=(0,0,1;0rad)
  Radius = 5
FEATURE [Part::Cylinder] Cylinder3020  label="Válec2990"
  Angle = 360
  AttacherType = Attacher::AttachEngine3D
  Height = 8
  Placement = pos=(-7,41,-2) rot=(0,0,1;0rad)
  Radius = 9
FEATURE [Part::Cylinder] Cylinder3021  label="Válec2991"
  Angle = 360
  AttacherType = Attacher::AttachEngine3D
  Height = 20
  Placement = pos=(1,14,4.01) rot=(0,0,1;0rad)
  Radius = 1.5
FEATURE [Part::Cylinder] Cylinder3022  label="Válec2992"
  Angle = 360
  AttacherType = Attacher::AttachEngine3D
  Height = 4
  Placement = pos=(-7,41,6) rot=(0,0,1;0rad)
  Radius = 6
FEATURE [Part::Box] Box1093  label="Krychle1092"
  AttacherType = Attacher::AttachEngine3D
  Height = 12
  Length = 12
  Placement = pos=(-13,42,-2) rot=(0,0,-1;0.261799rad)
  Width = 20
FEATURE [Part::Cut] Cut1199
  Base = -> Box1093
  Tool = -> Cylinder3020
FEATURE [Part::Cut] Cut1190
  Base = -> Cut1199
  Tool = -> Cylinder3018
FEATURE [Part::Cut] Cut1196
  Base = -> Cut1190
  Tool = -> Cylinder3019
FEATURE [Part::Fillet] Fillet051
  Base = -> Cut1196
  Edges = 1 edges r=2: [Edge3]
FEATURE [Part::Fillet] Fillet049
  Base = -> Fillet051
  Edges = 1 edges r=1: [Edge28]
FEATURE [Part::Cylinder] Cylinder3023  label="Válec2993"
  Angle = 360
  AttacherType = Attacher::AttachEngine3D
  Height = 3
  Placement = pos=(1,14,-1.01) rot=(0,0,1;0rad)
  Radius = 1.5
FEATURE [Part::Cylinder] Cylinder3024  label="Válec2994"
  Angle = 360
  AttacherType = Attacher::AttachEngine3D
  Height = 10
  Placement = pos=(-8,61,1) rot=(0,0,1;0rad)
  Radius = 5
FEATURE [Part::Cut] Cut1195
  Base = -> Cut1194
  Tool = -> Cylinder3024
FEATURE [Part::Fillet] Fillet052
  Base = -> Cut1195
  Edges = 1 edges r=3: [Edge5]
FEATURE [Part::Cut] Cut1187
  Base = -> Fillet052
  Tool = -> Cylinder3017
FEATURE [Part::Cylinder] Cylinder3025  label="Válec2995"
  Angle = 360
  AttacherType = Attacher::AttachEngine3D
  Height = 12
  Placement = pos=(1,14,6) rot=(0,0,1;0rad)
  Radius = 1.5
FEATURE [Part::Cylinder] Cylinder3026  label="Válec2996"
  Angle = 360
  AttacherType = Attacher::AttachEngine3D
  Height = 4
  Placement = pos=(1,14,0) rot=(0,0,1;0rad)
  Radius = 1.5
FEATURE [Part::Cylinder] Cylinder3027  label="Válec2997"
  Angle = 360
  AttacherType = Attacher::AttachEngine3D
  Height = 20
  Placement = pos=(1,14,4.01) rot=(0,0,1;0rad)
  Radius = 1.5
FEATURE [Part::Cylinder] Cylinder3028  label="Válec2998"
  Angle = 360
  AttacherType = Attacher::AttachEngine3D
  Height = 20
  Placement = pos=(1,14,4.01) rot=(0,0,1;0rad)
  Radius = 1.5
FEATURE [Part::Cylinder] Cylinder3029  label="Válec2999"
  Angle = 360
  AttacherType = Attacher::AttachEngine3D
  Height = 3
  Placement = pos=(1,14,-1.01) rot=(0,0,1;0rad)
  Radius = 1.5
FEATURE [Part::Cylinder] Cylinder3030  label="Válec3000"
  Angle = 360
  AttacherType = Attacher::AttachEngine3D
  Height = 3
  Placement = pos=(1,14,-1.01) rot=(0,0,1;0rad)
  Radius = 1.5
FEATURE [Part::Compound] Compound1343
  Links = -> [Box1090,Cylinder3028,Cylinder3030]
  Placement = pos=(9.4,57.4,0) rot=(0,0,1;0.523599rad)
FEATURE [Part::Cut] Cut1192
  Base = -> Fillet050
  Tool = -> Compound1343
FEATURE [Part::Box] Box1094  label="Krychle1093"
  AttacherType = Attacher::AttachEngine3D
  Height = 2
  Length = 6
  Placement = pos=(-2,11,4) rot=(0,0,1;0rad)
  Width = 6
FEATURE [Part::Compound] Compound1345
  Links = -> [Box1094,Cylinder3025,Cylinder3026]
  Placement = pos=(11.7,56.9,2) rot=(-0.250563,0.935113,0.250563;1.63782rad)
FEATURE [Part::Cut] Cut1193
  Base = -> Cut1192
  Tool = -> Compound1345
FEATURE [Part::Box] Box1095  label="Krychle1094"
  AttacherType = Attacher::AttachEngine3D
  Height = 2
  Length = 6
  Placement = pos=(-2,11,2) rot=(0,0,1;0rad)
  Width = 6
FEATURE [Part::Box] Box1096  label="Krychle1095"
  AttacherType = Attacher::AttachEngine3D
  Height = 2
  Length = 6
  Placement = pos=(-2,11,2) rot=(0,0,1;0rad)
  Width = 6
FEATURE [Part::Compound] Compound1342
  Links = -> [Box1096,Cylinder3015,Cylinder3029]
  Placement = pos=(9.4,57.4,0) rot=(0,0,1;0.523599rad)
FEATURE [Part::Box] Box1097  label="Krychle1096"
  AttacherType = Attacher::AttachEngine3D
  Height = 2
  Length = 6
  Placement = pos=(-2,11,2) rot=(0,0,1;0rad)
  Width = 6
FEATURE [Part::Compound] Compound1340
  Links = -> [Box1097,Cylinder3014,Cylinder3016]
  Placement = pos=(12.3,47.5,0) rot=(0,0,1;1.309rad)
FEATURE [Part::Cut] Cut1197
  Base = -> Fillet049
  Tool = -> Compound1340
FEATURE [Part::Box] Box1098  label="Krychle1097"
  AttacherType = Attacher::AttachEngine3D
  Height = 2
  Length = 6
  Placement = pos=(-2,11,2) rot=(0,0,1;0rad)
  Width = 6
FEATURE [Part::Compound] Compound1341
  Links = -> [Box1098,Cylinder3027,Cylinder3023]
  Placement = pos=(12.3,47.5,0) rot=(0,0,1;1.309rad)
FEATURE [Part::Cut] Cut1198
  Base = -> Cut1187
  Tool = -> Compound1341
FEATURE [Part::Cut] Cut1188
  Base = -> Cut1198
  Tool = -> Compound1342
FEATURE [Part::Cylinder] Cylinder3031  label="Válec3001"
  Angle = 360
  AttacherType = Attacher::AttachEngine3D
  Height = 3
  Placement = pos=(1,14,-1.01) rot=(0,0,1;0rad)
  Radius = 1.5
FEATURE [Part::Compound] Compound1339
  Links = -> [Box1095,Cylinder3021,Cylinder3031]
  Placement = pos=(12.3,47.5,0) rot=(0,0,1;1.309rad)
FEATURE [Part::Cut] Cut1189
  Base = -> Cut1186
  Tool = -> Compound1339
FEATURE [Part::Cylinder] Cylinder3032  label="Válec3002"
  Angle = 360
  AttacherType = Attacher::AttachEngine3D
  Height = 6
  Placement = pos=(-7,41,5) rot=(0,0,1;0rad)
  Radius = 2.6
FEATURE [Part::Cut] Cut1185
  Base = -> Cut1197
  Tool = -> Cylinder3032
FEATURE [Part::Cylinder] Cylinder3033  label="Válec3003"
  Angle = 360
  AttacherType = Attacher::AttachEngine3D
  Height = 6
  Placement = pos=(-7,41,5) rot=(0,0,1;0rad)
  Radius = 2.6
FEATURE [Part::Cut] Cut1191
  Base = -> Cylinder3022
  Tool = -> Cylinder3033
FEATURE [Part::Compound] Compound1344  label="Grip_finger-tip_upper-revised"
  Links = -> [Cut1191,Cut1193,Cut1188,Cut1189,Cut1185]
FEATURE [Part::Cylinder] Cylinder3034  label="Válec3004"
  Angle = 360
  AttacherType = Attacher::AttachEngine3D
  Height = 3
  Placement = pos=(1,14,-2) rot=(0,0,1;0rad)
  Radius = 3
FEATURE [Part::Cylinder] Cylinder3035  label="Válec3005"
  Angle = 360
  AttacherType = Attacher::AttachEngine3D
  Height = 20
  Placement = pos=(1,14,1.01) rot=(0,0,1;0rad)
  Radius = 1.5
FEATURE [Part::Cylinder] Cylinder3036  label="Válec3006"
  Angle = 360
  AttacherType = Attacher::AttachEngine3D
  Height = 10
  Placement = pos=(-8,61,1) rot=(0,0,1;0rad)
  Radius = 5
FEATURE [Part::Cylinder] Cylinder3037  label="Válec3007"
  Angle = 360
  AttacherType = Attacher::AttachEngine3D
  Height = 8
  Placement = pos=(-7,41,-2) rot=(0,0,1;0rad)
  Radius = 9
FEATURE [Part::Cylinder] Cylinder3038  label="Válec3008"
  Angle = 360
  AttacherType = Attacher::AttachEngine3D
  Height = 4
  Placement = pos=(-7,41,6) rot=(0,0,1;0rad)
  Radius = 6
FEATURE [Part::Cylinder] Cylinder3039  label="Válec3009"
  Angle = 360
  AttacherType = Attacher::AttachEngine3D
  Height = 4
  Placement = pos=(1,14,0) rot=(0,0,1;0rad)
  Radius = 1.5
FEATURE [Part::Cylinder] Cylinder3040  label="Válec3010"
  Angle = 360
  AttacherType = Attacher::AttachEngine3D
  Height = 7
  Placement = pos=(-8,61,-2) rot=(0,0,1;0rad)
  Radius = 8
FEATURE [Part::Cylinder] Cylinder3041  label="Válec3011"
  Angle = 360
  AttacherType = Attacher::AttachEngine3D
  Height = 10
  Placement = pos=(-11,62.5,1) rot=(0,0,1;0rad)
  Radius = 5
FEATURE [Part::Cut] Cut1200
  Base = -> Cylinder3040
  Tool = -> Cylinder3041
FEATURE [Part::Cylinder] Cylinder3042  label="Válec3012"
  Angle = 360
  AttacherType = Attacher::AttachEngine3D
  Height = 10
  Placement = pos=(-9,61,5) rot=(0,0,1;0rad)
  Radius = 10
FEATURE [Part::Box] Box1099  label="Krychle1098"
  AttacherType = Attacher::AttachEngine3D
  Height = 12
  Length = 12
  Placement = pos=(-13,42,-2) rot=(0,0,-1;0.261799rad)
  Width = 20
FEATURE [Part::Cylinder] Cylinder3043  label="Válec3013"
  Angle = 360
  AttacherType = Attacher::AttachEngine3D
  Height = 10
  Placement = pos=(-9,61,5) rot=(0,0,1;0rad)
  Radius = 10
FEATURE [Part::Cylinder] Cylinder3044  label="Válec3014"
  Angle = 360
  AttacherType = Attacher::AttachEngine3D
  Height = 20
  Placement = pos=(1,14,1.01) rot=(0,0,1;0rad)
  Radius = 1.5
FEATURE [Part::Compound] Compound1348
  Links = -> [Cylinder3044,Cylinder3034]
  Placement = pos=(12.3,47.5,0) rot=(0,0,1;1.309rad)
FEATURE [Part::Cylinder] Cylinder3045  label="Válec3015"
  Angle = 360
  AttacherType = Attacher::AttachEngine3D
  Height = 6
  Placement = pos=(-7,41,5) rot=(0,0,1;0rad)
  Radius = 2.6
FEATURE [Part::Cut] Cut1204
  Base = -> Cylinder3038
  Tool = -> Cylinder3045
FEATURE [Part::Cylinder] Cylinder3046  label="Válec3016"
  Angle = 360
  AttacherType = Attacher::AttachEngine3D
  Height = 3
  Placement = pos=(1,14,-2) rot=(0,0,1;0rad)
  Radius = 3
FEATURE [Part::Cylinder] Cylinder3047  label="Válec3017"
  Angle = 360
  AttacherType = Attacher::AttachEngine3D
  Height = 12
  Placement = pos=(1,14,6) rot=(0,0,1;0rad)
  Radius = 1.5
FEATURE [Part::Cylinder] Cylinder3048  label="Válec3018"
  Angle = 360
  AttacherType = Attacher::AttachEngine3D
  Height = 10
  Placement = pos=(-8,61,1) rot=(0,0,1;0rad)
  Radius = 5
FEATURE [Part::Box] Box1100  label="Krychle1099"
  AttacherType = Attacher::AttachEngine3D
  Height = 2
  Length = 6
  Placement = pos=(-2,11,4) rot=(0,0,1;0rad)
  Width = 6
FEATURE [Part::Compound] Compound1351
  Links = -> [Box1100,Cylinder3047,Cylinder3039]
  Placement = pos=(11.7,56.9,2) rot=(-0.250563,0.935113,0.250563;1.63782rad)
FEATURE [Part::Cylinder] Cylinder3049  label="Válec3019"
  Angle = 360
  AttacherType = Attacher::AttachEngine3D
  Height = 20
  Placement = pos=(1,14,1.01) rot=(0,0,1;0rad)
  Radius = 1.5
FEATURE [Part::Cylinder] Cylinder3050  label="Válec3020"
  Angle = 360
  AttacherType = Attacher::AttachEngine3D
  Height = 20
  Placement = pos=(1,14,1.01) rot=(0,0,1;0rad)
  Radius = 1.5
FEATURE [Part::Box] Box1101  label="Krychle1100"
  AttacherType = Attacher::AttachEngine3D
  Height = 12
  Length = 12
  Placement = pos=(5,60.6,-2) rot=(0,0,1;0.523599rad)
  Width = 12
FEATURE [Part::Fillet] Fillet053
  Base = -> Box1101
  Edges = 1 edges r=4: [Edge5]
FEATURE [Part::Box] Box1102  label="Krychle1101"
  AttacherType = Attacher::AttachEngine3D
  Height = 12
  Length = 12
  Placement = pos=(-7.85,61.2,-2) rot=(0,0,-1;0.610865rad)
  Width = 12
FEATURE [Part::Cylinder] Cylinder3051  label="Válec3021"
  Angle = 360
  AttacherType = Attacher::AttachEngine3D
  Height = 3
  Placement = pos=(1,14,-2) rot=(0,0,1;0rad)
  Radius = 3
FEATURE [Part::Compound] Compound1350
  Links = -> [Cylinder3049,Cylinder3051]
  Placement = pos=(9.4,57.4,0) rot=(0,0,1;0.523599rad)
FEATURE [Part::Cylinder] Cylinder3052  label="Válec3022"
  Angle = 360
  AttacherType = Attacher::AttachEngine3D
  Height = 3
  Placement = pos=(1,14,-2) rot=(0,0,1;0rad)
  Radius = 3
FEATURE [Part::Compound] Compound1347
  Links = -> [Cylinder3050,Cylinder3052]
  Placement = pos=(9.4,57.4,0) rot=(0,0,1;0.523599rad)
FEATURE [Part::Cylinder] Cylinder3053  label="Válec3023"
  Angle = 360
  AttacherType = Attacher::AttachEngine3D
  Height = 20
  Placement = pos=(1,14,1.01) rot=(0,0,1;0rad)
  Radius = 1.5
FEATURE [Part::Compound] Compound1349
  Links = -> [Cylinder3053,Cylinder3046]
  Placement = pos=(12.3,47.5,0) rot=(0,0,1;1.309rad)
FEATURE [Part::Cylinder] Cylinder3054  label="Válec3024"
  Angle = 360
  AttacherType = Attacher::AttachEngine3D
  Height = 3
  Placement = pos=(1,14,-2) rot=(0,0,1;0rad)
  Radius = 3
FEATURE [Part::Compound] Compound1346
  Links = -> [Cylinder3035,Cylinder3054]
  Placement = pos=(12.3,47.5,0) rot=(0,0,1;1.309rad)
FEATURE [Part::Cylinder] Cylinder3055  label="Válec3025"
  Angle = 360
  AttacherType = Attacher::AttachEngine3D
  Height = 10
  Placement = pos=(-8,61,1) rot=(0,0,1;0rad)
  Radius = 5
FEATURE [Part::Cylinder] Cylinder3056  label="Válec3026"
  Angle = 360
  AttacherType = Attacher::AttachEngine3D
  Height = 6
  Placement = pos=(-7,41,5) rot=(0,0,1;0rad)
  Radius = 2.6
FEATURE [Part::Cut] Cut1207
  Base = -> Box1102
  Tool = -> Cylinder3043
FEATURE [Part::Cut] Cut1206
  Base = -> Cut1207
  Tool = -> Cylinder3055
FEATURE [Part::Fillet] Fillet055
  Base = -> Cut1206
  Edges = 1 edges r=3: [Edge5]
FEATURE [Part::Cut] Cut1209
  Base = -> Cut1200
  Tool = -> Compound1346
FEATURE [Part::Cut] Cut1212
  Base = -> Fillet053
  Tool = -> Compound1350
FEATURE [Part::Cut] Cut1203
  Base = -> Cut1212
  Tool = -> Compound1351
FEATURE [Part::Cut] Cut1213
  Base = -> Fillet055
  Tool = -> Cylinder3048
FEATURE [Part::Cut] Cut1202
  Base = -> Cut1213
  Tool = -> Compound1348
FEATURE [Part::Cut] Cut1208
  Base = -> Cut1202
  Tool = -> Compound1347
FEATURE [Part::Cut] Cut1214
  Base = -> Box1099
  Tool = -> Cylinder3037
FEATURE [Part::Cut] Cut1201
  Base = -> Cut1214
  Tool = -> Cylinder3042
FEATURE [Part::Cut] Cut1211
  Base = -> Cut1201
  Tool = -> Cylinder3036
FEATURE [Part::Fillet] Fillet054
  Base = -> Cut1211
  Edges = 1 edges r=2: [Edge3]
FEATURE [Part::Fillet] Fillet056
  Base = -> Fillet054
  Edges = 1 edges r=1: [Edge28]
FEATURE [Part::Cut] Cut1205
  Base = -> Fillet056
  Tool = -> Compound1349
FEATURE [Part::Cut] Cut1210
  Base = -> Cut1205
  Tool = -> Cylinder3056
FEATURE [Part::Compound] Compound1352  label="Grip_finger-tip_lower-revised"
  Links = -> [Cut1204,Cut1209,Cut1208,Cut1203,Cut1210]
FEATURE [Part::Cylinder] Cylinder3057  label="Válec3027"
  Angle = 360
  AttacherType = Attacher::AttachEngine3D
  Height = 12
  Placement = pos=(-13,-25,4) rot=(0,0,1;0rad)
  Radius = 2.65
FEATURE [Part::Box] Box1103  label="Krychle1102"
  AttacherType = Attacher::AttachEngine3D
  Height = 20
  Length = 100
  Placement = pos=(36,0,0) rot=(0,0,-1;1.16937rad)
  Width = 100
FEATURE [Part::Cylinder] Cylinder3058  label="Válec3028"
  Angle = 360
  AttacherType = Attacher::AttachEngine3D
  Height = 8
  Placement = pos=(-10,30,6) rot=(0,0,1;0rad)
  Radius = 5
FEATURE [Part::Box] Box1104  label="Krychle1103"
  AttacherType = Attacher::AttachEngine3D
  Height = 20
  Length = 100
  Placement = pos=(36,0,0) rot=(0,0,1;1.01229rad)
  Width = 100
FEATURE [Part::Cylinder] Cylinder3059  label="Válec3029"
  Angle = 360
  AttacherType = Attacher::AttachEngine3D
  Height = 12
  Placement = pos=(-28,69,4) rot=(0,0,1;0rad)
  Radius = 2.65
FEATURE [Part::Cylinder] Cylinder3060  label="Válec3030"
  Angle = 360
  AttacherType = Attacher::AttachEngine3D
  Height = 12
  Placement = pos=(-13,30,4) rot=(0,0,1;0rad)
  Radius = 2.65
FEATURE [Part::Box] Box1105  label="Krychle1104"
  AttacherType = Attacher::AttachEngine3D
  Height = 20
  Length = 100
  Placement = pos=(36,0,0) rot=(0,0,1;3.89208rad)
  Width = 100
FEATURE [Part::Cylinder] Cylinder3061  label="Válec3031"
  Angle = 360
  AttacherType = Attacher::AttachEngine3D
  Height = 8
  Placement = pos=(-24.5,-3,6) rot=(0,0,1;0rad)
  Radius = 5
FEATURE [Part::Cylinder] Cylinder3062  label="Válec3032"
  Angle = 360
  AttacherType = Attacher::AttachEngine3D
  Height = 8
  Placement = pos=(-28,69,6) rot=(0,0,1;0rad)
  Radius = 5
FEATURE [Part::Box] Box1106  label="Krychle1105"
  AttacherType = Attacher::AttachEngine3D
  Height = 20
  Length = 100
  Placement = pos=(36,0,0) rot=(0,0,1;3.19395rad)
  Width = 100
FEATURE [Part::Cylinder] Cylinder3063  label="Válec3033"
  Angle = 360
  AttacherType = Attacher::AttachEngine3D
  Height = 12
  Placement = pos=(-8,-40,4) rot=(0,0,1;0rad)
  Radius = 2.65
FEATURE [Part::Box] Box1107  label="Krychle1106"
  AttacherType = Attacher::AttachEngine3D
  Height = 20
  Length = 200
  Placement = pos=(-4,35.5,0) rot=(0,0,1;0.663225rad)
  Width = 200
FEATURE [Part::Box] Box1108  label="Krychle1107"
  AttacherType = Attacher::AttachEngine3D
  Height = 20
  Length = 100
  Placement = pos=(36,0,0) rot=(0,0,1;1.01229rad)
  Width = 100
FEATURE [Part::Box] Box1109  label="Krychle1108"
  AttacherType = Attacher::AttachEngine3D
  Height = 20
  Length = 200
  Placement = pos=(-4,35.5,0) rot=(0,0,-1;2.07694rad)
  Width = 200
FEATURE [Part::Box] Box1110  label="Krychle1109"
  AttacherType = Attacher::AttachEngine3D
  Height = 20
  Length = 100
  Placement = pos=(36,0,0) rot=(0,0,-1;0.401426rad)
  Width = 100
FEATURE [Part::Box] Box1111  label="Krychle1110"
  AttacherType = Attacher::AttachEngine3D
  Height = 20
  Length = 100
  Placement = pos=(36,0,0) rot=(0,0,-1;0.401426rad)
  Width = 100
FEATURE [Part::Cylinder] Cylinder3064  label="Válec3034"
  Angle = 360
  AttacherType = Attacher::AttachEngine3D
  Height = 8
  Placement = pos=(-13,-25,6) rot=(0,0,1;0rad)
  Radius = 5
FEATURE [Part::Box] Box1112  label="Krychle1111"
  AttacherType = Attacher::AttachEngine3D
  Height = 20
  Length = 200
  Placement = pos=(-4,35.5,0) rot=(0,0,-1;1.0472rad)
  Width = 200
FEATURE [Part::Cylinder] Cylinder3065  label="Válec3035"
  Angle = 360
  AttacherType = Attacher::AttachEngine3D
  Height = 12
  Placement = pos=(-28,69,4) rot=(0,0,1;0rad)
  Radius = 2.65
FEATURE [Part::Box] Box1113  label="Krychle1112"
  AttacherType = Attacher::AttachEngine3D
  Height = 20
  Length = 100
  Placement = pos=(36,0,0) rot=(0,0,1;3.89208rad)
  Width = 100
FEATURE [Part::Cylinder] Cylinder3066  label="Válec3036"
  Angle = 360
  AttacherType = Attacher::AttachEngine3D
  Height = 12
  Placement = pos=(-13,30,4) rot=(0,0,1;0rad)
  Radius = 2.65
FEATURE [Part::Cylinder] Cylinder3067  label="Válec3037"
  Angle = 360
  AttacherType = Attacher::AttachEngine3D
  Height = 12
  Placement = pos=(-10,30,4) rot=(0,0,1;0rad)
  Radius = 2.65
FEATURE [Part::Box] Box1114  label="Krychle1113"
  AttacherType = Attacher::AttachEngine3D
  Height = 20
  Length = 100
  Placement = pos=(36,0,0) rot=(0,0,-1;1.16937rad)
  Width = 100
FEATURE [Part::Cylinder] Cylinder3068  label="Válec3038"
  Angle = 360
  AttacherType = Attacher::AttachEngine3D
  Height = 12
  Placement = pos=(-8,-40,4) rot=(0,0,1;0rad)
  Radius = 2.65
FEATURE [Part::Box] Box1115  label="Krychle1114"
  AttacherType = Attacher::AttachEngine3D
  Height = 20
  Length = 200
  Placement = pos=(-4,35.5,0) rot=(0,0,1;0.349066rad)
  Width = 200
FEATURE [Part::Compound] Compound1354
  Links = -> [Cylinder3060,Cylinder3068]
FEATURE [Part::Compound] Compound1355
  Links = -> [Cylinder3066,Cylinder3063]
FEATURE [Part::FeaturePython] Tube021  # WARN: FeaturePython — macro-defined, semantics opaque (R4)
  AttacherType = Attacher::AttachEngine3D
  Height = 8
  InnerRadius = 58
  OuterRadius = 60
  Placement = pos=(37,-1.5,6) rot=(0,0,1;0rad)
FEATURE [Part::FeaturePython] Tube022  # WARN: FeaturePython — macro-defined, semantics opaque (R4)
  AttacherType = Attacher::AttachEngine3D
  Height = 8
  InnerRadius = 58
  OuterRadius = 64
  Placement = pos=(37,-1.5,6) rot=(0,0,1;0rad)
FEATURE [Part::FeaturePython] Tube023  # WARN: FeaturePython — macro-defined, semantics opaque (R4)
  AttacherType = Attacher::AttachEngine3D
  Height = 8
  InnerRadius = 95
  OuterRadius = 100
  Placement = pos=(63,39.5,6) rot=(0,0,1;0rad)
FEATURE [Part::Cut] Cut1215
  Base = -> Tube022
  Tool = -> Compound1354
FEATURE [Part::Cut] Cut1217
  Base = -> Tube023
  Tool = -> Box1109
FEATURE [Part::Cut] Cut1220
  Base = -> Cut1215
  Tool = -> Box1104
FEATURE [Part::Cut] Cut1221
  Base = -> Cylinder3064
  Placement = pos=(5,-15,0) rot=(0,0,1;0rad)
  Tool = -> Cylinder3057
FEATURE [Part::Cut] Cut1223
  Base = -> Cut1220
  Tool = -> Box1110
FEATURE [Part::Cut] Cut1219
  Base = -> Cut1223
  Tool = -> Box1103
FEATURE [Part::Cut] Cut1226
  Base = -> Cylinder3062
  Tool = -> Cylinder3059
FEATURE [Part::Cut] Cut1229
  Base = -> Cut1217
  Tool = -> Box1112
FEATURE [Part::Cut] Cut1216
  Base = -> Cut1229
  Tool = -> Box1115
FEATURE [Part::Cut] Cut1228
  Base = -> Cut1216
  Tool = -> Box1107
FEATURE [Part::Cut] Cut1218
  Base = -> Cut1228
  Tool = -> Cylinder3065
FEATURE [Part::Cut] Cut1230
  Base = -> Cut1219
  Tool = -> Box1105
FEATURE [Part::Cut] Cut1231
  Base = -> Cylinder3058
  Placement = pos=(-3,0,0) rot=(0,0,1;0rad)
  Tool = -> Cylinder3067
FEATURE [Part::Compound] Compound1353  label="tahlo_lefto007"
  Links = -> [Cut1231,Cut1221]
FEATURE [Part::Cut] Cut1232
  Base = -> Tube021
  Tool = -> Compound1355
FEATURE [Part::Cut] Cut1224
  Base = -> Cut1232
  Tool = -> Box1108
FEATURE [Part::Cut] Cut1233
  Base = -> Cut1224
  Tool = -> Box1111
FEATURE [Part::Cut] Cut1234
  Base = -> Cut1233
  Tool = -> Box1114
FEATURE [Part::Cut] Cut1222
  Base = -> Cut1234
  Tool = -> Box1113
FEATURE [Part::Cut] Cut1227
  Base = -> Cut1222
  Tool = -> Box1106
FEATURE [Part::Cut] Cut1225
  Base = -> Cut1230
  Tool = -> Cut1227
FEATURE [Part::Compound] Compound1356  label="Grip_finger-dual-rod-revised"
  Links = -> [Compound1353,Cylinder3061,Cut1226,Cut1225,Cut1218]
FEATURE [Mesh::Feature] Mesh008  label="Grip_finger-dual-rod-revised (Meshed)"
FEATURE [Part::Box] Box261  label="Krychle261"
  AttacherType = Attacher::AttachEngine3D
  Height = 4
  Length = 5
  Placement = pos=(1,-14,8) rot=(0,0,1;0rad)
  Width = 1.4
FEATURE [Part::Cylinder] Cylinder399  label="Válec399"
  Angle = 360
  AttacherType = Attacher::AttachEngine3D
  Height = 8
  Placement = pos=(7,-10,6) rot=(0,0,1;0rad)
  Radius = 6
FEATURE [Part::Box] Box260  label="Krychle260"
  AttacherType = Attacher::AttachEngine3D
  Height = 8
  Length = 32
  Placement = pos=(1,-16,6) rot=(0,0,1;0rad)
  Width = 6
FEATURE [Part::Cylinder] Cylinder400  label="Válec400"
  Angle = 360
  AttacherType = Attacher::AttachEngine3D
  Height = 8
  Placement = pos=(27,-10,6) rot=(0,0,1;0rad)
  Radius = 6
FEATURE [Part::Box] Box267  label="Krychle267"
  AttacherType = Attacher::AttachEngine3D
  Height = 4
  Length = 5
  Placement = pos=(28,-14,8) rot=(0,0,1;0rad)
  Width = 1.4
FEATURE [Part::Cylinder] Cylinder403  label="Válec403"
  Angle = 360
  AttacherType = Attacher::AttachEngine3D
  Height = 20
  Placement = pos=(17,-10,12) rot=(1,0,0;1.5708rad)
  Radius = 1
FEATURE [Part::Cylinder] Cylinder409  label="Válec409"
  Angle = 360
  AttacherType = Attacher::AttachEngine3D
  Height = 12
  Placement = pos=(27,-10,4) rot=(0,0,1;0rad)
  Radius = 2.65
FEATURE [Part::Cylinder] Cylinder411  label="Válec411"
  Angle = 360
  AttacherType = Attacher::AttachEngine3D
  Height = 20
  Placement = pos=(31,-10,10) rot=(1,0,0;1.5708rad)
  Radius = 1
FEATURE [Part::Cylinder] Cylinder401  label="Válec401"
  Angle = 360
  AttacherType = Attacher::AttachEngine3D
  Height = 12
  Placement = pos=(7,-10,4) rot=(0,0,1;0rad)
  Radius = 2.65
FEATURE [Part::Box] Box265  label="Krychle265"
  AttacherType = Attacher::AttachEngine3D
  Height = 4
  Length = 4
  Placement = pos=(15,-11,6) rot=(0,0,1;0rad)
  Width = 1.4
FEATURE [Part::Cylinder] Cylinder402  label="Válec402"
  Angle = 360
  AttacherType = Attacher::AttachEngine3D
  Height = 20
  Placement = pos=(17,-6,8) rot=(1,0,0;1.5708rad)
  Radius = 1
FEATURE [Part::Box] Box266  label="Krychle266"
  AttacherType = Attacher::AttachEngine3D
  Height = 4
  Length = 5
  Placement = pos=(1,-14,8) rot=(0,0,1;0rad)
  Width = 1.4
FEATURE [Part::Cylinder] Cylinder405  label="Válec405"
  Angle = 360
  AttacherType = Attacher::AttachEngine3D
  Height = 20
  Placement = pos=(17,-6,12) rot=(1,0,0;1.5708rad)
  Radius = 1
FEATURE [Part::Cylinder] Cylinder406  label="Válec406"
  Angle = 360
  AttacherType = Attacher::AttachEngine3D
  Height = 20
  Placement = pos=(3,-10,10) rot=(1,0,0;1.5708rad)
  Radius = 1
FEATURE [Part::Box] Box262  label="Krychle262"
  AttacherType = Attacher::AttachEngine3D
  Height = 8
  Length = 20
  Placement = pos=(7,-16,6) rot=(0,0,1;0rad)
  Width = 12
FEATURE [Part::Cylinder] Cylinder407  label="Válec407"
  Angle = 360
  AttacherType = Attacher::AttachEngine3D
  Height = 20
  Placement = pos=(17,-6,12) rot=(1,0,0;1.5708rad)
  Radius = 1
FEATURE [Part::Cylinder] Cylinder408  label="Válec408"
  Angle = 360
  AttacherType = Attacher::AttachEngine3D
  Height = 12
  Placement = pos=(7,-10,4) rot=(0,0,1;0rad)
  Radius = 2.65
FEATURE [Part::Box] Box268  label="Krychle268"
  AttacherType = Attacher::AttachEngine3D
  Height = 4
  Length = 4
  Placement = pos=(15,-11,10) rot=(0,0,1;0rad)
  Width = 1.4
FEATURE [Part::Box] Box263  label="Krychle263"
  AttacherType = Attacher::AttachEngine3D
  Height = 4
  Length = 4
  Placement = pos=(15,-11,10) rot=(0,0,1;0rad)
  Width = 1.4
FEATURE [Part::Box] Box264  label="Krychle264"
  AttacherType = Attacher::AttachEngine3D
  Height = 4
  Length = 5
  Placement = pos=(28,-14,8) rot=(0,0,1;0rad)
  Width = 1.4
FEATURE [Part::Cylinder] Cylinder404  label="Válec404"
  Angle = 360
  AttacherType = Attacher::AttachEngine3D
  Height = 12
  Placement = pos=(27,-10,4) rot=(0,0,1;0rad)
  Radius = 2.65
FEATURE [Part::Box] Box269  label="Krychle269"
  AttacherType = Attacher::AttachEngine3D
  Height = 4
  Length = 4
  Placement = pos=(15,-11,6) rot=(0,0,1;0rad)
  Width = 1.4
FEATURE [Part::Cylinder] Cylinder410  label="Válec410"
  Angle = 360
  AttacherType = Attacher::AttachEngine3D
  Height = 20
  Placement = pos=(31,-10,10) rot=(1,0,0;1.5708rad)
  Radius = 1
FEATURE [Part::Cylinder] Cylinder413  label="Válec413"
  Angle = 360
  AttacherType = Attacher::AttachEngine3D
  Height = 20
  Placement = pos=(31,-10,10) rot=(1,0,0;1.5708rad)
  Radius = 1
FEATURE [Part::Box] Box270  label="Krychle270"
  AttacherType = Attacher::AttachEngine3D
  Height = 4
  Length = 5
  Placement = pos=(1,-14,8) rot=(0,0,1;0rad)
  Width = 1.4
FEATURE [Part::Cylinder] Cylinder418  label="Válec418"
  Angle = 360
  AttacherType = Attacher::AttachEngine3D
  Height = 12
  Placement = pos=(27,-10,4) rot=(0,0,1;0rad)
  Radius = 2.65
FEATURE [Part::Box] Box274  label="Krychle274"
  AttacherType = Attacher::AttachEngine3D
  Height = 8
  Length = 32
  Placement = pos=(1,-21,6) rot=(0,0,1;0rad)
  Width = 6
FEATURE [Part::Cylinder] Cylinder415  label="Válec415"
  Angle = 360
  AttacherType = Attacher::AttachEngine3D
  Height = 20
  Placement = pos=(3,-10,10) rot=(1,0,0;1.5708rad)
  Radius = 1
FEATURE [Part::Box] Box271  label="Krychle271"
  AttacherType = Attacher::AttachEngine3D
  Height = 4
  Length = 4
  Placement = pos=(15,-11,6) rot=(0,0,1;0rad)
  Width = 1.4
FEATURE [Part::Box] Box272  label="Krychle272"
  AttacherType = Attacher::AttachEngine3D
  Height = 4
  Length = 4
  Placement = pos=(15,-11,10) rot=(0,0,1;0rad)
  Width = 1.4
FEATURE [Part::Cylinder] Cylinder417  label="Válec417"
  Angle = 360
  AttacherType = Attacher::AttachEngine3D
  Height = 20
  Placement = pos=(17,-6,8) rot=(1,0,0;1.5708rad)
  Radius = 1
FEATURE [Part::Cylinder] Cylinder412  label="Válec412"
  Angle = 360
  AttacherType = Attacher::AttachEngine3D
  Height = 20
  Placement = pos=(3,-10,10) rot=(1,0,0;1.5708rad)
  Radius = 1
FEATURE [Part::Cylinder] Cylinder414  label="Válec414"
  Angle = 360
  AttacherType = Attacher::AttachEngine3D
  Height = 20
  Placement = pos=(17,-10,8) rot=(1,0,0;1.5708rad)
  Radius = 1
FEATURE [Part::Cylinder] Cylinder416  label="Válec416"
  Angle = 360
  AttacherType = Attacher::AttachEngine3D
  Height = 12
  Placement = pos=(7,-10,4) rot=(0,0,1;0rad)
  Radius = 2.65
FEATURE [Part::Box] Box273  label="Krychle273"
  AttacherType = Attacher::AttachEngine3D
  Height = 4
  Length = 5
  Placement = pos=(28,-14,8) rot=(0,0,1;0rad)
  Width = 1.4
FEATURE [Part::Compound] Compound187
  Links = -> [Box261,Box263,Box265,Box264]
FEATURE [Part::Compound] Compound188
  Links = -> [Box270,Box272,Box271,Box273]
FEATURE [Part::Compound] Compound189
  Links = -> [Cylinder409,Cylinder401]
FEATURE [Part::Cut] Cut247
  Base = -> Box262
  Tool = -> Compound189
FEATURE [Part::Compound] Compound190
  Links = -> [Cylinder400,Cylinder399]
FEATURE [Part::Compound] Compound193
  Links = -> [Cylinder412,Cylinder411,Cylinder414,Cylinder403]
FEATURE [Part::Compound] Compound194
  Links = -> [Cylinder415,Cylinder413,Cylinder417,Cylinder407]
FEATURE [Part::Compound] Compound195
  Links = -> [Cylinder418,Cylinder416]
FEATURE [Part::Cut] Cut245
  Base = -> Box260
  Tool = -> Compound195
FEATURE [Part::Cut] Cut246
  Base = -> Cut245
  Tool = -> Compound188
FEATURE [Part::Cut] Cut243
  Base = -> Cut246
  Tool = -> Compound194
FEATURE [Part::Compound] Compound192
  Links = -> [Cylinder406,Cylinder410,Cylinder402,Cylinder405]
FEATURE [Part::Cut] Cut249
  Base = -> Cut247
  Tool = -> Compound192
FEATURE [Part::Cut] Cut242
  Base = -> Cut249
  Tool = -> Compound187
FEATURE [Part::Compound] Compound196
  Links = -> [Cylinder404,Cylinder408]
FEATURE [Part::Cut] Cut244
  Base = -> Compound190
  Tool = -> Compound196
FEATURE [Part::Cut] Cut248
  Base = -> Cut244
  Tool = -> Compound193
FEATURE [Part::Compound] Compound191
  Links = -> [Box266,Box268,Box269,Box267]
FEATURE [Part::Cut] Cut250
  Base = -> Cut248
  Tool = -> Compound191
FEATURE [Part::Cut] Cut251
  Base = -> Cut250
  Tool = -> Box274
FEATURE [Part::Compound] Compound186  label="Wrist_root-fix"
  Links = -> [Cut242,Cut243,Cut251]
FEATURE [Part::Cylinder] Cylinder3075  label="Válec3045"
  Angle = 360
  AttacherType = Attacher::AttachEngine3D
  Height = 3
  Placement = pos=(1,14,-1.01) rot=(0,0,1;0rad)
  Radius = 1.5
FEATURE [Part::Cylinder] Cylinder3077  label="Válec3047"
  Angle = 360
  AttacherType = Attacher::AttachEngine3D
  Height = 20
  Placement = pos=(1,14,4.01) rot=(0,0,1;0rad)
  Radius = 1.5
FEATURE [Part::Cylinder] Cylinder3078  label="Válec3048"
  Angle = 360
  AttacherType = Attacher::AttachEngine3D
  Height = 12
  Placement = pos=(1,14,6) rot=(0,0,1;0rad)
  Radius = 1.5
FEATURE [Part::Box] Box1116  label="Krychle1115"
  AttacherType = Attacher::AttachEngine3D
  Height = 12
  Length = 16
  Placement = pos=(5,60.6,-2) rot=(0,0,1;0.523599rad)
  Width = 12
FEATURE [Part::Cylinder] Cylinder3076  label="Válec3046"
  Angle = 360
  AttacherType = Attacher::AttachEngine3D
  Height = 4
  Placement = pos=(1,14,0) rot=(0,0,1;0rad)
  Radius = 1.5
FEATURE [Part::Box] Box1117  label="Krychle1116"
  AttacherType = Attacher::AttachEngine3D
  Height = 2
  Length = 6
  Placement = pos=(-2,11,4) rot=(0,0,1;0rad)
  Width = 6
FEATURE [Part::Box] Box1118  label="Krychle1117"
  AttacherType = Attacher::AttachEngine3D
  Height = 2
  Length = 6
  Placement = pos=(-2,11,2) rot=(0,0,1;0rad)
  Width = 6
FEATURE [Mesh::Feature] Mesh009  label="Grip_finger-tip_lover-rev2 (Meshed)"
FEATURE [Part::Cylinder] Cylinder3079  label="Válec3049"
  Angle = 360
  AttacherType = Attacher::AttachEngine3D
  Height = 10
  Placement = pos=(-11,62.5,1) rot=(0,0,1;0rad)
  Radius = 5
FEATURE [Part::Cylinder] Cylinder3080  label="Válec3050"
  Angle = 360
  AttacherType = Attacher::AttachEngine3D
  Height = 20
  Placement = pos=(1,14,4.01) rot=(0,0,1;0rad)
  Radius = 1.5
FEATURE [Part::Cylinder] Cylinder3081  label="Válec3051"
  Angle = 360
  AttacherType = Attacher::AttachEngine3D
  Height = 20
  Placement = pos=(1,14,4.01) rot=(0,0,1;0rad)
  Radius = 1.5
FEATURE [Part::Cylinder] Cylinder3082  label="Válec3052"
  Angle = 360
  AttacherType = Attacher::AttachEngine3D
  Height = 7
  Placement = pos=(-8,61,-2) rot=(0,0,1;0rad)
  Radius = 8
FEATURE [Part::Cylinder] Cylinder3083  label="Válec3053"
  Angle = 360
  AttacherType = Attacher::AttachEngine3D
  Height = 10
  Placement = pos=(-9,61,5) rot=(0,0,1;0rad)
  Radius = 10
FEATURE [Part::Cylinder] Cylinder3084  label="Válec3054"
  Angle = 360
  AttacherType = Attacher::AttachEngine3D
  Height = 10
  Placement = pos=(-8,61,1) rot=(0,0,1;0rad)
  Radius = 5
FEATURE [Part::Cylinder] Cylinder3085  label="Válec3055"
  Angle = 360
  AttacherType = Attacher::AttachEngine3D
  Height = 4
  Placement = pos=(-7,41,6) rot=(0,0,1;0rad)
  Radius = 6
FEATURE [Part::Cylinder] Cylinder3086  label="Válec3056"
  Angle = 360
  AttacherType = Attacher::AttachEngine3D
  Height = 8
  Placement = pos=(-7,41,-2) rot=(0,0,1;0rad)
  Radius = 9
FEATURE [Part::Cylinder] Cylinder3087  label="Válec3057"
  Angle = 360
  AttacherType = Attacher::AttachEngine3D
  Height = 20
  Placement = pos=(1,14,4.01) rot=(0,0,1;0rad)
  Radius = 1.5
FEATURE [Part::Box] Box1119  label="Krychle1118"
  AttacherType = Attacher::AttachEngine3D
  Height = 12
  Length = 12
  Placement = pos=(-13,42,-2) rot=(0,0,-1;0.261799rad)
  Width = 20
FEATURE [Part::Cylinder] Cylinder3088  label="Válec3058"
  Angle = 360
  AttacherType = Attacher::AttachEngine3D
  Height = 3
  Placement = pos=(1,14,-1.01) rot=(0,0,1;0rad)
  Radius = 1.5
FEATURE [Part::Cylinder] Cylinder3089  label="Válec3059"
  Angle = 360
  AttacherType = Attacher::AttachEngine3D
  Height = 10
  Placement = pos=(-8,61,1) rot=(0,0,1;0rad)
  Radius = 5
FEATURE [Part::Box] Box1120  label="Krychle1119"
  AttacherType = Attacher::AttachEngine3D
  Height = 12
  Length = 12
  Placement = pos=(-7.85,61.2,-2) rot=(0,0,-1;0.610865rad)
  Width = 12
FEATURE [Part::Cut] Cut1236
  Base = -> Box1120
  Tool = -> Cylinder3083
FEATURE [Part::Cylinder] Cylinder3090  label="Válec3060"
  Angle = 360
  AttacherType = Attacher::AttachEngine3D
  Height = 10
  Placement = pos=(-8,61,1) rot=(0,0,1;0rad)
  Radius = 5
FEATURE [Part::Cylinder] Cylinder3091  label="Válec3061"
  Angle = 360
  AttacherType = Attacher::AttachEngine3D
  Height = 10
  Placement = pos=(-9,61,5) rot=(0,0,1;0rad)
  Radius = 10
FEATURE [Part::Cylinder] Cylinder3092  label="Válec3062"
  Angle = 360
  AttacherType = Attacher::AttachEngine3D
  Height = 3
  Placement = pos=(1,14,-1.01) rot=(0,0,1;0rad)
  Radius = 1.5
FEATURE [Part::Box] Box1121  label="Krychle1120"
  AttacherType = Attacher::AttachEngine3D
  Height = 2
  Length = 6
  Placement = pos=(-2,11,2) rot=(0,0,1;0rad)
  Width = 6
FEATURE [Part::Box] Box1122  label="Krychle1121"
  AttacherType = Attacher::AttachEngine3D
  Height = 2
  Length = 6
  Placement = pos=(-2,11,2) rot=(0,0,1;0rad)
  Width = 6
FEATURE [Part::Compound] Compound1360
  Links = -> [Box1122,Cylinder3080,Cylinder3088]
  Placement = pos=(12.3,47.5,0) rot=(0,0,1;1.309rad)
FEATURE [Part::Cylinder] Cylinder3093  label="Válec3063"
  Angle = 360
  AttacherType = Attacher::AttachEngine3D
  Height = 4
  Placement = pos=(-7,41,6) rot=(0,0,1;0rad)
  Radius = 6
FEATURE [Part::Box] Box1123  label="Krychle1122"
  AttacherType = Attacher::AttachEngine3D
  Height = 2
  Length = 6
  Placement = pos=(-2,11,2) rot=(0,0,1;0rad)
  Width = 6
FEATURE [Part::Compound] Compound1364
  Links = -> [Box1123,Cylinder3081,Cylinder3092]
  Placement = pos=(9.4,57.4,0) rot=(0,0,1;0.523599rad)
FEATURE [Part::Cylinder] Cylinder3094  label="Válec3064"
  Angle = 360
  AttacherType = Attacher::AttachEngine3D
  Height = 3
  Placement = pos=(1,14,-2) rot=(0,0,1;0rad)
  Radius = 3
FEATURE [Part::Cylinder] Cylinder3095  label="Válec3065"
  Angle = 360
  AttacherType = Attacher::AttachEngine3D
  Height = 10
  Placement = pos=(-9,61,5) rot=(0,0,1;0rad)
  Radius = 10
FEATURE [Part::Cylinder] Cylinder3096  label="Válec3066"
  Angle = 360
  AttacherType = Attacher::AttachEngine3D
  Height = 3
  Placement = pos=(1,14,-1.01) rot=(0,0,1;0rad)
  Radius = 1.5
FEATURE [Part::Cylinder] Cylinder3097  label="Válec3067"
  Angle = 360
  AttacherType = Attacher::AttachEngine3D
  Height = 20
  Placement = pos=(1,14,4.01) rot=(0,0,1;0rad)
  Radius = 1.5
FEATURE [Part::Cylinder] Cylinder3098  label="Válec3068"
  Angle = 360
  AttacherType = Attacher::AttachEngine3D
  Height = 6
  Placement = pos=(-7,41,5) rot=(0,0,1;0rad)
  Radius = 2.6
FEATURE [Part::Box] Box1124  label="Krychle1123"
  AttacherType = Attacher::AttachEngine3D
  Height = 2
  Length = 6
  Placement = pos=(-2,11,2) rot=(0,0,1;0rad)
  Width = 6
FEATURE [Part::Compound] Compound1361
  Links = -> [Box1124,Cylinder3097,Cylinder3096]
  Placement = pos=(12.3,47.5,0) rot=(0,0,1;1.309rad)
FEATURE [Part::Cylinder] Cylinder3099  label="Válec3069"
  Angle = 360
  AttacherType = Attacher::AttachEngine3D
  Height = 10
  Placement = pos=(-8,61,1) rot=(0,0,1;0rad)
  Radius = 5
FEATURE [Part::Cylinder] Cylinder3100  label="Válec3070"
  Angle = 360
  AttacherType = Attacher::AttachEngine3D
  Height = 6
  Placement = pos=(-7,41,5) rot=(0,0,1;0rad)
  Radius = 2.6
FEATURE [Part::Cylinder] Cylinder3101  label="Válec3071"
  Angle = 360
  AttacherType = Attacher::AttachEngine3D
  Height = 3
  Placement = pos=(1,14,-1.01) rot=(0,0,1;0rad)
  Radius = 1.5
FEATURE [Part::Compound] Compound1359
  Links = -> [Box1121,Cylinder3087,Cylinder3101]
  Placement = pos=(12.3,47.5,0) rot=(0,0,1;1.309rad)
FEATURE [Part::Cylinder] Cylinder3102  label="Válec3072"
  Angle = 360
  AttacherType = Attacher::AttachEngine3D
  Height = 10
  Placement = pos=(-9,61,5) rot=(0,0,1;0rad)
  Radius = 10
FEATURE [Part::Cylinder] Cylinder3103  label="Válec3073"
  Angle = 360
  AttacherType = Attacher::AttachEngine3D
  Height = 6
  Placement = pos=(-7,41,5) rot=(0,0,1;0rad)
  Radius = 2.6
FEATURE [Part::Box] Box1125  label="Krychle1124"
  AttacherType = Attacher::AttachEngine3D
  Height = 12
  Length = 12
  Placement = pos=(-7.85,61.2,-2) rot=(0,0,-1;0.610865rad)
  Width = 12
FEATURE [Part::Cylinder] Cylinder3104  label="Válec3074"
  Angle = 360
  AttacherType = Attacher::AttachEngine3D
  Height = 20
  Placement = pos=(1,14,1.01) rot=(0,0,1;0rad)
  Radius = 1.5
FEATURE [Part::Cylinder] Cylinder3105  label="Válec3075"
  Angle = 360
  AttacherType = Attacher::AttachEngine3D
  Height = 3
  Placement = pos=(1,14,-2) rot=(0,0,1;0rad)
  Radius = 3
FEATURE [Part::Box] Box1126  label="Krychle1125"
  AttacherType = Attacher::AttachEngine3D
  Height = 12
  Length = 12
  Placement = pos=(-13,42,-2) rot=(0,0,-1;0.261799rad)
  Width = 20
FEATURE [Part::Cylinder] Cylinder3106  label="Válec3076"
  Angle = 360
  AttacherType = Attacher::AttachEngine3D
  Height = 20
  Placement = pos=(1,14,1.01) rot=(0,0,1;0rad)
  Radius = 1.5
FEATURE [Part::Compound] Compound1363
  Links = -> [Cylinder3106,Cylinder3105]
  Placement = pos=(9.4,57.4,0) rot=(0,0,1;0.523599rad)
FEATURE [Part::Cylinder] Cylinder3107  label="Válec3077"
  Angle = 360
  AttacherType = Attacher::AttachEngine3D
  Height = 8
  Placement = pos=(-7,41,-2) rot=(0,0,1;0rad)
  Radius = 9
FEATURE [Part::Cylinder] Cylinder3108  label="Válec3078"
  Angle = 360
  AttacherType = Attacher::AttachEngine3D
  Height = 20
  Placement = pos=(1,14,1.01) rot=(0,0,1;0rad)
  Radius = 1.5
FEATURE [Part::Cylinder] Cylinder3109  label="Válec3079"
  Angle = 360
  AttacherType = Attacher::AttachEngine3D
  Height = 20
  Placement = pos=(1,14,1.01) rot=(0,0,1;0rad)
  Radius = 1.5
FEATURE [Part::Compound] Compound1358
  Links = -> [Cylinder3109,Cylinder3094]
  Placement = pos=(12.3,47.5,0) rot=(0,0,1;1.309rad)
FEATURE [Part::Cylinder] Cylinder3110  label="Válec3080"
  Angle = 360
  AttacherType = Attacher::AttachEngine3D
  Height = 7
  Placement = pos=(-8,61,-2) rot=(0,0,1;0rad)
  Radius = 8
FEATURE [Part::Cylinder] Cylinder3111  label="Válec3081"
  Angle = 360
  AttacherType = Attacher::AttachEngine3D
  Height = 10
  Placement = pos=(-11,62.5,1) rot=(0,0,1;0rad)
  Radius = 5
FEATURE [Part::Cut] Cut1237
  Base = -> Cylinder3110
  Tool = -> Cylinder3111
FEATURE [Part::Cylinder] Cylinder3112  label="Válec3082"
  Angle = 360
  AttacherType = Attacher::AttachEngine3D
  Height = 3
  Placement = pos=(1,14,-2) rot=(0,0,1;0rad)
  Radius = 3
FEATURE [Part::Compound] Compound1362
  Links = -> [Cylinder3104,Cylinder3112]
  Placement = pos=(12.3,47.5,0) rot=(0,0,1;1.309rad)
FEATURE [Part::Cylinder] Cylinder3113  label="Válec3083"
  Angle = 360
  AttacherType = Attacher::AttachEngine3D
  Height = 10
  Placement = pos=(-8,61,1) rot=(0,0,1;0rad)
  Radius = 5
FEATURE [Part::Cylinder] Cylinder3114  label="Válec3084"
  Angle = 360
  AttacherType = Attacher::AttachEngine3D
  Height = 6
  Placement = pos=(-7,41,5) rot=(0,0,1;0rad)
  Radius = 2.6
FEATURE [Part::Cylinder] Cylinder3115  label="Válec3085"
  Angle = 360
  AttacherType = Attacher::AttachEngine3D
  Height = 10
  Placement = pos=(-8,61,1) rot=(0,0,1;0rad)
  Radius = 5
FEATURE [Part::Cylinder] Cylinder3116  label="Válec3086"
  Angle = 360
  AttacherType = Attacher::AttachEngine3D
  Height = 3
  Placement = pos=(1,14,-2) rot=(0,0,1;0rad)
  Radius = 3
FEATURE [Part::Compound] Compound1357
  Links = -> [Cylinder3108,Cylinder3116]
  Placement = pos=(12.3,47.5,0) rot=(0,0,1;1.309rad)
FEATURE [Part::Box] Box1127  label="Krychle1126"
  AttacherType = Attacher::AttachEngine3D
  Height = 12
  Length = 9
  Placement = pos=(10.3,67.3,-2) rot=(0,0,-1;0.20944rad)
  Width = 12
FEATURE [Part::Cylinder] Cylinder3117  label="Válec3087"
  Angle = 360
  AttacherType = Attacher::AttachEngine3D
  Height = 4
  Placement = pos=(1,14,0) rot=(0,0,1;0rad)
  Radius = 1.5
FEATURE [Part::Box] Box1128  label="Krychle1127"
  AttacherType = Attacher::AttachEngine3D
  Height = 2
  Length = 6
  Placement = pos=(-2,11,4) rot=(0,0,1;0rad)
  Width = 6
FEATURE [Part::Box] Box1129  label="Krychle1128"
  AttacherType = Attacher::AttachEngine3D
  Height = 12
  Length = 16
  Placement = pos=(5,60.6,-2) rot=(0,0,1;0.523599rad)
  Width = 12
FEATURE [Part::Cylinder] Cylinder3118  label="Válec3088"
  Angle = 360
  AttacherType = Attacher::AttachEngine3D
  Height = 20
  Placement = pos=(1,14,1.01) rot=(0,0,1;0rad)
  Radius = 1.5
FEATURE [Part::Cylinder] Cylinder3119  label="Válec3089"
  Angle = 360
  AttacherType = Attacher::AttachEngine3D
  Height = 4
  Placement = pos=(1,14,0) rot=(0,0,1;0rad)
  Radius = 1.5
FEATURE [Part::Box] Box1130  label="Krychle1129"
  AttacherType = Attacher::AttachEngine3D
  Height = 2
  Length = 6
  Placement = pos=(-2,11,4) rot=(0,0,1;0rad)
  Width = 6
FEATURE [Part::Cylinder] Cylinder3120  label="Válec3090"
  Angle = 360
  AttacherType = Attacher::AttachEngine3D
  Height = 12
  Placement = pos=(1,14,6) rot=(0,0,1;0rad)
  Radius = 1.5
FEATURE [Part::Cylinder] Cylinder3121  label="Válec3091"
  Angle = 360
  AttacherType = Attacher::AttachEngine3D
  Height = 3
  Placement = pos=(1,14,-2) rot=(0,0,1;0rad)
  Radius = 3
FEATURE [Part::Cylinder] Cylinder3122  label="Válec3092"
  Angle = 360
  AttacherType = Attacher::AttachEngine3D
  Height = 12
  Placement = pos=(1,14,6) rot=(0,0,1;0rad)
  Radius = 1.5
FEATURE [Part::Cylinder] Cylinder3073  label="Válec3043"
  Angle = 360
  AttacherType = Attacher::AttachEngine3D
  Height = 4
  Placement = pos=(1,14,0) rot=(0,0,1;0rad)
  Radius = 1.5
FEATURE [Part::Box] Box1131  label="Krychle1130"
  AttacherType = Attacher::AttachEngine3D
  Height = 12
  Length = 9
  Placement = pos=(10.3,67.3,-2) rot=(0,0,-1;0.20944rad)
  Width = 12
FEATURE [Part::Box] Box1132  label="Krychle1131"
  AttacherType = Attacher::AttachEngine3D
  Height = 2
  Length = 6
  Placement = pos=(-2,11,4) rot=(0,0,1;0rad)
  Width = 6
FEATURE [Part::Cylinder] Cylinder3074  label="Válec3044"
  Angle = 360
  AttacherType = Attacher::AttachEngine3D
  Height = 12
  Placement = pos=(1,14,6) rot=(0,0,1;0rad)
  Radius = 1.5
FEATURE [Part::Cut] Cut1238
  Base = -> Cylinder3093
  Tool = -> Cylinder3103
FEATURE [Part::Cut] Cut1239
  Base = -> Cylinder3085
  Tool = -> Cylinder3098
FEATURE [Part::Cut] Cut1244
  Base = -> Cylinder3082
  Tool = -> Cylinder3079
FEATURE [Part::Cut] Cut1245
  Base = -> Box1125
  Tool = -> Cylinder3095
FEATURE [Part::Cut] Cut1246
  Base = -> Cut1237
  Tool = -> Compound1357
FEATURE [Part::Cut] Cut1247
  Base = -> Cut1236
  Tool = -> Cylinder3090
FEATURE [Part::Fillet] Fillet057
  Base = -> Cut1247
  Edges = 1 edges r=3: [Edge5]
FEATURE [Part::Cut] Cut1248
  Base = -> Cut1244
  Tool = -> Compound1359
FEATURE [Part::Cut] Cut1253
  Base = -> Box1119
  Tool = -> Cylinder3086
FEATURE [Part::Cut] Cut1250
  Base = -> Cut1253
  Tool = -> Cylinder3091
FEATURE [Part::Cut] Cut1251
  Base = -> Cut1250
  Tool = -> Cylinder3089
FEATURE [Part::Fillet] Fillet059
  Base = -> Cut1251
  Edges = 1 edges r=2: [Edge3]
FEATURE [Part::Fillet] Fillet060
  Base = -> Fillet059
  Edges = 1 edges r=1: [Edge28]
FEATURE [Part::Cut] Cut1249
  Base = -> Fillet060
  Tool = -> Compound1360
FEATURE [Part::Cut] Cut1242
  Base = -> Cut1249
  Tool = -> Cylinder3100
FEATURE [Part::Cut] Cut1256
  Base = -> Fillet057
  Tool = -> Cylinder3084
FEATURE [Part::Cut] Cut1252
  Base = -> Cut1256
  Tool = -> Compound1361
FEATURE [Part::Cut] Cut1254
  Base = -> Cut1252
  Tool = -> Compound1364
FEATURE [Part::Cut] Cut1259
  Base = -> Cut1245
  Tool = -> Cylinder3115
FEATURE [Part::Fillet] Fillet062
  Base = -> Cut1259
  Edges = 1 edges r=3: [Edge5]
FEATURE [Part::Cut] Cut1243
  Base = -> Fillet062
  Tool = -> Cylinder3113
FEATURE [Part::Cut] Cut1255
  Base = -> Cut1243
  Tool = -> Compound1358
FEATURE [Part::Cut] Cut1258
  Base = -> Cut1255
  Tool = -> Compound1363
FEATURE [Part::Cut] Cut1260
  Base = -> Box1126
  Tool = -> Cylinder3107
FEATURE [Part::Cut] Cut1235
  Base = -> Cut1260
  Tool = -> Cylinder3102
FEATURE [Part::Cut] Cut1240
  Base = -> Cut1235
  Tool = -> Cylinder3099
FEATURE [Part::Fillet] Fillet058
  Base = -> Cut1240
  Edges = 1 edges r=2: [Edge3]
FEATURE [Part::Fillet] Fillet061
  Base = -> Fillet058
  Edges = 1 edges r=1: [Edge28]
FEATURE [Part::Cut] Cut1257
  Base = -> Fillet061
  Tool = -> Compound1362
FEATURE [Part::Cut] Cut1241
  Base = -> Cut1257
  Tool = -> Cylinder3114
FEATURE [Part::Compound] Compound1365
  Links = -> [Cylinder3118,Cylinder3121]
  Placement = pos=(13.4,59.4,0) rot=(0,0,1;0.523599rad)
FEATURE [Part::Cut] Cut1263
  Base = -> Box1129
  Tool = -> Compound1365
FEATURE [Part::Compound] Compound1366
  Links = -> [Box1130,Cylinder3120,Cylinder3119]
  Placement = pos=(11.0015,75.5987,15) rot=(-0.476905,0.621515,-0.621515;2.25159rad)
FEATURE [Part::Cut] Cut1262
  Base = -> Box1127
  Tool = -> Compound1366
FEATURE [Part::Compound] Compound1367
  Links = -> [Box1128,Cylinder3122,Cylinder3117]
  Placement = pos=(11.0015,75.5987,15) rot=(-0.476905,0.621515,-0.621515;2.25159rad)
FEATURE [Part::Cut] Cut1261
  Base = -> Cut1263
  Tool = -> Compound1367
FEATURE [Mesh::Feature] Mesh010  label="Grip_finger-tip_upper-rev2 (Meshed)"
FEATURE [Part::Fillet] Fillet063
  Base = -> Cut1262
  Edges = 1 edges r=4: [Edge7]
FEATURE [Part::Compound] Compound1368  label="Grip_finger-tip_lower-rev2"
  Links = -> [Cut1261,Fillet063,Cut1246,Cut1238,Cut1258,Cut1241]
FEATURE [Part::Compound] Compound1369
  Links = -> [Box1132,Cylinder3074,Cylinder3073]
  Placement = pos=(11.0015,75.5987,15) rot=(-0.476905,0.621515,-0.621515;2.25159rad)
FEATURE [Part::Cut] Cut1264
  Base = -> Box1131
  Tool = -> Compound1369
FEATURE [Part::Fillet] Fillet064
  Base = -> Cut1264
  Edges = 1 edges r=4: [Edge7]
FEATURE [Part::Compound] Compound1370
  Links = -> [Box1118,Cylinder3077,Cylinder3075]
  Placement = pos=(13.4,59.4,0) rot=(0,0,1;0.523599rad)
FEATURE [Part::Cut] Cut1265
  Base = -> Box1116
  Tool = -> Compound1370
FEATURE [Part::Compound] Compound1371
  Links = -> [Box1117,Cylinder3078,Cylinder3076]
  Placement = pos=(11.0015,75.5987,15) rot=(-0.476905,0.621515,-0.621515;2.25159rad)
FEATURE [Part::Cut] Cut001
  Base = -> Cut1265
  Tool = -> Compound1371
FEATURE [Part::Compound] Compound1372  label="Grip_finger-tip_upper-rev2"
  Links = -> [Cut001,Fillet064,Cut1242,Cut1248,Cut1239,Cut1254]
FEATURE [Mesh::Feature] Mesh011  label="Wrist_root-fix (Meshed)"
FEATURE [Part::Box] Box1133  label="Krychle1132"
  AttacherType = Attacher::AttachEngine3D
  Height = 2
  Length = 6
  Placement = pos=(-2,11,4) rot=(0,0,1;0rad)
  Width = 6
FEATURE [Part::Box] Box1134  label="Krychle1133"
  AttacherType = Attacher::AttachEngine3D
  Height = 12
  Length = 2
  Placement = pos=(21.4,80,-2) rot=(0,0,1;0rad)
  Width = 19
FEATURE [Part::Cylinder] Cylinder3123  label="Válec3093"
  Angle = 360
  AttacherType = Attacher::AttachEngine3D
  Height = 12
  Placement = pos=(1,14,6) rot=(0,0,1;0rad)
  Radius = 1.5
FEATURE [Part::Cylinder] Cylinder3124  label="Válec3094"
  Angle = 360
  AttacherType = Attacher::AttachEngine3D
  Height = 3
  Placement = pos=(1,14,6) rot=(0,0,1;0rad)
  Radius = 3
FEATURE [Part::Cylinder] Cylinder3125  label="Válec3095"
  Angle = 360
  AttacherType = Attacher::AttachEngine3D
  Height = 12
  Placement = pos=(1,14,6) rot=(0,0,1;0rad)
  Radius = 1.5
FEATURE [Part::Cylinder] Cylinder3126  label="Válec3096"
  Angle = 360
  AttacherType = Attacher::AttachEngine3D
  Height = 4
  Placement = pos=(1,14,-0.1) rot=(0,0,1;0rad)
  Radius = 1.5
FEATURE [Part::Cylinder] Cylinder3127  label="Válec3097"
  Angle = 360
  AttacherType = Attacher::AttachEngine3D
  Height = 4
  Placement = pos=(1,14,-0.1) rot=(0,0,1;0rad)
  Radius = 1.5
FEATURE [Part::Cylinder] Cylinder3128  label="Válec3098"
  Angle = 360
  AttacherType = Attacher::AttachEngine3D
  Height = 3
  Placement = pos=(1,14,6) rot=(0,0,1;0rad)
  Radius = 3
FEATURE [Part::Box] Box1135  label="Krychle1134"
  AttacherType = Attacher::AttachEngine3D
  Height = 2
  Length = 6
  Placement = pos=(-2,11,4) rot=(0,0,1;0rad)
  Width = 6
FEATURE [Part::Box] Box1136  label="Krychle1135"
  AttacherType = Attacher::AttachEngine3D
  Height = 12
  Length = 1
  Placement = pos=(21.4,-4.5,-2) rot=(0,0,1;0rad)
  Width = 10
FEATURE [Part::Compound] Compound1373
  Links = -> [Box1133,Cylinder3123,Cylinder3126]
  Placement = pos=(6,73,2) rot=(0,1,0;1.5708rad)
FEATURE [Part::Cut] Cut1268
  Base = -> Box1134
  Tool = -> Compound1373
FEATURE [Part::Compound] Compound1374
  Links = -> [Box1135,Cylinder3125,Cylinder3127]
  Placement = pos=(6,-14,2) rot=(0,1,0;1.5708rad)
FEATURE [Part::Cut] Cut1267
  Base = -> Box1136
  Tool = -> Compound1374
FEATURE [Part::Compound] Compound1375
  Links = -> [Cylinder3124]
  Placement = pos=(16.5,73,2) rot=(0,1,0;1.5708rad)
FEATURE [Part::Cut] Cut1269
  Base = -> Cut1268
  Tool = -> Compound1375
FEATURE [Part::Chamfer] Chamfer182
  Base = -> Cut1269
  Edges = 1 edges r=1.9: [Edge4]
  Placement = pos=(0,-7,0) rot=(0,0,1;0rad)
FEATURE [Part::Compound] Compound1376
  Links = -> [Cylinder3128]
  Placement = pos=(16.5,73,2) rot=(0,1,0;1.5708rad)
FEATURE [Part::FeaturePython] involuterack002  # WARN: FeaturePython — macro-defined, semantics opaque (R4)
  AttacherType = Attacher::AttachEngine3D
  Placement = pos=(23,6,-2) rot=(0,0,1;0rad)
  add_endings = true
  beta = 0
  clearance = 0.25
  double_helix = false
  head = 0
  height = 12
  module = 0.5
  pressure_angle = 20
  properties_from_tool = true
  simplified = false
  teeth = 44
  thickness = 1
  transverse_pitch = 1.5708
  version = 0.0.3
FEATURE [Part::FeaturePython] involuterack003  # WARN: FeaturePython — macro-defined, semantics opaque (R4)
  AttacherType = Attacher::AttachEngine3D
  Placement = pos=(25,81,-2) rot=(0,0,1;0rad)
  add_endings = true
  beta = 0
  clearance = 0.25
  double_helix = false
  head = 0
  height = 12
  module = 0.5
  pressure_angle = 20
  properties_from_tool = true
  simplified = false
  teeth = 12
  thickness = 1
  transverse_pitch = 1.5708
  version = 0.0.3
FEATURE [Part::Cut] Cut1266
  Base = -> involuterack003
  Placement = pos=(0,-7,0) rot=(0,0,1;0rad)
  Tool = -> Compound1376
FEATURE [Part::Compound] Compound1377  label="Grip_finger-zubacka"
  Links = -> [Cut1267,involuterack002,Cut1266,Chamfer182]
FEATURE [Mesh::Feature] Mesh012  label="Grip_finger-tip_upper (Meshed)001"
FEATURE [Mesh::Feature] Mesh013  label="Grip_finger-root_upper (Meshed)001"
FEATURE [Mesh::Feature] Mesh014  label="Grip_slider-opposite (Meshed)001"
FEATURE [Mesh::Feature] Mesh015  label="Grip_slider (Meshed)001"
FEATURE [Mesh::Feature] Mesh016  label="Grip_ufo (Meshed)001"
FEATURE [Mesh::Feature] Mesh017  label="Grip_finger-tip_lower (Meshed)001"
FEATURE [Mesh::Feature] Mesh018  label="Grip_finger-tip_lower (Meshed)002"
FEATURE [Mesh::Feature] Mesh019  label="Grip_finger-root_lower (Meshed)001"
FEATURE [Mesh::Feature] Mesh020  label="Grip_finger-dual-rod-thin (Meshed)"
FEATURE [Mesh::Feature] Mesh021  label="Grip_finger-tip_upper-revised (Meshed)"
FEATURE [Mesh::Feature] Mesh022  label="Grip_finger-tip_lower-revised (Meshed)"
FEATURE [Mesh::Feature] Mesh023  label="Grip_finger-dual-rod-revised (Meshed)001"
FEATURE [Mesh::Feature] Mesh024  label="Wrist_root-fix (Meshed)001"
FEATURE [Mesh::Feature] Mesh025  label="Grip_finger-tip_upper-rev2 (Meshed)001"
FEATURE [Mesh::Feature] Mesh026  label="Grip_finger-tip_lower-rev2 (Meshed)"
